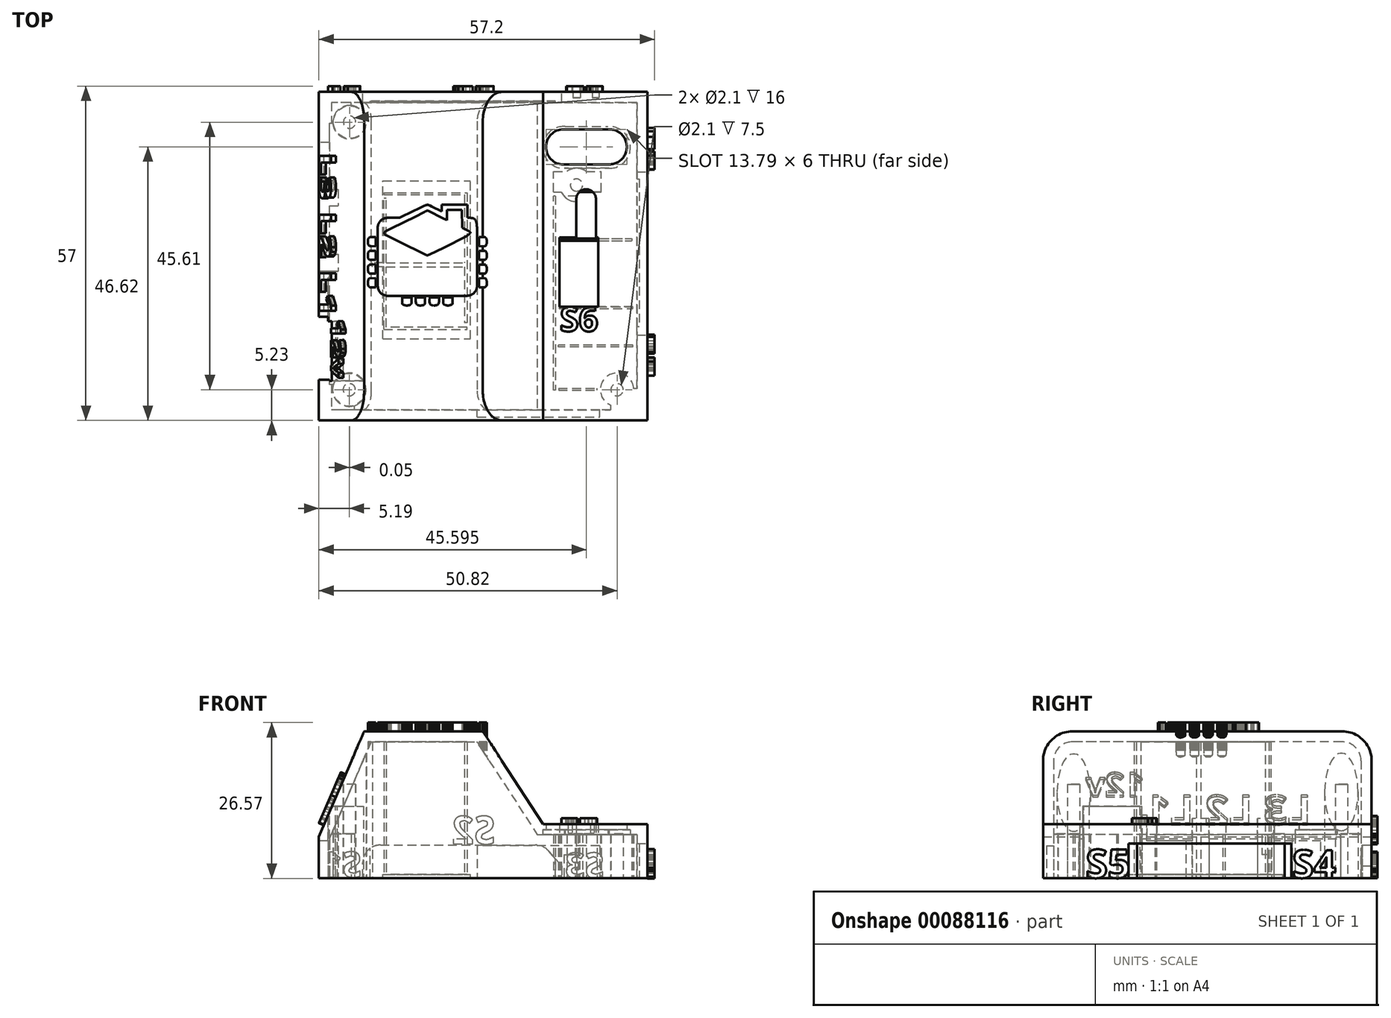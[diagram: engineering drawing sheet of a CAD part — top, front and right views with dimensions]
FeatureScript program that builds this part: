
annotation { "Feature Type Name" : "Feature", "Feature Type Description" : "" }
export const myFeature = defineFeature(function(context is Context, id is Id, definition is map)
    precondition{}
    {
        {
            var Q0;
            Q0=qCreatedBy(makeId("Top.planeOp"),FACE);
            var sketch = newSketch(context, id + "F0", { "sketchPlane" : qUnion([Q0])});
            skLineSegment(sketch, "E0.rect.bottom", {"start": v(22.84, -21.13) * mm, "end": v(-26.83, -21.13) * mm});
            skLineSegment(sketch, "E0.rect.top", {"start": v(22.84, 28.7) * mm, "end": v(-26.83, 28.7) * mm});
            skLineSegment(sketch, "E0.rect.left", {"start": v(22.84, -21.13) * mm, "end": v(22.84, 28.7) * mm});
            skPoint(sketch, "E0.rect.middle", {"position": v(-2, 3.78) * mm});
            skCircle(sketch, "E1", {"center": v(-24.81, -18.99) * mm, "radius": 1.05 * mm});
            skCircle(sketch, "E2", {"center": v(-24.76, 26.62) * mm, "radius": 1.05 * mm});
            skCircle(sketch, "E3", {"center": v(13.92, 15.91) * mm, "radius": 1.05 * mm});
            skLineSegment(sketch, "E4", {"start": v(-2, -21.13) * mm, "end": v(-2, -18.21) * mm});
            skCircle(sketch, "E5.MirrorC", {"center": v(20.82, -18.99) * mm, "radius": 1.05 * mm});
            skLineSegment(sketch, "E6.rect.bottom", {"start": v(24.75, -22.97) * mm, "end": v(-28.75, -22.97) * mm});
            skLineSegment(sketch, "E6.rect.top", {"start": v(24.75, 30.53) * mm, "end": v(-28.75, 30.53) * mm});
            skLineSegment(sketch, "E6.rect.left", {"start": v(24.75, -22.97) * mm, "end": v(24.75, 30.53) * mm});
            skLineSegment(sketch, "E6.rect.right", {"start": v(-28.75, -22.97) * mm, "end": v(-28.75, 30.53) * mm});
            skLineSegment(sketch, "E7.rect.bottom", {"start": v(26, -24.22) * mm, "end": v(-30, -24.22) * mm});
            skLineSegment(sketch, "E7.rect.top", {"start": v(26, 31.78) * mm, "end": v(-30, 31.78) * mm});
            skLineSegment(sketch, "E7.rect.left", {"start": v(26, -24.22) * mm, "end": v(26, 31.78) * mm});
            skLineSegment(sketch, "E7.rect.right", {"start": v(-30, -24.22) * mm, "end": v(-30, 31.78) * mm});
            skPoint(sketch, "E8", {"position": v(8.65, 14) * mm});
            skSolve(sketch);
        }
        {
            var Q0;
            Q0=qSketchRegion(id+"F0",true);
            var Q1;
            Q1=makeQuery(id+"F0.imprint","IMPRINT",FACE,{"disambiguationData":[TD([[makeQuery(id+"F0.imprint","IMPRINT",EDGE,{"derivedFrom":sQuery(id+"F0.wireOp",EDGE,"E1")}),-1.0]])]});
            extrude(context, id + "F1", {"entities" : qUnion([Q0, Q1]), "depth" : 25 * mm});
        }
        {
            var Q0;
            Q0=qCreatedBy(makeId("Front.planeOp"),FACE);
            var sketch = newSketch(context, id + "F2", { "sketchPlane" : qUnion([Q0])});
            skLineSegment(sketch, "E9", {"start": v(0, 0) * mm, "end": v(0, 7) * mm});
            skLineSegment(sketch, "E10", {"start": v(0, 7) * mm, "end": v(26.03, 7) * mm});
            skLineSegment(sketch, "E11", {"start": v(26.03, 9.19) * mm, "end": v(26.03, 25.51) * mm});
            skLineSegment(sketch, "E12", {"start": v(15.3, 7) * mm, "end": v(26.03, 7) * mm});
            skLineSegment(sketch, "E13", {"start": v(0, 7) * mm, "end": v(-30.02, 7) * mm});
            skLineSegment(sketch, "E14", {"start": v(-30.02, 7) * mm, "end": v(-22.06, 25.51) * mm});
            skLineSegment(sketch, "E15", {"start": v(-22.06, 25.51) * mm, "end": v(-2.39, 25.51) * mm});
            skLineSegment(sketch, "E16", {"start": v(26.03, 25.51) * mm, "end": v(-2.39, 25.51) * mm});
            skLineSegment(sketch, "E17", {"start": v(-22.06, 25.51) * mm, "end": v(-30.02, 25.51) * mm});
            skLineSegment(sketch, "E18", {"start": v(-30.02, 25.51) * mm, "end": v(-30.02, 7) * mm});
            skLineSegment(sketch, "E19", {"start": v(18.06, 10.7) * mm, "end": v(18.04, 10.7) * mm});
            skLineSegment(sketch, "E20", {"start": v(19.86, 9.19) * mm, "end": v(8.2, 9.19) * mm});
            skLineSegment(sketch, "E21", {"start": v(8.2, 9.19) * mm, "end": v(-2.39, 25.51) * mm});
            skLineSegment(sketch, "E22", {"start": v(19.86, 9.19) * mm, "end": v(26.03, 9.19) * mm});
            skSolve(sketch);
        }
        {
            var Q0;
            Q0=makeQuery(id+"F2.imprint","IMPRINT",FACE,{"disambiguationData":[TD([[makeQuery(id+"F2.imprint","IMPRINT",EDGE,{"derivedFrom":sQuery(id+"F2.wireOp",EDGE,"E14")}),1.0]])]});
            var Q1;
            {var subQ0=sQuery(id+"F2.wireOp",EDGE,"E11");Q1=makeQuery(id+"F2.imprint","IMPRINT",FACE,{"disambiguationData":[TD([[makeQuery(id+"F2.imprint","IMPRINT",EDGE,{"derivedFrom":subQ0}),1.0]])]});}
            extrude(context, id + "F3", {"entities" : qUnion([Q0, Q1]), "operationType" : NewBodyOperationType.REMOVE, "endBound" : BoundingType.UP_TO_NEXT, "oppositeDirection" : true, "depth" : 25 * mm, "hasSecondDirection" : true, "secondDirectionOppositeDirection" : false, "secondDirectionDepth" : 25 * mm});
        }
        {
            var Q0;
            Q0=makeQuery(id+"F1.opExtrude","CAP_EDGE",EDGE,{"disambiguationData":[OSD([sQuery(id+"F0.wireOp",EDGE,"E7.rect.right")])],"isStart":false});
            var Q1;
            Q1=makeQuery(id+"F3.boolean.opBoolean","COPY",EDGE,{"derivedFrom":makeQuery(id+"F3.opExtrude","TWEAK_EDGE",EDGE,{"derivedFrom":[makeQuery(id+"F1.opExtrude","CAP_FACE",FACE,{"disambiguationData":[OSD([sQuery(id+"F0.wireOp",EDGE,"E1"),sQuery(id+"F0.wireOp",EDGE,"E2"),sQuery(id+"F0.wireOp",EDGE,"E3"),sQuery(id+"F0.wireOp",EDGE,"E5.MirrorC"),sQuery(id+"F0.wireOp",EDGE,"E7.rect.bottom"),sQuery(id+"F0.wireOp",EDGE,"E7.rect.top"),sQuery(id+"F0.wireOp",EDGE,"E7.rect.left"),sQuery(id+"F0.wireOp",EDGE,"E7.rect.right")])],"isStart":false}),makeQuery(id+"F2.imprint","IMPRINT",EDGE,{"derivedFrom":sQuery(id+"F2.wireOp",EDGE,"ff17f17f-c23f-4b7b-92e3-773d52701edb")})]})});
            var Q2;
            Q2=makeQuery(id+"F3.boolean.opBoolean","COPY",EDGE,{"derivedFrom":makeQuery(id+"F3.opExtrude","TWEAK_EDGE",EDGE,{"derivedFrom":[makeQuery(id+"F1.opExtrude","CAP_FACE",FACE,{"disambiguationData":[OSD([sQuery(id+"F0.wireOp",EDGE,"E1"),sQuery(id+"F0.wireOp",EDGE,"E2"),sQuery(id+"F0.wireOp",EDGE,"E3"),sQuery(id+"F0.wireOp",EDGE,"E5.MirrorC"),sQuery(id+"F0.wireOp",EDGE,"E7.rect.bottom"),sQuery(id+"F0.wireOp",EDGE,"E7.rect.top"),sQuery(id+"F0.wireOp",EDGE,"E7.rect.left"),sQuery(id+"F0.wireOp",EDGE,"E7.rect.right")])],"isStart":false}),makeQuery(id+"F2.imprint","IMPRINT",EDGE,{"derivedFrom":sQuery(id+"F2.wireOp",EDGE,"7c30f75c-de24-4105-9ec6-0528e7197d9e")})]})});
            var Q3;
            {var subQ0=sQuery(id+"F2.wireOp",EDGE,"cpQ2IQLn-lepx-jHqE-Occg-QwCyzWVKbBFz");var subQ1=sQuery(id+"F2.wireOp",EDGE,"9136473a-ce9f-4df1-8e41-d79c079f6f02");var subQ2=makeQuery(id+"F2.imprint","INTERSECT",VERTEX,{"disambiguationData":[OD(0.0)],"derivedFrom":[subQ1,subQ0]});var subQ4=makeQuery(id+"F2.imprint","INTERSECT",VERTEX,{"disambiguationData":[OD(1.0)],"derivedFrom":[subQ1,subQ0]});Q3=makeQuery(id+"F3.boolean.opBoolean","COPY",EDGE,{"derivedFrom":makeQuery(id+"F3.opExtrude","TWEAK_EDGE",EDGE,{"derivedFrom":[makeQuery(id+"F1.opExtrude","CAP_FACE",FACE,{"disambiguationData":[OSD([sQuery(id+"F0.wireOp",EDGE,"E1"),sQuery(id+"F0.wireOp",EDGE,"E2"),sQuery(id+"F0.wireOp",EDGE,"E3"),sQuery(id+"F0.wireOp",EDGE,"E5.MirrorC"),sQuery(id+"F0.wireOp",EDGE,"E7.rect.bottom"),sQuery(id+"F0.wireOp",EDGE,"E7.rect.top"),sQuery(id+"F0.wireOp",EDGE,"E7.rect.left"),sQuery(id+"F0.wireOp",EDGE,"E7.rect.right")])],"isStart":false}),makeQuery(id+"F2.imprint","IMPRINT",EDGE,{"disambiguationData":[TD([[subQ4,1.0]])],"derivedFrom":subQ0}),makeQuery(id+"F2.imprint","IMPRINT",EDGE,{"disambiguationData":[TD([[subQ2,1.0]])],"derivedFrom":subQ0}),makeQuery(id+"F2.imprint","IMPRINT",EDGE,{"disambiguationData":[TD([[subQ2,-1.0]])],"derivedFrom":subQ0})]})});}
            var Q4;
            {var subQ0=sQuery(id+"F2.wireOp",EDGE,"cpQ2IQLn-lepx-jHqE-Occg-QwCyzWVKbBFz");var subQ1=sQuery(id+"F2.wireOp",EDGE,"9136473a-ce9f-4df1-8e41-d79c079f6f02");var subQ2=makeQuery(id+"F2.imprint","INTERSECT",VERTEX,{"disambiguationData":[OD(0.0)],"derivedFrom":[subQ1,subQ0]});var subQ3=sQuery(id+"F2.wireOp",EDGE,"7c30f75c-de24-4105-9ec6-0528e7197d9e");var subQ4=makeQuery(id+"F2.imprint","INTERSECT",VERTEX,{"derivedFrom":[subQ3,subQ0]});var subQ5=makeQuery(id+"F2.imprint","INTERSECT",VERTEX,{"disambiguationData":[OD(1.0)],"derivedFrom":[subQ1,subQ0]});Q4=makeQuery(id+"F3.boolean.opBoolean","COPY",EDGE,{"derivedFrom":makeQuery(id+"F3.opExtrude","TWEAK_EDGE",EDGE,{"disambiguationData":[OD(0.0)],"derivedFrom":[makeQuery(id+"F2.imprint","IMPRINT",EDGE,{"disambiguationData":[TD([[subQ4,1.0]])],"derivedFrom":subQ3}),makeQuery(id+"F2.imprint","IMPRINT",EDGE,{"disambiguationData":[TD([[subQ5,1.0]])],"derivedFrom":subQ0}),makeQuery(id+"F2.imprint","IMPRINT",EDGE,{"disambiguationData":[TD([[subQ2,1.0]])],"derivedFrom":subQ0}),makeQuery(id+"F2.imprint","IMPRINT",EDGE,{"disambiguationData":[TD([[subQ2,-1.0]])],"derivedFrom":subQ0})]})});}
            var Q5;
            {var subQ0=sQuery(id+"F2.wireOp",EDGE,"cpQ2IQLn-lepx-jHqE-Occg-QwCyzWVKbBFz");var subQ1=sQuery(id+"F2.wireOp",EDGE,"9136473a-ce9f-4df1-8e41-d79c079f6f02");var subQ2=makeQuery(id+"F2.imprint","INTERSECT",VERTEX,{"disambiguationData":[OD(0.0)],"derivedFrom":[subQ1,subQ0]});var subQ3=sQuery(id+"F2.wireOp",EDGE,"7c30f75c-de24-4105-9ec6-0528e7197d9e");var subQ4=makeQuery(id+"F2.imprint","INTERSECT",VERTEX,{"derivedFrom":[subQ3,subQ0]});var subQ5=makeQuery(id+"F2.imprint","INTERSECT",VERTEX,{"disambiguationData":[OD(1.0)],"derivedFrom":[subQ1,subQ0]});Q5=makeQuery(id+"F3.boolean.opBoolean","COPY",EDGE,{"derivedFrom":makeQuery(id+"F3.opExtrude","TWEAK_EDGE",EDGE,{"disambiguationData":[OD(1.0)],"derivedFrom":[makeQuery(id+"F2.imprint","IMPRINT",EDGE,{"disambiguationData":[TD([[subQ4,1.0]])],"derivedFrom":subQ3}),makeQuery(id+"F2.imprint","IMPRINT",EDGE,{"disambiguationData":[TD([[subQ5,1.0]])],"derivedFrom":subQ0}),makeQuery(id+"F2.imprint","IMPRINT",EDGE,{"disambiguationData":[TD([[subQ2,1.0]])],"derivedFrom":subQ0}),makeQuery(id+"F2.imprint","IMPRINT",EDGE,{"disambiguationData":[TD([[subQ2,-1.0]])],"derivedFrom":subQ0})]})});}
            var Q6;
            Q6=makeQuery(id+"F1.opExtrude","CAP_EDGE",EDGE,{"disambiguationData":[OSD([sQuery(id+"F0.wireOp",EDGE,"E7.rect.bottom")])],"isStart":false});
            var Q7;
            {var subQ0=sQuery(id+"F2.wireOp",EDGE,"cpQ2IQLn-lepx-jHqE-Occg-QwCyzWVKbBFz");var subQ1=sQuery(id+"F2.wireOp",EDGE,"9136473a-ce9f-4df1-8e41-d79c079f6f02");var subQ2=makeQuery(id+"F2.imprint","INTERSECT",VERTEX,{"disambiguationData":[OD(0.0)],"derivedFrom":[subQ1,subQ0]});var subQ4=makeQuery(id+"F2.imprint","INTERSECT",VERTEX,{"disambiguationData":[OD(1.0)],"derivedFrom":[subQ1,subQ0]});Q7=makeQuery(id+"F3.boolean.opBoolean","COPY",EDGE,{"derivedFrom":makeQuery(id+"F3.opExtrude","TWEAK_EDGE",EDGE,{"derivedFrom":[makeQuery(id+"F1.opExtrude","SWEPT_FACE",FACE,{"disambiguationData":[OSD([sQuery(id+"F0.wireOp",EDGE,"E7.rect.bottom")])]}),makeQuery(id+"F2.imprint","IMPRINT",EDGE,{"disambiguationData":[TD([[subQ4,1.0]])],"derivedFrom":subQ0}),makeQuery(id+"F2.imprint","IMPRINT",EDGE,{"disambiguationData":[TD([[subQ2,1.0]])],"derivedFrom":subQ0}),makeQuery(id+"F2.imprint","IMPRINT",EDGE,{"disambiguationData":[TD([[subQ2,-1.0]])],"derivedFrom":subQ0})]})});}
            var Q8;
            Q8=makeQuery(id+"F1.opExtrude","CAP_EDGE",EDGE,{"disambiguationData":[OSD([sQuery(id+"F0.wireOp",EDGE,"E7.rect.top")])],"isStart":false});
            var Q9;
            {var subQ0=sQuery(id+"F2.wireOp",EDGE,"cpQ2IQLn-lepx-jHqE-Occg-QwCyzWVKbBFz");var subQ1=sQuery(id+"F2.wireOp",EDGE,"9136473a-ce9f-4df1-8e41-d79c079f6f02");var subQ2=makeQuery(id+"F2.imprint","INTERSECT",VERTEX,{"disambiguationData":[OD(0.0)],"derivedFrom":[subQ1,subQ0]});var subQ4=makeQuery(id+"F2.imprint","INTERSECT",VERTEX,{"disambiguationData":[OD(1.0)],"derivedFrom":[subQ1,subQ0]});Q9=makeQuery(id+"F3.boolean.opBoolean","COPY",EDGE,{"derivedFrom":makeQuery(id+"F3.opExtrude","TWEAK_EDGE",EDGE,{"derivedFrom":[makeQuery(id+"F1.opExtrude","SWEPT_FACE",FACE,{"disambiguationData":[OSD([sQuery(id+"F0.wireOp",EDGE,"E7.rect.top")])]}),makeQuery(id+"F2.imprint","IMPRINT",EDGE,{"disambiguationData":[TD([[subQ4,1.0]])],"derivedFrom":subQ0}),makeQuery(id+"F2.imprint","IMPRINT",EDGE,{"disambiguationData":[TD([[subQ2,1.0]])],"derivedFrom":subQ0}),makeQuery(id+"F2.imprint","IMPRINT",EDGE,{"disambiguationData":[TD([[subQ2,-1.0]])],"derivedFrom":subQ0})]})});}
            var Q10;
            Q10=makeQuery(id+"F3.boolean.opBoolean","COPY",EDGE,{"derivedFrom":makeQuery(id+"F3.opExtrude","TWEAK_EDGE",EDGE,{"derivedFrom":[makeQuery(id+"F1.opExtrude","CAP_FACE",FACE,{"disambiguationData":[OSD([sQuery(id+"F0.wireOp",EDGE,"E1"),sQuery(id+"F0.wireOp",EDGE,"E2"),sQuery(id+"F0.wireOp",EDGE,"E3"),sQuery(id+"F0.wireOp",EDGE,"E5.MirrorC"),sQuery(id+"F0.wireOp",EDGE,"E7.rect.bottom"),sQuery(id+"F0.wireOp",EDGE,"E7.rect.top"),sQuery(id+"F0.wireOp",EDGE,"E7.rect.left"),sQuery(id+"F0.wireOp",EDGE,"E7.rect.right")])],"isStart":false}),makeQuery(id+"F2.imprint","IMPRINT",EDGE,{"derivedFrom":sQuery(id+"F2.wireOp",EDGE,"99fa5713-44e2-4710-8a3e-a5a5802f03ed")})]})});
            var Q11;
            Q11=makeQuery(id+"F3.boolean.opBoolean","COPY",EDGE,{"derivedFrom":makeQuery(id+"F3.opExtrude","TWEAK_EDGE",EDGE,{"derivedFrom":[makeQuery(id+"F1.opExtrude","CAP_FACE",FACE,{"disambiguationData":[OSD([sQuery(id+"F0.wireOp",EDGE,"E1"),sQuery(id+"F0.wireOp",EDGE,"E2"),sQuery(id+"F0.wireOp",EDGE,"E3"),sQuery(id+"F0.wireOp",EDGE,"E5.MirrorC"),sQuery(id+"F0.wireOp",EDGE,"E7.rect.bottom"),sQuery(id+"F0.wireOp",EDGE,"E7.rect.top"),sQuery(id+"F0.wireOp",EDGE,"E7.rect.left"),sQuery(id+"F0.wireOp",EDGE,"E7.rect.right")])],"isStart":false}),makeQuery(id+"F2.imprint","IMPRINT",EDGE,{"derivedFrom":sQuery(id+"F2.wireOp",EDGE,"E14")})]})});
            var Q12;
            Q12=makeQuery(id+"F3.boolean.opBoolean","COPY",EDGE,{"derivedFrom":makeQuery(id+"F3.opExtrude","TWEAK_EDGE",EDGE,{"derivedFrom":[makeQuery(id+"F1.opExtrude","CAP_FACE",FACE,{"disambiguationData":[OSD([sQuery(id+"F0.wireOp",EDGE,"E1"),sQuery(id+"F0.wireOp",EDGE,"E2"),sQuery(id+"F0.wireOp",EDGE,"E3"),sQuery(id+"F0.wireOp",EDGE,"E5.MirrorC"),sQuery(id+"F0.wireOp",EDGE,"E7.rect.bottom"),sQuery(id+"F0.wireOp",EDGE,"E7.rect.top"),sQuery(id+"F0.wireOp",EDGE,"E7.rect.left"),sQuery(id+"F0.wireOp",EDGE,"E7.rect.right")])],"isStart":false}),makeQuery(id+"F2.imprint","IMPRINT",EDGE,{"derivedFrom":sQuery(id+"F2.wireOp",EDGE,"E21")})]})});
            var Q13;
            Q13=makeQuery(id+"F3.boolean.opBoolean","COPY",EDGE,{"derivedFrom":makeQuery(id+"F3.opExtrude","TWEAK_EDGE",EDGE,{"derivedFrom":[makeQuery(id+"F2.imprint","IMPRINT",EDGE,{"derivedFrom":sQuery(id+"F2.wireOp",EDGE,"E20")}),makeQuery(id+"F2.imprint","IMPRINT",EDGE,{"derivedFrom":sQuery(id+"F2.wireOp",EDGE,"E21")})]})});
            var Q14;
            Q14=makeQuery(id+"F3.boolean.opBoolean","COPY",EDGE,{"derivedFrom":makeQuery(id+"F3.opExtrude","TWEAK_EDGE",EDGE,{"derivedFrom":[makeQuery(id+"F1.opExtrude","SWEPT_FACE",FACE,{"disambiguationData":[OSD([sQuery(id+"F0.wireOp",EDGE,"E7.rect.bottom")])]}),makeQuery(id+"F2.imprint","IMPRINT",EDGE,{"derivedFrom":sQuery(id+"F2.wireOp",EDGE,"E21")})]})});
            var Q15;
            Q15=makeQuery(id+"F3.boolean.opBoolean","COPY",EDGE,{"derivedFrom":makeQuery(id+"F3.opExtrude","TWEAK_EDGE",EDGE,{"derivedFrom":[makeQuery(id+"F1.opExtrude","SWEPT_FACE",FACE,{"disambiguationData":[OSD([sQuery(id+"F0.wireOp",EDGE,"E7.rect.top")])]}),makeQuery(id+"F2.imprint","IMPRINT",EDGE,{"derivedFrom":sQuery(id+"F2.wireOp",EDGE,"E21")})]})});
            var Q16;
            Q16=makeQuery(id+"F3.boolean.opBoolean","COPY",EDGE,{"derivedFrom":makeQuery(id+"F3.opExtrude","TWEAK_EDGE",EDGE,{"derivedFrom":[makeQuery(id+"F1.opExtrude","SWEPT_FACE",FACE,{"disambiguationData":[OSD([sQuery(id+"F0.wireOp",EDGE,"E7.rect.left")])]}),makeQuery(id+"F2.imprint","IMPRINT",EDGE,{"derivedFrom":sQuery(id+"F2.wireOp",EDGE,"E20")}),makeQuery(id+"F2.imprint","IMPRINT",EDGE,{"derivedFrom":sQuery(id+"F2.wireOp",EDGE,"E22")})]})});
            var Q17;
            Q17=makeQuery(id+"F3.boolean.opBoolean","COPY",EDGE,{"derivedFrom":makeQuery(id+"F3.opExtrude","TWEAK_EDGE",EDGE,{"derivedFrom":[makeQuery(id+"F2.imprint","IMPRINT",EDGE,{"derivedFrom":sQuery(id+"F2.wireOp",EDGE,"E20")}),makeQuery(id+"F2.imprint","IMPRINT",EDGE,{"derivedFrom":sQuery(id+"F2.wireOp",EDGE,"E21")}),makeQuery(id+"F2.imprint","IMPRINT",EDGE,{"derivedFrom":sQuery(id+"F2.wireOp",EDGE,"E22")})]})});
            fillet(context, id + "F4", {"entities" : qUnion([Q0, Q1, Q2, Q3, Q4, Q5, Q6, Q7, Q8, Q9, Q10, Q11, Q12, Q13, Q14, Q15, Q16, Q17]), "radius" : 5 * mm, "tangentPropagation" : true, "allowEdgeOverflow" : false});
        }
        {
            var Q0;
            Q0=makeQuery(id+"F1.opExtrude","SWEPT_BODY",BODY,{"disambiguationData":[OSD([sQuery(id+"F0.wireOp",EDGE,"E1"),sQuery(id+"F0.wireOp",EDGE,"E2"),sQuery(id+"F0.wireOp",EDGE,"E3"),sQuery(id+"F0.wireOp",EDGE,"E5.MirrorC"),sQuery(id+"F0.wireOp",EDGE,"E7.rect.bottom"),sQuery(id+"F0.wireOp",EDGE,"E7.rect.top"),sQuery(id+"F0.wireOp",EDGE,"E7.rect.left"),sQuery(id+"F0.wireOp",EDGE,"E7.rect.right")])]});
            transform(context, id + "F5", {"entities" : qUnion([Q0]), "transformType" : TransformType.TRANSLATION_3D, "dx" : -5 * mm, "dy" : -12 * mm, "dz" : 0 * mm, "makeCopy" : false});
        }
        {
            var Q0;
            Q0=makeQuery(id+"F1.opExtrude","CAP_FACE",FACE,{"disambiguationData":[OSD([sQuery(id+"F0.wireOp",EDGE,"E1"),sQuery(id+"F0.wireOp",EDGE,"E2"),sQuery(id+"F0.wireOp",EDGE,"E3"),sQuery(id+"F0.wireOp",EDGE,"E5.MirrorC"),sQuery(id+"F0.wireOp",EDGE,"E7.rect.bottom"),sQuery(id+"F0.wireOp",EDGE,"E7.rect.top"),sQuery(id+"F0.wireOp",EDGE,"E7.rect.left"),sQuery(id+"F0.wireOp",EDGE,"E7.rect.right")])],"isStart":true});
            shell(context, id + "F6", {"entities" : qUnion([Q0]), "thickness" : 1.8 * mm});
        }
        {
            var Q0;
            Q0=makeQuery(id+"F1.opExtrude","SWEPT_FACE",FACE,{"disambiguationData":[OSD([sQuery(id+"F0.wireOp",EDGE,"E7.rect.left")])]});
            cPlane(context, id + "F7", {"entities" : qUnion([Q0]), "cplaneType" : CPlaneType.OFFSET, "offset" : 0 * mm, "width" : 150 * mm, "height" : 150 * mm});
        }
        {
            var Q0;
            Q0=qCreatedBy(id+"F7.planeOp",FACE);
            var sketch = newSketch(context, id + "F8", { "sketchPlane" : qUnion([Q0])});
            skLineSegment(sketch, "E23.bottom", {"start": v(6.92, 0) * mm, "end": v(-20.2, 0) * mm});
            skLineSegment(sketch, "E23.top", {"start": v(6.12, 5.87) * mm, "end": v(-20.2, 5.87) * mm});
            skLineSegment(sketch, "E24", {"start": v(-20.2, 5.87) * mm, "end": v(-21.64, 5.87) * mm});
            skLineSegment(sketch, "E25", {"start": v(-21.64, 5.87) * mm, "end": v(-21.64, 0) * mm});
            skLineSegment(sketch, "E26", {"start": v(-21.64, 0) * mm, "end": v(-20.2, 0) * mm});
            skLineSegment(sketch, "E27", {"start": v(-20.2, 5.87) * mm, "end": v(-20.2, 0) * mm});
            skLineSegment(sketch, "E28", {"start": v(6.12, 5.87) * mm, "end": v(6.12, 0) * mm});
            skPoint(sketch, "E29.orphan", {"position": v(7.84, 0) * mm});
            skLineSegment(sketch, "E30", {"start": v(4.97, 0) * mm, "end": v(4.97, 5.87) * mm});
            skSolve(sketch);
        }
        {
            var Q0;
            Q0=qSketchRegion(id+"F8",true);
            extrude(context, id + "F9", {"entities" : qUnion([Q0]), "operationType" : NewBodyOperationType.REMOVE, "oppositeDirection" : true, "depth" : (1.7 - 0.3) * mm});
        }
        {
            var Q0;
            Q0=makeQuery(id+"F8.imprint","IMPRINT",FACE,{"disambiguationData":[TD([[makeQuery(id+"F8.imprint","IMPRINT",EDGE,{"derivedFrom":sQuery(id+"F8.wireOp",EDGE,"E24")}),1.0]])]});
            var Q1;
            {var subQ0=sQuery(id+"F8.wireOp",EDGE,"E23.left");Q1=makeQuery(id+"F8.imprint","IMPRINT",FACE,{"disambiguationData":[TD([[makeQuery(id+"F8.imprint","IMPRINT",EDGE,{"derivedFrom":subQ0}),1.0]])]});}
            var Q2;
            {var subQ0=sQuery(id+"F8.wireOp",EDGE,"4UiORLbo-slaH-JSft-xh6I-61qYCNnPId7j");Q2=makeQuery(id+"F8.imprint","IMPRINT",FACE,{"disambiguationData":[TD([[makeQuery(id+"F8.imprint","IMPRINT",EDGE,{"derivedFrom":subQ0}),1.0]])]});}
            var Q3;
            {var subQ0=sQuery(id+"F8.wireOp",EDGE,"E28");Q3=makeQuery(id+"F8.imprint","IMPRINT",FACE,{"disambiguationData":[TD([[makeQuery(id+"F8.imprint","IMPRINT",EDGE,{"derivedFrom":subQ0}),-1.0]])]});}
            extrude(context, id + "F10", {"entities" : qUnion([Q0, Q1, Q2, Q3]), "operationType" : NewBodyOperationType.REMOVE, "oppositeDirection" : true, "depth" : 2 * mm});
        }
        {
            var Q0;
            Q0=makeQuery(id+"F1.opExtrude","SWEPT_FACE",FACE,{"disambiguationData":[OSD([sQuery(id+"F0.wireOp",EDGE,"E7.rect.right")])]});
            cPlane(context, id + "F11", {"entities" : qUnion([Q0]), "cplaneType" : CPlaneType.OFFSET, "offset" : 0 * mm, "width" : 150 * mm, "height" : 150 * mm});
        }
        {
            var Q0;
            Q0=qCreatedBy(id+"F11.planeOp",FACE);
            var sketch = newSketch(context, id + "F12", { "sketchPlane" : qUnion([Q0])});
            skLineSegment(sketch, "E31.top", {"start": v(-11.15, 6.31) * mm, "end": v(-3.45, 6.31) * mm});
            skLineSegment(sketch, "E32", {"start": v(27.25, 11.15) * mm, "end": v(27.25, 11.15) * mm});
            skLineSegment(sketch, "E33", {"start": v(-11.15, 0) * mm, "end": v(-11.15, 6.31) * mm});
            skPoint(sketch, "E34.start.orphan", {"position": v(-15.15, 0) * mm});
            skLineSegment(sketch, "E35", {"start": v(29.28, 0) * mm, "end": v(-11.15, 0) * mm});
            skLineSegment(sketch, "E36", {"start": v(-10.29, 6.31) * mm, "end": v(-10.29, 0) * mm});
            skLineSegment(sketch, "E37", {"start": v(19.35, 12.2) * mm, "end": v(29.28, 12.2) * mm});
            skLineSegment(sketch, "E38", {"start": v(-11.15, 3.16) * mm, "end": v(-3.45, 3.16) * mm, "construction": true});
            skLineSegment(sketch, "E39", {"start": v(-3.45, 3.16) * mm, "end": v(-0.05, 3.16) * mm, "construction": true});
            skLineSegment(sketch, "E40", {"start": v(-0.05, 3.16) * mm, "end": v(7.65, 3.16) * mm, "construction": true});
            skLineSegment(sketch, "E41", {"start": v(7.65, 3.16) * mm, "end": v(11.05, 3.16) * mm, "construction": true});
            skLineSegment(sketch, "E42.trimOffspring", {"start": v(11.05, 6.31) * mm, "end": v(18.53, 6.31) * mm});
            skLineSegment(sketch, "E43", {"start": v(11.9, 6.31) * mm, "end": v(11.9, 0) * mm});
            skLineSegment(sketch, "E44", {"start": v(0, 6.31) * mm, "end": v(7.65, 6.31) * mm});
            skLineSegment(sketch, "E45", {"start": v(7.65, 0) * mm, "end": v(0, 0) * mm});
            skLineSegment(sketch, "E46", {"start": v(-3.45, 0) * mm, "end": v(-11.15, 0) * mm});
            skLineSegment(sketch, "E47", {"start": v(30.08, 0) * mm, "end": v(11.05, 0) * mm});
            skLineSegment(sketch, "E48.bottom", {"start": v(-0.32, 0) * mm, "end": v(-3.15, 0) * mm});
            skLineSegment(sketch, "E48.top", {"start": v(-0.32, 6.31) * mm, "end": v(-3.15, 6.31) * mm});
            skLineSegment(sketch, "E48.left", {"start": v(-0.32, 0) * mm, "end": v(-0.32, 6.31) * mm});
            skLineSegment(sketch, "E48.right", {"start": v(-3.15, 0) * mm, "end": v(-3.15, 6.31) * mm});
            skLineSegment(sketch, "E49.bottom", {"start": v(10.8, 0) * mm, "end": v(7.92, 0) * mm});
            skLineSegment(sketch, "E49.top", {"start": v(10.8, 6.31) * mm, "end": v(7.92, 6.31) * mm});
            skLineSegment(sketch, "E49.left", {"start": v(10.8, 0) * mm, "end": v(10.8, 6.31) * mm});
            skLineSegment(sketch, "E49.right", {"start": v(7.92, 0) * mm, "end": v(7.92, 6.31) * mm});
            skLineSegment(sketch, "E50", {"start": v(-3.45, 6.31) * mm, "end": v(11.05, 6.31) * mm});
            skLineSegment(sketch, "E51", {"start": v(29.28, 12.2) * mm, "end": v(29.28, 0) * mm});
            skPoint(sketch, "E52.end.orphan", {"position": v(30.08, 11.15) * mm});
            skPoint(sketch, "E52.start.orphan", {"position": v(30.08, 12.2) * mm});
            skLineSegment(sketch, "E53", {"start": v(18.53, 6.31) * mm, "end": v(18.53, 12.2) * mm});
            skLineSegment(sketch, "E54", {"start": v(18.53, 12.2) * mm, "end": v(19.35, 12.2) * mm});
            skPoint(sketch, "E55.start.orphan", {"position": v(19.35, 11.15) * mm});
            skPoint(sketch, "E56.end.orphan", {"position": v(19.35, 0) * mm});
            skPoint(sketch, "E56.start.orphan", {"position": v(19.35, 6.31) * mm});
            skLineSegment(sketch, "E57", {"start": v(28.38, 0) * mm, "end": v(28.38, 12.2) * mm});
            skLineSegment(sketch, "E58", {"start": v(19.35, 12.2) * mm, "end": v(19.35, 0) * mm});
            skSolve(sketch);
        }
        {
            var Q0;
            {var subQ0=sQuery(id+"F12.wireOp",EDGE,"E33");Q0=makeQuery(id+"F12.imprint","IMPRINT",FACE,{"disambiguationData":[TD([[makeQuery(id+"F12.imprint","IMPRINT",EDGE,{"derivedFrom":subQ0}),-1.0]])]});}
            var Q1;
            {var subQ1=sQuery(id+"F12.wireOp",EDGE,"E36");Q1=makeQuery(id+"F12.imprint","IMPRINT",FACE,{"disambiguationData":[TD([[makeQuery(id+"F12.imprint","IMPRINT",EDGE,{"derivedFrom":subQ1}),1.0]])]});}
            var Q2;
            {var subQ0=sQuery(id+"F12.wireOp",EDGE,"LVVauTd6-uSLQ-SWm0-nvuu-HrEgJgk2loCY");Q2=makeQuery(id+"F12.imprint","IMPRINT",FACE,{"disambiguationData":[TD([[makeQuery(id+"F12.imprint","IMPRINT",EDGE,{"derivedFrom":subQ0}),-1.0]])]});}
            var Q3;
            Q3=makeQuery(id+"F12.imprint","IMPRINT",FACE,{"disambiguationData":[TD([[makeQuery(id+"F12.imprint","IMPRINT",EDGE,{"derivedFrom":sQuery(id+"F12.wireOp",EDGE,"Bzj0w9RH-aYdH-ZF7y-Z4mK-Pif1xP8myCSu")}),1.0]])]});
            var Q4;
            {var subQ2=sQuery(id+"F12.wireOp",EDGE,"E43");Q4=makeQuery(id+"F12.imprint","IMPRINT",FACE,{"disambiguationData":[TD([[makeQuery(id+"F12.imprint","IMPRINT",EDGE,{"derivedFrom":subQ2}),1.0]])]});}
            extrude(context, id + "F13", {"entities" : qUnion([Q0, Q1, Q2, Q3, Q4]), "operationType" : NewBodyOperationType.REMOVE, "oppositeDirection" : true, "depth" : 1.6 * mm});
        }
        {
            var Q0;
            {var subQ2=sQuery(id+"F12.wireOp",EDGE,"E57");Q0=makeQuery(id+"F12.imprint","IMPRINT",FACE,{"disambiguationData":[TD([[makeQuery(id+"F12.imprint","IMPRINT",EDGE,{"derivedFrom":subQ2}),1.0]])]});}
            var Q1;
            {var subQ0=sQuery(id+"F12.wireOp",EDGE,"E33");Q1=makeQuery(id+"F12.imprint","IMPRINT",FACE,{"disambiguationData":[TD([[makeQuery(id+"F12.imprint","IMPRINT",EDGE,{"derivedFrom":subQ0}),-1.0]])]});}
            var Q2;
            {var subQ1=sQuery(id+"F12.wireOp",EDGE,"E45");Q2=makeQuery(id+"F12.imprint","IMPRINT",FACE,{"disambiguationData":[TD([[makeQuery(id+"F12.imprint","IMPRINT",EDGE,{"derivedFrom":subQ1}),-1.0]])]});}
            var Q3;
            {var subQ3=sQuery(id+"F12.wireOp",EDGE,"E36");Q3=makeQuery(id+"F12.imprint","IMPRINT",FACE,{"disambiguationData":[TD([[makeQuery(id+"F12.imprint","IMPRINT",EDGE,{"derivedFrom":subQ3}),1.0]])]});}
            var Q4;
            {var subQ3=sQuery(id+"F12.wireOp",EDGE,"E43");Q4=makeQuery(id+"F12.imprint","IMPRINT",FACE,{"disambiguationData":[TD([[makeQuery(id+"F12.imprint","IMPRINT",EDGE,{"derivedFrom":subQ3}),-1.0]])]});}
            var Q5;
            {var subQ0=sQuery(id+"F12.wireOp",EDGE,"E51");Q5=makeQuery(id+"F12.imprint","IMPRINT",FACE,{"disambiguationData":[TD([[makeQuery(id+"F12.imprint","IMPRINT",EDGE,{"derivedFrom":subQ0}),-1.0]])]});}
            extrude(context, id + "F14", {"entities" : qUnion([Q0, Q1, Q2, Q3, Q4, Q5]), "operationType" : NewBodyOperationType.REMOVE, "oppositeDirection" : true, "depth" : 8 * mm});
        }
        {
            var Q0;
            Q0=qCreatedBy(makeId("Top.planeOp"),FACE);
            var sketch = newSketch(context, id + "F15", { "sketchPlane" : qUnion([Q0])});
            skLineSegment(sketch, "E59.bottom", {"start": v(-27.19, -29.45) * mm, "end": v(-33.17, -29.45) * mm});
            skLineSegment(sketch, "E59.top", {"start": v(-27.19, -20) * mm, "end": v(-33.17, -20) * mm});
            skLineSegment(sketch, "E59.left", {"start": v(-27.19, -29.45) * mm, "end": v(-27.19, -21.32) * mm});
            skLineSegment(sketch, "E59.right", {"start": v(-33.17, -29.45) * mm, "end": v(-33.17, -21.32) * mm});
            skLineSegment(sketch, "E60", {"start": v(-33.17, -20.99) * mm, "end": v(-27.19, -20.99) * mm});
            skLineSegment(sketch, "E61", {"start": v(-33.17, -21.32) * mm, "end": v(-27.19, -21.32) * mm});
            skLineSegment(sketch, "E62.trimOffspring", {"start": v(-27.19, -20.99) * mm, "end": v(-27.19, -20) * mm});
            skLineSegment(sketch, "E63.trimOffspring", {"start": v(-33.17, -20.99) * mm, "end": v(-33.17, -20) * mm});
            skSolve(sketch);
        }
        {
            var Q0;
            Q0=qSketchRegion(id+"F15",true);
            var Q1;
            {var subQ0=sQuery(id+"F12.wireOp",EDGE,"E37");Q1=makeQuery(id+"F14.boolean.opBoolean","COPY",FACE,{"derivedFrom":makeQuery(id+"F14.opExtrude","SWEPT_FACE",FACE,{"disambiguationData":[OSD([subQ0]),TDD([makeQuery(id+"F12.imprint","IMPRINT",EDGE,{"disambiguationData":[TD([[makeQuery(id+"F12.imprint","INTERSECT",VERTEX,{"derivedFrom":[subQ0,sQuery(id+"F12.wireOp",EDGE,"E52")]}),1.0]])],"derivedFrom":subQ0})])]})});}
            extrude(context, id + "F16", {"entities" : qUnion([Q0]), "operationType" : NewBodyOperationType.REMOVE, "endBound" : BoundingType.UP_TO_SURFACE, "endBoundEntityFace" : qUnion([Q1]), "depth" : 11.3 * mm});
        }
        {
            var Q0;
            Q0=makeQuery(id+"F1.opExtrude","SWEPT_FACE",FACE,{"disambiguationData":[OSD([sQuery(id+"F0.wireOp",EDGE,"E7.rect.top")])]});
            cPlane(context, id + "F17", {"entities" : qUnion([Q0]), "cplaneType" : CPlaneType.OFFSET, "offset" : 0 * mm, "width" : 150 * mm, "height" : 150 * mm});
        }
        {
            var Q0;
            Q0=qCreatedBy(id+"F17.planeOp",FACE);
            var sketch = newSketch(context, id + "F18", { "sketchPlane" : qUnion([Q0])});
            skLineSegment(sketch, "E64.bottom", {"start": v(-6.36, 0) * mm, "end": v(27.5, 0) * mm});
            skLineSegment(sketch, "E64.left", {"start": v(-6.36, 0) * mm, "end": v(-6.36, 2.05) * mm});
            skLineSegment(sketch, "E65", {"start": v(-5.32, 3.26) * mm, "end": v(-5.32, 0) * mm});
            skLineSegment(sketch, "E66", {"start": v(27.5, 2.61) * mm, "end": v(27.5, 0) * mm});
            skLineSegment(sketch, "E67", {"start": v(26.27, 5.04) * mm, "end": v(26.27, 0) * mm});
            skPoint(sketch, "E68.visualSharp", {"position": v(-6.36, 7.05) * mm});
            skLineSegment(sketch, "E69", {"start": v(-6.36, 2.05) * mm, "end": v(-4.17, 4.58) * mm});
            skLineSegment(sketch, "E70", {"start": v(24.5, 5.61) * mm, "end": v(-1.9, 5.61) * mm});
            skPoint(sketch, "E71.visualSharp", {"position": v(-3.28, 5.61) * mm});
            skArc(sketch, "E71.filletArc", {"start": v(-1.9, 5.61) * mm, "mid": v(-3.15, 5.34) * mm, "end": v(-4.17, 4.58) * mm});
            skPoint(sketch, "E72.visualSharp", {"position": v(27.5, 5.61) * mm});
            skArc(sketch, "E72.filletArc", {"start": v(27.5, 2.61) * mm, "mid": v(26.63, 4.73) * mm, "end": v(24.5, 5.61) * mm});
            skSolve(sketch);
        }
        {
            var Q0;
            Q0=qSketchRegion(id+"F18",true);
            extrude(context, id + "F19", {"entities" : qUnion([Q0]), "operationType" : NewBodyOperationType.REMOVE, "oppositeDirection" : true, "depth" : 1.6 * mm});
        }
        {
            var Q0;
            Q0=qCreatedBy(makeId("Top.planeOp"),FACE);
            var sketch = newSketch(context, id + "F20", { "sketchPlane" : qUnion([Q0])});
            skArc(sketch, "E73", {"start": v(6.16, 2.02) * mm, "mid": v(8.9, 0.56) * mm, "end": v(11.63, 2.02) * mm});
            skLineSegment(sketch, "E74", {"start": v(11.63, 2.02) * mm, "end": v(6.16, 2.02) * mm});
            skSolve(sketch);
        }
        {
            var Q0;
            Q0=qSketchRegion(id+"F20",true);
            extrude(context, id + "F21", {"entities" : qUnion([Q0]), "operationType" : NewBodyOperationType.REMOVE, "depth" : 4 * mm});
        }
        {
            var Q0;
            {var subQ0=sQuery(id+"F18.wireOp",EDGE,"E64.left");Q0=makeQuery(id+"F18.imprint","IMPRINT",FACE,{"disambiguationData":[TD([[makeQuery(id+"F18.imprint","IMPRINT",EDGE,{"derivedFrom":subQ0}),-1.0]])]});}
            var Q1;
            {var subQ0=sQuery(id+"F18.wireOp",EDGE,"E64.right");Q1=makeQuery(id+"F18.imprint","IMPRINT",FACE,{"disambiguationData":[TD([[makeQuery(id+"F18.imprint","IMPRINT",EDGE,{"derivedFrom":subQ0}),1.0]])]});}
            extrude(context, id + "F22", {"entities" : qUnion([Q0, Q1]), "operationType" : NewBodyOperationType.REMOVE, "oppositeDirection" : true, "depth" : 2 * mm});
        }
        {
            var Q0;
            Q0=qCreatedBy(makeId("Top.planeOp"),FACE);
            var sketch = newSketch(context, id + "F23", { "sketchPlane" : qUnion([Q0])});
            skLineSegment(sketch, "E75", {"start": v(21, 19.9) * mm, "end": v(21, 10.4) * mm, "construction": true});
            skLineSegment(sketch, "E76", {"start": v(12.22, 0) * mm, "end": v(12.22, -5.06) * mm});
            skLineSegment(sketch, "E77", {"start": v(12.22, 0) * mm, "end": v(12.22, 1.5) * mm});
            skArc(sketch, "E78", {"start": v(14.47, 7.42) * mm, "mid": v(17.49, 10.4) * mm, "end": v(14.5, 13.4) * mm});
            skArc(sketch, "E79", {"start": v(6.7, 13.4) * mm, "mid": v(3.7, 10.4) * mm, "end": v(6.7, 7.4) * mm});
            skLineSegment(sketch, "E80", {"start": v(14.5, 13.4) * mm, "end": v(6.7, 13.4) * mm});
            skLineSegment(sketch, "E81", {"start": v(6.7, 7.4) * mm, "end": v(14.54, 7.42) * mm});
            skLineSegment(sketch, "E82", {"start": v(6, -5.57) * mm, "end": v(6, -16.85) * mm});
            skLineSegment(sketch, "E83", {"start": v(12.6, -16.85) * mm, "end": v(6, -16.85) * mm});
            skPoint(sketch, "E84.center.orphan", {"position": v(10.72, -16.85) * mm});
            skLineSegment(sketch, "E85", {"start": v(12.6, -5.57) * mm, "end": v(12.6, -16.85) * mm});
            skLineSegment(sketch, "E86", {"start": v(8.87, -5.06) * mm, "end": v(8.87, 1.5) * mm});
            skArc(sketch, "E87", {"start": v(12.22, 1.5) * mm, "mid": v(10.54, 3.17) * mm, "end": v(8.87, 1.5) * mm});
            skPoint(sketch, "E88.orphan", {"position": v(12.22, -16.85) * mm});
            skLineSegment(sketch, "E89", {"start": v(0, 0) * mm, "end": v(0, 19.9) * mm, "construction": true});
            skLineSegment(sketch, "E90", {"start": v(0, 19.9) * mm, "end": v(21, 19.9) * mm, "construction": true});
            skLineSegment(sketch, "E91", {"start": v(14.5, 10.4) * mm, "end": v(21, 10.4) * mm, "construction": true});
            skLineSegment(sketch, "E92", {"start": v(8.87, -5.06) * mm, "end": v(6, -5.06) * mm});
            skLineSegment(sketch, "E93", {"start": v(6, -5.06) * mm, "end": v(6, -5.57) * mm});
            skLineSegment(sketch, "E94", {"start": v(12.22, -5.06) * mm, "end": v(12.6, -5.06) * mm});
            skLineSegment(sketch, "E95", {"start": v(12.6, -5.06) * mm, "end": v(12.6, -5.57) * mm});
            skSolve(sketch);
        }
        {
            var Q0;
            Q0=qSketchRegion(id+"F23",true);
            extrude(context, id + "F24", {"entities" : qUnion([Q0]), "operationType" : NewBodyOperationType.REMOVE, "depth" : 25 * mm});
        }
        {
            var Q0;
            Q0=qCreatedBy(makeId("Top.planeOp"),FACE);
            var sketch = newSketch(context, id + "F25", { "sketchPlane" : qUnion([Q0])});
            skLineSegment(sketch, "E96", {"start": v(18.49, -17.16) * mm, "end": v(5.97, -17.16) * mm});
            skLineSegment(sketch, "E97", {"start": v(18.49, -16.86) * mm, "end": v(5.97, -16.86) * mm});
            skLineSegment(sketch, "E98", {"start": v(12.44, -31.08) * mm, "end": v(5.87, -31.08) * mm});
            skLineSegment(sketch, "E99", {"start": v(12.44, -30.78) * mm, "end": v(5.87, -30.78) * mm});
            skLineSegment(sketch, "E100.bottom", {"start": v(-33.84, 14.47) * mm, "end": v(-32.16, 14.47) * mm});
            skLineSegment(sketch, "E100.top", {"start": v(-33.84, 18.7) * mm, "end": v(-29.5, 18.7) * mm});
            skLineSegment(sketch, "E100.left", {"start": v(-33.84, 14.47) * mm, "end": v(-33.84, 18.7) * mm});
            skLineSegment(sketch, "E100.right", {"start": v(-29.5, 16.74) * mm, "end": v(-29.5, 18.7) * mm});
            skArc(sketch, "E101", {"start": v(-29.5, 16.74) * mm, "mid": v(-31.35, 16.22) * mm, "end": v(-32.16, 14.47) * mm});
            skLineSegment(sketch, "E102.bottom", {"start": v(-33.6, -31.08) * mm, "end": v(-33.6, -31.08) * mm});
            skLineSegment(sketch, "E102.top", {"start": v(-33.6, -34.81) * mm, "end": v(-31.03, -34.81) * mm});
            skLineSegment(sketch, "E102.left", {"start": v(-33.6, -31.08) * mm, "end": v(-33.6, -34.81) * mm});
            skLineSegment(sketch, "E102.right", {"start": v(-31.03, -31.08) * mm, "end": v(-31.03, -33.21) * mm});
            skLineSegment(sketch, "E103.bottom", {"start": v(-31.03, -34.81) * mm, "end": v(-28.95, -34.81) * mm});
            skLineSegment(sketch, "E103.top", {"start": v(-31.03, -33.21) * mm, "end": v(-28.95, -33.21) * mm});
            skLineSegment(sketch, "E103.right", {"start": v(-28.95, -34.81) * mm, "end": v(-28.95, -33.21) * mm});
            skPoint(sketch, "E104.end.orphan", {"position": v(-34.98, -31.08) * mm});
            skPoint(sketch, "E104.start.orphan", {"position": v(-34.98, -30.78) * mm});
            skLineSegment(sketch, "E105.bottom", {"start": v(16.87, -34.88) * mm, "end": v(19.69, -34.88) * mm});
            skLineSegment(sketch, "E105.top", {"start": v(16.87, -30.79) * mm, "end": v(19.69, -30.79) * mm});
            skLineSegment(sketch, "E105.left", {"start": v(16.87, -33.4) * mm, "end": v(16.87, -30.79) * mm});
            skLineSegment(sketch, "E105.right", {"start": v(19.69, -34.88) * mm, "end": v(19.69, -30.79) * mm});
            skLineSegment(sketch, "E106.bottom", {"start": v(16.87, -34.88) * mm, "end": v(14.73, -34.88) * mm});
            skLineSegment(sketch, "E106.top", {"start": v(16.87, -33.4) * mm, "end": v(14.73, -33.4) * mm});
            skLineSegment(sketch, "E106.right", {"start": v(14.73, -34.88) * mm, "end": v(14.73, -33.4) * mm});
            skLineSegment(sketch, "E107.top", {"start": v(-31.03, -30.09) * mm, "end": v(-33.6, -30.09) * mm});
            skLineSegment(sketch, "E107.left", {"start": v(-31.03, -31.08) * mm, "end": v(-31.03, -30.09) * mm});
            skLineSegment(sketch, "E107.right", {"start": v(-33.6, -31.08) * mm, "end": v(-33.6, -30.09) * mm});
            skLineSegment(sketch, "E108", {"start": v(5.87, -31.08) * mm, "end": v(5.87, -30.78) * mm});
            skPoint(sketch, "E109.end.orphan", {"position": v(-34.98, -17.16) * mm});
            skPoint(sketch, "E109.start.orphan", {"position": v(-34.98, -16.86) * mm});
            skLineSegment(sketch, "E110.trimOffspring", {"start": v(5.97, -17.16) * mm, "end": v(5.97, -16.86) * mm});
            skLineSegment(sketch, "E111.bottom", {"start": v(5.85, -23.4) * mm, "end": v(18.49, -23.4) * mm});
            skLineSegment(sketch, "E111.top", {"start": v(5.85, -23.7) * mm, "end": v(18.49, -23.7) * mm});
            skLineSegment(sketch, "E111.left", {"start": v(5.85, -23.4) * mm, "end": v(5.85, -23.7) * mm});
            skLineSegment(sketch, "E112", {"start": v(5.29, -31.08) * mm, "end": v(5.29, 2.03) * mm});
            skLineSegment(sketch, "E113", {"start": v(4.99, -31.08) * mm, "end": v(5.29, -31.08) * mm});
            skLineSegment(sketch, "E114", {"start": v(12.44, -30.78) * mm, "end": v(12.44, -31.08) * mm});
            skLineSegment(sketch, "E115", {"start": v(18.49, -16.86) * mm, "end": v(18.49, -17.16) * mm});
            skPoint(sketch, "E116.orphan", {"position": v(19.24, -17.16) * mm});
            skLineSegment(sketch, "E117.trimOffspring", {"start": v(18.49, -23.4) * mm, "end": v(18.49, -23.7) * mm});
            skPoint(sketch, "E118.orphan", {"position": v(19.24, -23.7) * mm});
            skLineSegment(sketch, "E119.trimOffspring", {"start": v(4.99, 2.03) * mm, "end": v(4.99, -31.08) * mm});
            skLineSegment(sketch, "E120", {"start": v(4.99, 2.03) * mm, "end": v(5.29, 2.03) * mm});
            skLineSegment(sketch, "E121.bottom", {"start": v(4.99, 2.73) * mm, "end": v(13.12, 2.73) * mm});
            skLineSegment(sketch, "E121.top", {"start": v(4.99, 6.24) * mm, "end": v(13.12, 6.24) * mm});
            skLineSegment(sketch, "E121.left", {"start": v(4.99, 2.73) * mm, "end": v(4.99, 6.24) * mm});
            skLineSegment(sketch, "E121.right", {"start": v(13.12, 2.73) * mm, "end": v(13.12, 6.24) * mm});
            skCircle(sketch, "E122", {"center": v(8.91, 3.9) * mm, "radius": 1.04 * mm});
            skPoint(sketch, "E122.first.point", {"position": v(8.9, 2.86) * mm});
            skPoint(sketch, "E122.second.point", {"position": v(8.95, 4.94) * mm});
            skPoint(sketch, "E122.third.point", {"position": v(9.95, 3.84) * mm});
            skSolve(sketch);
        }
        {
            var Q0;
            Q0=qSketchRegion(id+"F25",true);
            var Q1;
            Q1=makeQuery(id+"F6.opShell","OFFSET_FACE",FACE,{"disambiguationData":[OSD([sQuery(id+"F2.wireOp",EDGE,"E20"),sQuery(id+"F2.wireOp",EDGE,"E22")])]});
            extrude(context, id + "F26", {"entities" : qUnion([Q0]), "operationType" : NewBodyOperationType.ADD, "endBoundEntityFace" : qUnion([Q1]), "depth" : 7.5 * mm});
        }
        {
            var Q0;
            Q0=qCreatedBy(makeId("Top.planeOp"),FACE);
            var sketch = newSketch(context, id + "F27", { "sketchPlane" : qUnion([Q0])});
            skLineSegment(sketch, "E123", {"start": v(-14.06, 0.58) * mm, "end": v(-9.7, 0.57) * mm});
            skLineSegment(sketch, "E124", {"start": v(-8.04, -3.57) * mm, "end": v(-8.03, -3.84) * mm});
            skLineSegment(sketch, "E125", {"start": v(-8.03, -3.84) * mm, "end": v(-8.04, -13.15) * mm});
            skLineSegment(sketch, "E126", {"start": v(-8.04, -13.15) * mm, "end": v(-8.03, -13.22) * mm});
            skLineSegment(sketch, "E127", {"start": v(-8.03, -13.22) * mm, "end": v(-8.03, -13.28) * mm});
            skLineSegment(sketch, "E128", {"start": v(-8.03, -13.28) * mm, "end": v(-8.04, -13.35) * mm});
            skLineSegment(sketch, "E129", {"start": v(-8.04, -13.35) * mm, "end": v(-8.04, -13.42) * mm});
            skLineSegment(sketch, "E130", {"start": v(-8.04, -13.42) * mm, "end": v(-8.05, -13.48) * mm});
            skLineSegment(sketch, "E131", {"start": v(-8.05, -13.48) * mm, "end": v(-8.06, -13.55) * mm});
            skLineSegment(sketch, "E132", {"start": v(-8.06, -13.55) * mm, "end": v(-8.07, -13.61) * mm});
            skLineSegment(sketch, "E133", {"start": v(-8.07, -13.61) * mm, "end": v(-8.1, -13.68) * mm});
            skLineSegment(sketch, "E134", {"start": v(-8.1, -13.68) * mm, "end": v(-8.1, -13.74) * mm});
            skLineSegment(sketch, "E135", {"start": v(-8.1, -13.74) * mm, "end": v(-8.13, -13.8) * mm});
            skLineSegment(sketch, "E136", {"start": v(-8.13, -13.8) * mm, "end": v(-8.15, -13.86) * mm});
            skLineSegment(sketch, "E137", {"start": v(-8.15, -13.86) * mm, "end": v(-8.18, -13.93) * mm});
            skLineSegment(sketch, "E138", {"start": v(-8.18, -13.93) * mm, "end": v(-8.2, -13.99) * mm});
            skLineSegment(sketch, "E139", {"start": v(-8.2, -13.99) * mm, "end": v(-8.23, -14.05) * mm});
            skLineSegment(sketch, "E140", {"start": v(-8.23, -14.05) * mm, "end": v(-8.26, -14.1) * mm});
            skLineSegment(sketch, "E141", {"start": v(-8.26, -14.1) * mm, "end": v(-8.3, -14.16) * mm});
            skLineSegment(sketch, "E142", {"start": v(-8.3, -14.16) * mm, "end": v(-8.33, -14.22) * mm});
            skLineSegment(sketch, "E143", {"start": v(-8.33, -14.22) * mm, "end": v(-8.37, -14.27) * mm});
            skLineSegment(sketch, "E144", {"start": v(-8.37, -14.27) * mm, "end": v(-8.4, -14.32) * mm});
            skLineSegment(sketch, "E145", {"start": v(-8.4, -14.32) * mm, "end": v(-8.45, -14.37) * mm});
            skLineSegment(sketch, "E146", {"start": v(-8.45, -14.37) * mm, "end": v(-8.5, -14.42) * mm});
            skLineSegment(sketch, "E147", {"start": v(-8.5, -14.42) * mm, "end": v(-8.54, -14.47) * mm});
            skLineSegment(sketch, "E148", {"start": v(-8.54, -14.47) * mm, "end": v(-8.59, -14.52) * mm});
            skLineSegment(sketch, "E149", {"start": v(-8.59, -14.52) * mm, "end": v(-8.63, -14.56) * mm});
            skLineSegment(sketch, "E150", {"start": v(-8.63, -14.56) * mm, "end": v(-8.69, -14.6) * mm});
            skLineSegment(sketch, "E151", {"start": v(-8.69, -14.6) * mm, "end": v(-8.74, -14.64) * mm});
            skLineSegment(sketch, "E152", {"start": v(-8.74, -14.64) * mm, "end": v(-8.8, -14.68) * mm});
            skLineSegment(sketch, "E153", {"start": v(-8.8, -14.68) * mm, "end": v(-8.85, -14.72) * mm});
            skLineSegment(sketch, "E154", {"start": v(-8.85, -14.72) * mm, "end": v(-8.9, -14.75) * mm});
            skLineSegment(sketch, "E155", {"start": v(-8.9, -14.75) * mm, "end": v(-8.95, -14.77) * mm});
            skLineSegment(sketch, "E156", {"start": v(-8.95, -14.77) * mm, "end": v(-8.99, -14.8) * mm});
            skLineSegment(sketch, "E157", {"start": v(-8.99, -14.8) * mm, "end": v(-9.03, -14.81) * mm});
            skLineSegment(sketch, "E158", {"start": v(-9.03, -14.81) * mm, "end": v(-9.07, -14.83) * mm});
            skLineSegment(sketch, "E159", {"start": v(-9.07, -14.83) * mm, "end": v(-9.11, -14.85) * mm});
            skLineSegment(sketch, "E160", {"start": v(-9.11, -14.85) * mm, "end": v(-9.16, -14.86) * mm});
            skLineSegment(sketch, "E161", {"start": v(-9.16, -14.86) * mm, "end": v(-9.2, -14.88) * mm});
            skLineSegment(sketch, "E162", {"start": v(-9.2, -14.88) * mm, "end": v(-9.24, -14.9) * mm});
            skLineSegment(sketch, "E163", {"start": v(-9.24, -14.9) * mm, "end": v(-9.29, -14.9) * mm});
            skLineSegment(sketch, "E164", {"start": v(-9.29, -14.9) * mm, "end": v(-9.33, -14.91) * mm});
            skLineSegment(sketch, "E165", {"start": v(-9.33, -14.91) * mm, "end": v(-9.38, -14.92) * mm});
            skLineSegment(sketch, "E166", {"start": v(-9.38, -14.92) * mm, "end": v(-9.42, -14.93) * mm});
            skLineSegment(sketch, "E167", {"start": v(-9.42, -14.93) * mm, "end": v(-9.51, -14.94) * mm});
            skLineSegment(sketch, "E168", {"start": v(-9.51, -14.94) * mm, "end": v(-9.6, -14.96) * mm});
            skLineSegment(sketch, "E169", {"start": v(-9.6, -14.96) * mm, "end": v(-9.74, -14.97) * mm});
            skLineSegment(sketch, "E170", {"start": v(-9.74, -14.97) * mm, "end": v(-10.2, -14.98) * mm});
            skLineSegment(sketch, "E171", {"start": v(-10.2, -14.98) * mm, "end": v(-23.2, -14.97) * mm});
            skLineSegment(sketch, "E172", {"start": v(-23.2, -14.97) * mm, "end": v(-23.28, -14.97) * mm});
            skLineSegment(sketch, "E173", {"start": v(-23.28, -14.97) * mm, "end": v(-23.35, -14.97) * mm});
            skLineSegment(sketch, "E174", {"start": v(-23.35, -14.97) * mm, "end": v(-23.43, -14.97) * mm});
            skLineSegment(sketch, "E175", {"start": v(-23.43, -14.97) * mm, "end": v(-23.5, -14.96) * mm});
            skLineSegment(sketch, "E176", {"start": v(-23.5, -14.96) * mm, "end": v(-23.58, -14.94) * mm});
            skLineSegment(sketch, "E177", {"start": v(-23.58, -14.94) * mm, "end": v(-23.65, -14.93) * mm});
            skLineSegment(sketch, "E178", {"start": v(-23.65, -14.93) * mm, "end": v(-23.72, -14.9) * mm});
            skLineSegment(sketch, "E179", {"start": v(-23.72, -14.9) * mm, "end": v(-23.8, -14.89) * mm});
            skLineSegment(sketch, "E180", {"start": v(-23.8, -14.89) * mm, "end": v(-23.86, -14.86) * mm});
            skLineSegment(sketch, "E181", {"start": v(-23.86, -14.86) * mm, "end": v(-23.93, -14.83) * mm});
            skLineSegment(sketch, "E182", {"start": v(-23.93, -14.83) * mm, "end": v(-24, -14.8) * mm});
            skLineSegment(sketch, "E183", {"start": v(-24, -14.8) * mm, "end": v(-24.07, -14.77) * mm});
            skLineSegment(sketch, "E184", {"start": v(-24.07, -14.77) * mm, "end": v(-24.13, -14.73) * mm});
            skLineSegment(sketch, "E185", {"start": v(-24.13, -14.73) * mm, "end": v(-24.2, -14.7) * mm});
            skLineSegment(sketch, "E186", {"start": v(-24.2, -14.7) * mm, "end": v(-24.26, -14.65) * mm});
            skLineSegment(sketch, "E187", {"start": v(-24.26, -14.65) * mm, "end": v(-24.32, -14.6) * mm});
            skLineSegment(sketch, "E188", {"start": v(-24.32, -14.6) * mm, "end": v(-24.38, -14.56) * mm});
            skLineSegment(sketch, "E189", {"start": v(-24.38, -14.56) * mm, "end": v(-24.43, -14.51) * mm});
            skLineSegment(sketch, "E190", {"start": v(-24.43, -14.51) * mm, "end": v(-24.48, -14.46) * mm});
            skLineSegment(sketch, "E191", {"start": v(-24.48, -14.46) * mm, "end": v(-24.54, -14.4) * mm});
            skLineSegment(sketch, "E192", {"start": v(-24.54, -14.4) * mm, "end": v(-24.59, -14.35) * mm});
            skLineSegment(sketch, "E193", {"start": v(-24.59, -14.35) * mm, "end": v(-24.63, -14.3) * mm});
            skLineSegment(sketch, "E194", {"start": v(-24.63, -14.3) * mm, "end": v(-24.68, -14.23) * mm});
            skLineSegment(sketch, "E195", {"start": v(-24.68, -14.23) * mm, "end": v(-24.72, -14.17) * mm});
            skLineSegment(sketch, "E196", {"start": v(-24.72, -14.17) * mm, "end": v(-24.76, -14.1) * mm});
            skLineSegment(sketch, "E197", {"start": v(-24.76, -14.1) * mm, "end": v(-24.8, -14.04) * mm});
            skLineSegment(sketch, "E198", {"start": v(-24.8, -14.04) * mm, "end": v(-24.82, -13.97) * mm});
            skLineSegment(sketch, "E199", {"start": v(-24.82, -13.97) * mm, "end": v(-24.85, -13.9) * mm});
            skLineSegment(sketch, "E200", {"start": v(-24.85, -13.9) * mm, "end": v(-24.88, -13.83) * mm});
            skLineSegment(sketch, "E201", {"start": v(-24.88, -13.83) * mm, "end": v(-24.9, -13.76) * mm});
            skLineSegment(sketch, "E202", {"start": v(-24.9, -13.76) * mm, "end": v(-24.92, -13.66) * mm});
            skLineSegment(sketch, "E203", {"start": v(-24.92, -13.66) * mm, "end": v(-24.94, -13.55) * mm});
            skLineSegment(sketch, "E204", {"start": v(-24.94, -13.55) * mm, "end": v(-24.96, -13.38) * mm});
            skLineSegment(sketch, "E205", {"start": v(-24.96, -13.38) * mm, "end": v(-24.98, -12.8) * mm});
            skLineSegment(sketch, "E206", {"start": v(-24.98, -12.8) * mm, "end": v(-24.98, -3.92) * mm});
            skLineSegment(sketch, "E207", {"start": v(-24.98, -3.92) * mm, "end": v(-24.97, -3.38) * mm});
            skLineSegment(sketch, "E208", {"start": v(-24.97, -3.38) * mm, "end": v(-24.96, -3.24) * mm});
            skLineSegment(sketch, "E209", {"start": v(-24.96, -3.24) * mm, "end": v(-24.95, -3.15) * mm});
            skLineSegment(sketch, "E210", {"start": v(-24.95, -3.15) * mm, "end": v(-24.94, -3.1) * mm});
            skLineSegment(sketch, "E211", {"start": v(-24.94, -3.1) * mm, "end": v(-24.93, -3.06) * mm});
            skLineSegment(sketch, "E212", {"start": v(-24.93, -3.06) * mm, "end": v(-24.93, -3.02) * mm});
            skLineSegment(sketch, "E213", {"start": v(-24.93, -3.02) * mm, "end": v(-24.92, -2.97) * mm});
            skLineSegment(sketch, "E214", {"start": v(-24.92, -2.97) * mm, "end": v(-24.9, -2.93) * mm});
            skLineSegment(sketch, "E215", {"start": v(-24.9, -2.93) * mm, "end": v(-24.9, -2.88) * mm});
            skLineSegment(sketch, "E216", {"start": v(-24.9, -2.88) * mm, "end": v(-24.88, -2.84) * mm});
            skLineSegment(sketch, "E217", {"start": v(-24.88, -2.84) * mm, "end": v(-24.87, -2.8) * mm});
            skLineSegment(sketch, "E218", {"start": v(-24.87, -2.8) * mm, "end": v(-24.85, -2.76) * mm});
            skLineSegment(sketch, "E219", {"start": v(-24.85, -2.76) * mm, "end": v(-24.83, -2.71) * mm});
            skLineSegment(sketch, "E220", {"start": v(-24.83, -2.71) * mm, "end": v(-24.81, -2.67) * mm});
            skLineSegment(sketch, "E221", {"start": v(-24.81, -2.67) * mm, "end": v(-24.8, -2.63) * mm});
            skLineSegment(sketch, "E222", {"start": v(-24.8, -2.63) * mm, "end": v(-24.77, -2.58) * mm});
            skLineSegment(sketch, "E223", {"start": v(-24.77, -2.58) * mm, "end": v(-24.74, -2.53) * mm});
            skLineSegment(sketch, "E224", {"start": v(-24.74, -2.53) * mm, "end": v(-24.7, -2.48) * mm});
            skLineSegment(sketch, "E225", {"start": v(-24.7, -2.48) * mm, "end": v(-24.68, -2.43) * mm});
            skLineSegment(sketch, "E226", {"start": v(-24.68, -2.43) * mm, "end": v(-24.64, -2.38) * mm});
            skLineSegment(sketch, "E227", {"start": v(-24.64, -2.38) * mm, "end": v(-24.6, -2.34) * mm});
            skLineSegment(sketch, "E228", {"start": v(-24.6, -2.34) * mm, "end": v(-24.57, -2.3) * mm});
            skLineSegment(sketch, "E229", {"start": v(-24.57, -2.3) * mm, "end": v(-24.53, -2.25) * mm});
            skLineSegment(sketch, "E230", {"start": v(-24.53, -2.25) * mm, "end": v(-24.5, -2.2) * mm});
            skLineSegment(sketch, "E231", {"start": v(-24.5, -2.2) * mm, "end": v(-24.45, -2.16) * mm});
            skLineSegment(sketch, "E232", {"start": v(-24.45, -2.16) * mm, "end": v(-24.41, -2.12) * mm});
            skLineSegment(sketch, "E233", {"start": v(-24.41, -2.12) * mm, "end": v(-24.37, -2.08) * mm});
            skLineSegment(sketch, "E234", {"start": v(-24.37, -2.08) * mm, "end": v(-24.32, -2.05) * mm});
            skLineSegment(sketch, "E235", {"start": v(-24.32, -2.05) * mm, "end": v(-24.28, -2.01) * mm});
            skLineSegment(sketch, "E236", {"start": v(-24.28, -2.01) * mm, "end": v(-24.23, -1.98) * mm});
            skLineSegment(sketch, "E237", {"start": v(-24.23, -1.98) * mm, "end": v(-24.18, -1.94) * mm});
            skLineSegment(sketch, "E238", {"start": v(-24.18, -1.94) * mm, "end": v(-24.13, -1.91) * mm});
            skLineSegment(sketch, "E239", {"start": v(-24.13, -1.91) * mm, "end": v(-24.08, -1.88) * mm});
            skLineSegment(sketch, "E240", {"start": v(-24.08, -1.88) * mm, "end": v(-24.03, -1.86) * mm});
            skLineSegment(sketch, "E241", {"start": v(-24.03, -1.86) * mm, "end": v(-23.98, -1.83) * mm});
            skLineSegment(sketch, "E242", {"start": v(-23.98, -1.83) * mm, "end": v(-23.93, -1.8) * mm});
            skLineSegment(sketch, "E243", {"start": v(-23.93, -1.8) * mm, "end": v(-23.87, -1.79) * mm});
            skLineSegment(sketch, "E244", {"start": v(-23.87, -1.79) * mm, "end": v(-23.82, -1.77) * mm});
            skLineSegment(sketch, "E245", {"start": v(-23.82, -1.77) * mm, "end": v(-23.76, -1.75) * mm});
            skLineSegment(sketch, "E246", {"start": v(-23.76, -1.75) * mm, "end": v(-23.7, -1.73) * mm});
            skLineSegment(sketch, "E247", {"start": v(-23.7, -1.73) * mm, "end": v(-23.65, -1.72) * mm});
            skLineSegment(sketch, "E248", {"start": v(-23.65, -1.72) * mm, "end": v(-23.6, -1.71) * mm});
            skLineSegment(sketch, "E249", {"start": v(-23.6, -1.71) * mm, "end": v(-23.53, -1.7) * mm});
            skLineSegment(sketch, "E250", {"start": v(-23.53, -1.7) * mm, "end": v(-23.48, -1.7) * mm});
            skLineSegment(sketch, "E251", {"start": v(-23.48, -1.7) * mm, "end": v(-23.32, -1.69) * mm});
            skLineSegment(sketch, "E252", {"start": v(-23.32, -1.69) * mm, "end": v(-23.17, -1.68) * mm});
            skLineSegment(sketch, "E253", {"start": v(-23.17, -1.68) * mm, "end": v(-22.95, -1.67) * mm});
            skLineSegment(sketch, "E254", {"start": v(-22.95, -1.67) * mm, "end": v(-21.9, -1.67) * mm});
            skLineSegment(sketch, "E255", {"start": v(-21.9, -1.67) * mm, "end": v(-21.52, -1.67) * mm});
            skLineSegment(sketch, "E256", {"start": v(-21.52, -1.67) * mm, "end": v(-21.3, -1.66) * mm});
            skLineSegment(sketch, "E257", {"start": v(-21.3, -1.66) * mm, "end": v(-21.2, -1.64) * mm});
            skLineSegment(sketch, "E258", {"start": v(-21.2, -1.64) * mm, "end": v(-20.86, -1.5) * mm});
            skLineSegment(sketch, "E259", {"start": v(-20.86, -1.5) * mm, "end": v(-17.7, 0.02) * mm});
            skLineSegment(sketch, "E260", {"start": v(-17.7, 0.02) * mm, "end": v(-17.01, 0.36) * mm});
            skLineSegment(sketch, "E261", {"start": v(-15.75, 0.24) * mm, "end": v(-14.06, -0.59) * mm});
            skLineSegment(sketch, "E262", {"start": v(-14.06, -0.59) * mm, "end": v(-14.06, 0.58) * mm});
            skLineSegment(sketch, "E263", {"start": v(-13.15, -0.33) * mm, "end": v(-13.15, -2.1) * mm});
            skLineSegment(sketch, "E264", {"start": v(-13.15, -2.1) * mm, "end": v(-13.26, -2.06) * mm});
            skLineSegment(sketch, "E265", {"start": v(-13.26, -2.06) * mm, "end": v(-13.9, -1.75) * mm});
            skLineSegment(sketch, "E266", {"start": v(-16.83, -0.6) * mm, "end": v(-17.05, -0.71) * mm});
            skLineSegment(sketch, "E267", {"start": v(-17.05, -0.71) * mm, "end": v(-17.27, -0.83) * mm});
            skLineSegment(sketch, "E268", {"start": v(-17.27, -0.83) * mm, "end": v(-18.4, -1.4) * mm});
            skLineSegment(sketch, "E269", {"start": v(-18.4, -1.4) * mm, "end": v(-22.7, -3.51) * mm});
            skLineSegment(sketch, "E270", {"start": v(-22.7, -3.51) * mm, "end": v(-23.6, -3.97) * mm});
            skLineSegment(sketch, "E271", {"start": v(-23.6, -3.97) * mm, "end": v(-23.64, -4) * mm});
            skLineSegment(sketch, "E272", {"start": v(-23.64, -4) * mm, "end": v(-23.69, -4.02) * mm});
            skLineSegment(sketch, "E273", {"start": v(-23.69, -4.02) * mm, "end": v(-23.73, -4.05) * mm});
            skLineSegment(sketch, "E274", {"start": v(-23.73, -4.05) * mm, "end": v(-23.76, -4.08) * mm});
            skLineSegment(sketch, "E275", {"start": v(-23.76, -4.08) * mm, "end": v(-23.79, -4.1) * mm});
            skLineSegment(sketch, "E276", {"start": v(-23.79, -4.1) * mm, "end": v(-23.8, -4.13) * mm});
            skLineSegment(sketch, "E277", {"start": v(-23.8, -4.13) * mm, "end": v(-23.82, -4.15) * mm});
            skLineSegment(sketch, "E278", {"start": v(-23.82, -4.15) * mm, "end": v(-23.83, -4.16) * mm});
            skLineSegment(sketch, "E279", {"start": v(-23.83, -4.16) * mm, "end": v(-23.83, -4.18) * mm});
            skLineSegment(sketch, "E280", {"start": v(-23.83, -4.18) * mm, "end": v(-23.84, -4.2) * mm});
            skLineSegment(sketch, "E281", {"start": v(-23.84, -4.2) * mm, "end": v(-23.85, -4.21) * mm});
            skLineSegment(sketch, "E282", {"start": v(-23.85, -4.21) * mm, "end": v(-23.85, -4.23) * mm});
            skLineSegment(sketch, "E283", {"start": v(-23.85, -4.23) * mm, "end": v(-23.85, -4.25) * mm});
            skLineSegment(sketch, "E284", {"start": v(-23.85, -4.25) * mm, "end": v(-23.86, -4.27) * mm});
            skLineSegment(sketch, "E285", {"start": v(-23.86, -4.27) * mm, "end": v(-23.86, -4.29) * mm});
            skLineSegment(sketch, "E286", {"start": v(-23.86, -4.29) * mm, "end": v(-23.86, -4.3) * mm});
            skLineSegment(sketch, "E287", {"start": v(-23.86, -4.3) * mm, "end": v(-23.85, -4.32) * mm});
            skLineSegment(sketch, "E288", {"start": v(-23.85, -4.32) * mm, "end": v(-23.85, -4.34) * mm});
            skLineSegment(sketch, "E289", {"start": v(-23.85, -4.34) * mm, "end": v(-23.84, -4.36) * mm});
            skLineSegment(sketch, "E290", {"start": v(-23.84, -4.36) * mm, "end": v(-23.84, -4.38) * mm});
            skLineSegment(sketch, "E291", {"start": v(-23.84, -4.38) * mm, "end": v(-23.83, -4.4) * mm});
            skLineSegment(sketch, "E292", {"start": v(-23.83, -4.4) * mm, "end": v(-23.82, -4.42) * mm});
            skLineSegment(sketch, "E293", {"start": v(-23.82, -4.42) * mm, "end": v(-23.81, -4.44) * mm});
            skLineSegment(sketch, "E294", {"start": v(-23.81, -4.44) * mm, "end": v(-23.8, -4.45) * mm});
            skLineSegment(sketch, "E295", {"start": v(-23.8, -4.45) * mm, "end": v(-23.8, -4.47) * mm});
            skLineSegment(sketch, "E296", {"start": v(-23.8, -4.47) * mm, "end": v(-23.78, -4.48) * mm});
            skLineSegment(sketch, "E297", {"start": v(-23.78, -4.48) * mm, "end": v(-23.76, -4.5) * mm});
            skLineSegment(sketch, "E298", {"start": v(-23.76, -4.5) * mm, "end": v(-23.73, -4.53) * mm});
            skLineSegment(sketch, "E299", {"start": v(-23.73, -4.53) * mm, "end": v(-23.7, -4.55) * mm});
            skLineSegment(sketch, "E300", {"start": v(-23.7, -4.55) * mm, "end": v(-23.58, -4.62) * mm});
            skLineSegment(sketch, "E301", {"start": v(-23.58, -4.62) * mm, "end": v(-23.42, -4.7) * mm});
            skLineSegment(sketch, "E302", {"start": v(-23.42, -4.7) * mm, "end": v(-19.6, -6.6) * mm});
            skLineSegment(sketch, "E303", {"start": v(-19.6, -6.6) * mm, "end": v(-18.6, -7.09) * mm});
            skLineSegment(sketch, "E304", {"start": v(-18.6, -7.09) * mm, "end": v(-17.5, -7.65) * mm});
            skLineSegment(sketch, "E305", {"start": v(-17.5, -7.65) * mm, "end": v(-16.7, -8.03) * mm});
            skLineSegment(sketch, "E306", {"start": v(-16.7, -8.03) * mm, "end": v(-16.68, -8.04) * mm});
            skLineSegment(sketch, "E307", {"start": v(-16.68, -8.04) * mm, "end": v(-16.66, -8.05) * mm});
            skLineSegment(sketch, "E308", {"start": v(-16.66, -8.05) * mm, "end": v(-16.64, -8.06) * mm});
            skLineSegment(sketch, "E309", {"start": v(-16.64, -8.06) * mm, "end": v(-16.62, -8.06) * mm});
            skLineSegment(sketch, "E310", {"start": v(-16.62, -8.06) * mm, "end": v(-16.6, -8.07) * mm});
            skLineSegment(sketch, "E311", {"start": v(-16.6, -8.07) * mm, "end": v(-16.58, -8.07) * mm});
            skLineSegment(sketch, "E312", {"start": v(-16.58, -8.07) * mm, "end": v(-16.56, -8.07) * mm});
            skLineSegment(sketch, "E313", {"start": v(-16.56, -8.07) * mm, "end": v(-16.54, -8.07) * mm});
            skLineSegment(sketch, "E314", {"start": v(-16.54, -8.07) * mm, "end": v(-16.52, -8.08) * mm});
            skLineSegment(sketch, "E315", {"start": v(-16.52, -8.08) * mm, "end": v(-16.48, -8.07) * mm});
            skLineSegment(sketch, "E316", {"start": v(-16.48, -8.07) * mm, "end": v(-16.44, -8.07) * mm});
            skLineSegment(sketch, "E317", {"start": v(-16.44, -8.07) * mm, "end": v(-16.4, -8.06) * mm});
            skLineSegment(sketch, "E318", {"start": v(-16.4, -8.06) * mm, "end": v(-16.32, -8.04) * mm});
            skLineSegment(sketch, "E319", {"start": v(-16.32, -8.04) * mm, "end": v(-16.14, -7.96) * mm});
            skLineSegment(sketch, "E320", {"start": v(-16.14, -7.96) * mm, "end": v(-13.76, -6.78) * mm});
            skLineSegment(sketch, "E321", {"start": v(-13.76, -6.78) * mm, "end": v(-9.85, -4.84) * mm});
            skLineSegment(sketch, "E322", {"start": v(-9.4, -3.99) * mm, "end": v(-9.57, -3.89) * mm});
            skLineSegment(sketch, "E323", {"start": v(-9.57, -3.89) * mm, "end": v(-10.59, -3.4) * mm});
            skLineSegment(sketch, "E324", {"start": v(-10.59, -3.4) * mm, "end": v(-10.6, -0.33) * mm});
            skLineSegment(sketch, "E325", {"start": v(-10.6, -0.33) * mm, "end": v(-13.15, -0.33) * mm});
            skLineSegment(sketch, "E326", {"start": v(-26.34, -4.98) * mm, "end": v(-25.3, -4.97) * mm});
            skLineSegment(sketch, "E327", {"start": v(-25.3, -4.97) * mm, "end": v(-25.28, -6.53) * mm});
            skLineSegment(sketch, "E328", {"start": v(-25.28, -6.53) * mm, "end": v(-26.11, -6.52) * mm});
            skLineSegment(sketch, "E329", {"start": v(-26.11, -6.52) * mm, "end": v(-26.27, -6.5) * mm});
            skLineSegment(sketch, "E330", {"start": v(-26.27, -6.5) * mm, "end": v(-26.38, -6.49) * mm});
            skLineSegment(sketch, "E331", {"start": v(-26.38, -6.49) * mm, "end": v(-26.4, -6.47) * mm});
            skLineSegment(sketch, "E332", {"start": v(-26.4, -6.47) * mm, "end": v(-26.43, -6.45) * mm});
            skLineSegment(sketch, "E333", {"start": v(-26.43, -6.45) * mm, "end": v(-26.45, -6.43) * mm});
            skLineSegment(sketch, "E334", {"start": v(-26.45, -6.43) * mm, "end": v(-26.47, -6.41) * mm});
            skLineSegment(sketch, "E335", {"start": v(-26.47, -6.41) * mm, "end": v(-26.49, -6.39) * mm});
            skLineSegment(sketch, "E336", {"start": v(-26.49, -6.39) * mm, "end": v(-26.5, -6.37) * mm});
            skLineSegment(sketch, "E337", {"start": v(-26.5, -6.37) * mm, "end": v(-26.52, -6.34) * mm});
            skLineSegment(sketch, "E338", {"start": v(-26.52, -6.34) * mm, "end": v(-26.54, -6.32) * mm});
            skLineSegment(sketch, "E339", {"start": v(-26.54, -6.32) * mm, "end": v(-26.55, -6.29) * mm});
            skLineSegment(sketch, "E340", {"start": v(-26.55, -6.29) * mm, "end": v(-26.56, -6.26) * mm});
            skLineSegment(sketch, "E341", {"start": v(-26.56, -6.26) * mm, "end": v(-26.57, -6.23) * mm});
            skLineSegment(sketch, "E342", {"start": v(-26.57, -6.23) * mm, "end": v(-26.58, -6.2) * mm});
            skLineSegment(sketch, "E343", {"start": v(-26.58, -6.2) * mm, "end": v(-26.59, -6.18) * mm});
            skLineSegment(sketch, "E344", {"start": v(-26.59, -6.18) * mm, "end": v(-26.6, -6.15) * mm});
            skLineSegment(sketch, "E345", {"start": v(-26.6, -6.15) * mm, "end": v(-26.6, -6.09) * mm});
            skLineSegment(sketch, "E346", {"start": v(-26.6, -6.09) * mm, "end": v(-26.62, -6.03) * mm});
            skLineSegment(sketch, "E347", {"start": v(-26.62, -6.03) * mm, "end": v(-26.62, -5.9) * mm});
            skLineSegment(sketch, "E348", {"start": v(-26.62, -5.9) * mm, "end": v(-26.63, -5.75) * mm});
            skLineSegment(sketch, "E349", {"start": v(-26.63, -5.75) * mm, "end": v(-26.63, -5.7) * mm});
            skLineSegment(sketch, "E350", {"start": v(-26.63, -5.7) * mm, "end": v(-26.63, -5.62) * mm});
            skLineSegment(sketch, "E351", {"start": v(-26.63, -5.62) * mm, "end": v(-26.62, -5.5) * mm});
            skLineSegment(sketch, "E352", {"start": v(-26.62, -5.5) * mm, "end": v(-26.6, -5.42) * mm});
            skLineSegment(sketch, "E353", {"start": v(-26.6, -5.42) * mm, "end": v(-26.6, -5.36) * mm});
            skLineSegment(sketch, "E354", {"start": v(-26.6, -5.36) * mm, "end": v(-26.58, -5.3) * mm});
            skLineSegment(sketch, "E355", {"start": v(-26.58, -5.3) * mm, "end": v(-26.58, -5.28) * mm});
            skLineSegment(sketch, "E356", {"start": v(-26.58, -5.28) * mm, "end": v(-26.57, -5.25) * mm});
            skLineSegment(sketch, "E357", {"start": v(-26.57, -5.25) * mm, "end": v(-26.56, -5.23) * mm});
            skLineSegment(sketch, "E358", {"start": v(-26.56, -5.23) * mm, "end": v(-26.55, -5.2) * mm});
            skLineSegment(sketch, "E359", {"start": v(-26.55, -5.2) * mm, "end": v(-26.53, -5.18) * mm});
            skLineSegment(sketch, "E360", {"start": v(-26.53, -5.18) * mm, "end": v(-26.52, -5.15) * mm});
            skLineSegment(sketch, "E361", {"start": v(-26.52, -5.15) * mm, "end": v(-26.5, -5.13) * mm});
            skLineSegment(sketch, "E362", {"start": v(-26.5, -5.13) * mm, "end": v(-26.5, -5.1) * mm});
            skLineSegment(sketch, "E363", {"start": v(-26.5, -5.1) * mm, "end": v(-26.47, -5.09) * mm});
            skLineSegment(sketch, "E364", {"start": v(-26.47, -5.09) * mm, "end": v(-26.46, -5.07) * mm});
            skLineSegment(sketch, "E365", {"start": v(-26.46, -5.07) * mm, "end": v(-26.44, -5.05) * mm});
            skLineSegment(sketch, "E366", {"start": v(-26.44, -5.05) * mm, "end": v(-26.42, -5.03) * mm});
            skLineSegment(sketch, "E367", {"start": v(-26.42, -5.03) * mm, "end": v(-26.4, -5.01) * mm});
            skLineSegment(sketch, "E368", {"start": v(-26.4, -5.01) * mm, "end": v(-26.37, -5) * mm});
            skLineSegment(sketch, "E369", {"start": v(-26.37, -5) * mm, "end": v(-26.34, -4.98) * mm});
            skLineSegment(sketch, "E370", {"start": v(-7.72, -4.97) * mm, "end": v(-7.68, -4.98) * mm});
            skLineSegment(sketch, "E371", {"start": v(-7.68, -4.98) * mm, "end": v(-7.64, -4.98) * mm});
            skLineSegment(sketch, "E372", {"start": v(-7.64, -4.98) * mm, "end": v(-7.6, -4.98) * mm});
            skLineSegment(sketch, "E373", {"start": v(-7.6, -4.98) * mm, "end": v(-7.55, -4.98) * mm});
            skLineSegment(sketch, "E374", {"start": v(-7.55, -4.98) * mm, "end": v(-7.5, -4.98) * mm});
            skLineSegment(sketch, "E375", {"start": v(-7.5, -4.98) * mm, "end": v(-7.41, -4.97) * mm});
            skLineSegment(sketch, "E376", {"start": v(-7.41, -4.97) * mm, "end": v(-7.13, -4.95) * mm});
            skLineSegment(sketch, "E377", {"start": v(-7.13, -4.95) * mm, "end": v(-7.09, -4.94) * mm});
            skLineSegment(sketch, "E378", {"start": v(-7.09, -4.94) * mm, "end": v(-7.04, -4.94) * mm});
            skLineSegment(sketch, "E379", {"start": v(-7.04, -4.94) * mm, "end": v(-7, -4.94) * mm});
            skLineSegment(sketch, "E380", {"start": v(-7, -4.94) * mm, "end": v(-6.95, -4.94) * mm});
            skLineSegment(sketch, "E381", {"start": v(-6.95, -4.94) * mm, "end": v(-6.9, -4.94) * mm});
            skLineSegment(sketch, "E382", {"start": v(-6.9, -4.94) * mm, "end": v(-6.86, -4.95) * mm});
            skLineSegment(sketch, "E383", {"start": v(-6.86, -4.95) * mm, "end": v(-6.82, -4.95) * mm});
            skLineSegment(sketch, "E384", {"start": v(-6.82, -4.95) * mm, "end": v(-6.78, -4.96) * mm});
            skLineSegment(sketch, "E385", {"start": v(-6.78, -4.96) * mm, "end": v(-6.74, -4.97) * mm});
            skLineSegment(sketch, "E386", {"start": v(-6.74, -4.97) * mm, "end": v(-6.7, -4.99) * mm});
            skLineSegment(sketch, "E387", {"start": v(-6.7, -4.99) * mm, "end": v(-6.66, -5) * mm});
            skLineSegment(sketch, "E388", {"start": v(-6.66, -5) * mm, "end": v(-6.62, -5.03) * mm});
            skLineSegment(sketch, "E389", {"start": v(-6.62, -5.03) * mm, "end": v(-6.58, -5.05) * mm});
            skLineSegment(sketch, "E390", {"start": v(-6.58, -5.05) * mm, "end": v(-6.55, -5.08) * mm});
            skLineSegment(sketch, "E391", {"start": v(-6.55, -5.08) * mm, "end": v(-6.52, -5.1) * mm});
            skLineSegment(sketch, "E392", {"start": v(-6.52, -5.1) * mm, "end": v(-6.48, -5.14) * mm});
            skLineSegment(sketch, "E393", {"start": v(-6.48, -5.14) * mm, "end": v(-6.47, -5.18) * mm});
            skLineSegment(sketch, "E394", {"start": v(-6.47, -5.18) * mm, "end": v(-6.46, -5.21) * mm});
            skLineSegment(sketch, "E395", {"start": v(-6.46, -5.21) * mm, "end": v(-6.45, -5.24) * mm});
            skLineSegment(sketch, "E396", {"start": v(-6.45, -5.24) * mm, "end": v(-6.43, -5.31) * mm});
            skLineSegment(sketch, "E397", {"start": v(-6.43, -5.31) * mm, "end": v(-6.41, -5.38) * mm});
            skLineSegment(sketch, "E398", {"start": v(-6.41, -5.38) * mm, "end": v(-6.4, -5.45) * mm});
            skLineSegment(sketch, "E399", {"start": v(-6.4, -5.45) * mm, "end": v(-6.4, -5.52) * mm});
            skLineSegment(sketch, "E400", {"start": v(-6.4, -5.52) * mm, "end": v(-6.39, -5.59) * mm});
            skLineSegment(sketch, "E401", {"start": v(-6.39, -5.59) * mm, "end": v(-6.38, -5.7) * mm});
            skLineSegment(sketch, "E402", {"start": v(-6.38, -5.7) * mm, "end": v(-6.39, -5.83) * mm});
            skLineSegment(sketch, "E403", {"start": v(-6.39, -5.83) * mm, "end": v(-6.4, -6.08) * mm});
            skLineSegment(sketch, "E404", {"start": v(-6.4, -6.08) * mm, "end": v(-6.42, -6.15) * mm});
            skLineSegment(sketch, "E405", {"start": v(-6.42, -6.15) * mm, "end": v(-6.47, -6.3) * mm});
            skLineSegment(sketch, "E406", {"start": v(-6.47, -6.3) * mm, "end": v(-6.5, -6.36) * mm});
            skLineSegment(sketch, "E407", {"start": v(-6.5, -6.36) * mm, "end": v(-6.53, -6.4) * mm});
            skLineSegment(sketch, "E408", {"start": v(-6.53, -6.4) * mm, "end": v(-6.56, -6.43) * mm});
            skLineSegment(sketch, "E409", {"start": v(-6.56, -6.43) * mm, "end": v(-6.59, -6.46) * mm});
            skLineSegment(sketch, "E410", {"start": v(-6.59, -6.46) * mm, "end": v(-6.61, -6.47) * mm});
            skLineSegment(sketch, "E411", {"start": v(-6.61, -6.47) * mm, "end": v(-6.64, -6.49) * mm});
            skLineSegment(sketch, "E412", {"start": v(-6.64, -6.49) * mm, "end": v(-6.67, -6.5) * mm});
            skLineSegment(sketch, "E413", {"start": v(-6.67, -6.5) * mm, "end": v(-7.74, -6.53) * mm});
            skLineSegment(sketch, "E414", {"start": v(-7.74, -6.53) * mm, "end": v(-7.72, -4.97) * mm});
            skLineSegment(sketch, "E415", {"start": v(-26.35, -7.32) * mm, "end": v(-25.28, -7.3) * mm});
            skLineSegment(sketch, "E416", {"start": v(-25.28, -7.3) * mm, "end": v(-25.28, -8.87) * mm});
            skLineSegment(sketch, "E417", {"start": v(-25.28, -8.87) * mm, "end": v(-26.35, -8.85) * mm});
            skLineSegment(sketch, "E418", {"start": v(-26.35, -8.85) * mm, "end": v(-26.5, -8.7) * mm});
            skLineSegment(sketch, "E419", {"start": v(-26.5, -8.7) * mm, "end": v(-26.55, -8.62) * mm});
            skLineSegment(sketch, "E420", {"start": v(-26.55, -8.62) * mm, "end": v(-26.57, -8.57) * mm});
            skLineSegment(sketch, "E421", {"start": v(-26.57, -8.57) * mm, "end": v(-26.6, -8.52) * mm});
            skLineSegment(sketch, "E422", {"start": v(-26.6, -8.52) * mm, "end": v(-26.6, -8.47) * mm});
            skLineSegment(sketch, "E423", {"start": v(-26.6, -8.47) * mm, "end": v(-26.6, -8.45) * mm});
            skLineSegment(sketch, "E424", {"start": v(-26.6, -8.45) * mm, "end": v(-26.61, -8.37) * mm});
            skLineSegment(sketch, "E425", {"start": v(-26.61, -8.37) * mm, "end": v(-26.63, -8.2) * mm});
            skLineSegment(sketch, "E426", {"start": v(-26.63, -8.2) * mm, "end": v(-26.63, -8.08) * mm});
            skLineSegment(sketch, "E427", {"start": v(-26.63, -8.08) * mm, "end": v(-26.64, -8) * mm});
            skLineSegment(sketch, "E428", {"start": v(-26.64, -8) * mm, "end": v(-26.64, -7.95) * mm});
            skLineSegment(sketch, "E429", {"start": v(-26.64, -7.95) * mm, "end": v(-26.63, -7.9) * mm});
            skLineSegment(sketch, "E430", {"start": v(-26.63, -7.9) * mm, "end": v(-26.63, -7.86) * mm});
            skLineSegment(sketch, "E431", {"start": v(-26.63, -7.86) * mm, "end": v(-26.63, -7.82) * mm});
            skLineSegment(sketch, "E432", {"start": v(-26.63, -7.82) * mm, "end": v(-26.62, -7.78) * mm});
            skLineSegment(sketch, "E433", {"start": v(-26.62, -7.78) * mm, "end": v(-26.61, -7.74) * mm});
            skLineSegment(sketch, "E434", {"start": v(-26.61, -7.74) * mm, "end": v(-26.6, -7.7) * mm});
            skLineSegment(sketch, "E435", {"start": v(-26.6, -7.7) * mm, "end": v(-26.6, -7.66) * mm});
            skLineSegment(sketch, "E436", {"start": v(-26.6, -7.66) * mm, "end": v(-26.58, -7.62) * mm});
            skLineSegment(sketch, "E437", {"start": v(-26.58, -7.62) * mm, "end": v(-26.56, -7.58) * mm});
            skLineSegment(sketch, "E438", {"start": v(-26.56, -7.58) * mm, "end": v(-26.55, -7.54) * mm});
            skLineSegment(sketch, "E439", {"start": v(-26.55, -7.54) * mm, "end": v(-26.53, -7.5) * mm});
            skLineSegment(sketch, "E440", {"start": v(-26.53, -7.5) * mm, "end": v(-26.5, -7.47) * mm});
            skLineSegment(sketch, "E441", {"start": v(-26.5, -7.47) * mm, "end": v(-26.48, -7.44) * mm});
            skLineSegment(sketch, "E442", {"start": v(-26.48, -7.44) * mm, "end": v(-26.45, -7.4) * mm});
            skLineSegment(sketch, "E443", {"start": v(-26.45, -7.4) * mm, "end": v(-26.42, -7.38) * mm});
            skLineSegment(sketch, "E444", {"start": v(-26.42, -7.38) * mm, "end": v(-26.39, -7.35) * mm});
            skLineSegment(sketch, "E445", {"start": v(-26.39, -7.35) * mm, "end": v(-26.35, -7.32) * mm});
            skLineSegment(sketch, "E446", {"start": v(-7.73, -7.3) * mm, "end": v(-6.66, -7.32) * mm});
            skLineSegment(sketch, "E447", {"start": v(-6.66, -7.32) * mm, "end": v(-6.53, -7.44) * mm});
            skLineSegment(sketch, "E448", {"start": v(-6.53, -7.44) * mm, "end": v(-6.47, -7.53) * mm});
            skLineSegment(sketch, "E449", {"start": v(-6.47, -7.53) * mm, "end": v(-6.44, -7.58) * mm});
            skLineSegment(sketch, "E450", {"start": v(-6.44, -7.58) * mm, "end": v(-6.43, -7.63) * mm});
            skLineSegment(sketch, "E451", {"start": v(-6.43, -7.63) * mm, "end": v(-6.41, -7.68) * mm});
            skLineSegment(sketch, "E452", {"start": v(-6.41, -7.68) * mm, "end": v(-6.4, -7.7) * mm});
            skLineSegment(sketch, "E453", {"start": v(-6.4, -7.7) * mm, "end": v(-6.4, -7.79) * mm});
            skLineSegment(sketch, "E454", {"start": v(-6.4, -7.79) * mm, "end": v(-6.39, -7.96) * mm});
            skLineSegment(sketch, "E455", {"start": v(-6.39, -7.96) * mm, "end": v(-6.38, -8.09) * mm});
            skLineSegment(sketch, "E456", {"start": v(-6.38, -8.09) * mm, "end": v(-6.38, -8.17) * mm});
            skLineSegment(sketch, "E457", {"start": v(-6.38, -8.17) * mm, "end": v(-6.38, -8.22) * mm});
            skLineSegment(sketch, "E458", {"start": v(-6.38, -8.22) * mm, "end": v(-6.38, -8.26) * mm});
            skLineSegment(sketch, "E459", {"start": v(-6.38, -8.26) * mm, "end": v(-6.38, -8.3) * mm});
            skLineSegment(sketch, "E460", {"start": v(-6.38, -8.3) * mm, "end": v(-6.39, -8.34) * mm});
            skLineSegment(sketch, "E461", {"start": v(-6.39, -8.34) * mm, "end": v(-6.4, -8.39) * mm});
            skLineSegment(sketch, "E462", {"start": v(-6.4, -8.39) * mm, "end": v(-6.4, -8.43) * mm});
            skLineSegment(sketch, "E463", {"start": v(-6.4, -8.43) * mm, "end": v(-6.4, -8.47) * mm});
            skLineSegment(sketch, "E464", {"start": v(-6.4, -8.47) * mm, "end": v(-6.42, -8.5) * mm});
            skLineSegment(sketch, "E465", {"start": v(-6.42, -8.5) * mm, "end": v(-6.43, -8.55) * mm});
            skLineSegment(sketch, "E466", {"start": v(-6.43, -8.55) * mm, "end": v(-6.45, -8.58) * mm});
            skLineSegment(sketch, "E467", {"start": v(-6.45, -8.58) * mm, "end": v(-6.47, -8.62) * mm});
            skLineSegment(sketch, "E468", {"start": v(-6.47, -8.62) * mm, "end": v(-6.49, -8.66) * mm});
            skLineSegment(sketch, "E469", {"start": v(-6.49, -8.66) * mm, "end": v(-6.5, -8.7) * mm});
            skLineSegment(sketch, "E470", {"start": v(-6.5, -8.7) * mm, "end": v(-6.53, -8.73) * mm});
            skLineSegment(sketch, "E471", {"start": v(-6.53, -8.73) * mm, "end": v(-6.56, -8.76) * mm});
            skLineSegment(sketch, "E472", {"start": v(-6.56, -8.76) * mm, "end": v(-6.6, -8.79) * mm});
            skLineSegment(sketch, "E473", {"start": v(-6.6, -8.79) * mm, "end": v(-6.62, -8.82) * mm});
            skLineSegment(sketch, "E474", {"start": v(-6.62, -8.82) * mm, "end": v(-6.66, -8.85) * mm});
            skLineSegment(sketch, "E475", {"start": v(-6.66, -8.85) * mm, "end": v(-7.73, -8.87) * mm});
            skLineSegment(sketch, "E476", {"start": v(-7.73, -8.87) * mm, "end": v(-7.73, -7.3) * mm});
            skLineSegment(sketch, "E477", {"start": v(-26.38, -9.67) * mm, "end": v(-26.27, -9.66) * mm});
            skLineSegment(sketch, "E478", {"start": v(-26.27, -9.66) * mm, "end": v(-26.08, -9.64) * mm});
            skLineSegment(sketch, "E479", {"start": v(-26.08, -9.64) * mm, "end": v(-25.28, -9.63) * mm});
            skLineSegment(sketch, "E480", {"start": v(-25.28, -9.63) * mm, "end": v(-25.3, -11.2) * mm});
            skLineSegment(sketch, "E481", {"start": v(-25.3, -11.2) * mm, "end": v(-26.03, -11.2) * mm});
            skLineSegment(sketch, "E482", {"start": v(-26.03, -11.2) * mm, "end": v(-26.17, -11.2) * mm});
            skLineSegment(sketch, "E483", {"start": v(-26.17, -11.2) * mm, "end": v(-26.27, -11.19) * mm});
            skLineSegment(sketch, "E484", {"start": v(-26.27, -11.19) * mm, "end": v(-26.3, -11.18) * mm});
            skLineSegment(sketch, "E485", {"start": v(-26.3, -11.18) * mm, "end": v(-26.34, -11.17) * mm});
            skLineSegment(sketch, "E486", {"start": v(-26.34, -11.17) * mm, "end": v(-26.36, -11.16) * mm});
            skLineSegment(sketch, "E487", {"start": v(-26.36, -11.16) * mm, "end": v(-26.39, -11.15) * mm});
            skLineSegment(sketch, "E488", {"start": v(-26.39, -11.15) * mm, "end": v(-26.41, -11.13) * mm});
            skLineSegment(sketch, "E489", {"start": v(-26.41, -11.13) * mm, "end": v(-26.43, -11.11) * mm});
            skLineSegment(sketch, "E490", {"start": v(-26.43, -11.11) * mm, "end": v(-26.46, -11.1) * mm});
            skLineSegment(sketch, "E491", {"start": v(-26.46, -11.1) * mm, "end": v(-26.47, -11.08) * mm});
            skLineSegment(sketch, "E492", {"start": v(-26.47, -11.08) * mm, "end": v(-26.5, -11.05) * mm});
            skLineSegment(sketch, "E493", {"start": v(-26.5, -11.05) * mm, "end": v(-26.5, -11.03) * mm});
            skLineSegment(sketch, "E494", {"start": v(-26.5, -11.03) * mm, "end": v(-26.52, -11) * mm});
            skLineSegment(sketch, "E495", {"start": v(-26.52, -11) * mm, "end": v(-26.54, -10.98) * mm});
            skLineSegment(sketch, "E496", {"start": v(-26.54, -10.98) * mm, "end": v(-26.55, -10.95) * mm});
            skLineSegment(sketch, "E497", {"start": v(-26.55, -10.95) * mm, "end": v(-26.56, -10.93) * mm});
            skLineSegment(sketch, "E498", {"start": v(-26.56, -10.93) * mm, "end": v(-26.57, -10.9) * mm});
            skLineSegment(sketch, "E499", {"start": v(-26.57, -10.9) * mm, "end": v(-26.58, -10.87) * mm});
            skLineSegment(sketch, "E500", {"start": v(-26.58, -10.87) * mm, "end": v(-26.59, -10.84) * mm});
            skLineSegment(sketch, "E501", {"start": v(-26.59, -10.84) * mm, "end": v(-26.6, -10.78) * mm});
            skLineSegment(sketch, "E502", {"start": v(-26.6, -10.78) * mm, "end": v(-26.61, -10.72) * mm});
            skLineSegment(sketch, "E503", {"start": v(-26.61, -10.72) * mm, "end": v(-26.62, -10.63) * mm});
            skLineSegment(sketch, "E504", {"start": v(-26.62, -10.63) * mm, "end": v(-26.63, -10.55) * mm});
            skLineSegment(sketch, "E505", {"start": v(-26.63, -10.55) * mm, "end": v(-26.63, -10.5) * mm});
            skLineSegment(sketch, "E506", {"start": v(-26.63, -10.5) * mm, "end": v(-26.63, -10.47) * mm});
            skLineSegment(sketch, "E507", {"start": v(-26.63, -10.47) * mm, "end": v(-26.63, -10.38) * mm});
            skLineSegment(sketch, "E508", {"start": v(-26.63, -10.38) * mm, "end": v(-26.62, -10.23) * mm});
            skLineSegment(sketch, "E509", {"start": v(-26.62, -10.23) * mm, "end": v(-26.62, -10.14) * mm});
            skLineSegment(sketch, "E510", {"start": v(-26.62, -10.14) * mm, "end": v(-26.6, -10.08) * mm});
            skLineSegment(sketch, "E511", {"start": v(-26.6, -10.08) * mm, "end": v(-26.6, -10.02) * mm});
            skLineSegment(sketch, "E512", {"start": v(-26.6, -10.02) * mm, "end": v(-26.59, -9.99) * mm});
            skLineSegment(sketch, "E513", {"start": v(-26.59, -9.99) * mm, "end": v(-26.58, -9.96) * mm});
            skLineSegment(sketch, "E514", {"start": v(-26.58, -9.96) * mm, "end": v(-26.57, -9.93) * mm});
            skLineSegment(sketch, "E515", {"start": v(-26.57, -9.93) * mm, "end": v(-26.56, -9.9) * mm});
            skLineSegment(sketch, "E516", {"start": v(-26.56, -9.9) * mm, "end": v(-26.55, -9.87) * mm});
            skLineSegment(sketch, "E517", {"start": v(-26.55, -9.87) * mm, "end": v(-26.54, -9.85) * mm});
            skLineSegment(sketch, "E518", {"start": v(-26.54, -9.85) * mm, "end": v(-26.52, -9.82) * mm});
            skLineSegment(sketch, "E519", {"start": v(-26.52, -9.82) * mm, "end": v(-26.5, -9.8) * mm});
            skLineSegment(sketch, "E520", {"start": v(-26.5, -9.8) * mm, "end": v(-26.49, -9.77) * mm});
            skLineSegment(sketch, "E521", {"start": v(-26.49, -9.77) * mm, "end": v(-26.47, -9.75) * mm});
            skLineSegment(sketch, "E522", {"start": v(-26.47, -9.75) * mm, "end": v(-26.45, -9.73) * mm});
            skLineSegment(sketch, "E523", {"start": v(-26.45, -9.73) * mm, "end": v(-26.43, -9.71) * mm});
            skLineSegment(sketch, "E524", {"start": v(-26.43, -9.71) * mm, "end": v(-26.4, -9.7) * mm});
            skLineSegment(sketch, "E525", {"start": v(-26.4, -9.7) * mm, "end": v(-26.38, -9.67) * mm});
            skLineSegment(sketch, "E526", {"start": v(-7.73, -9.64) * mm, "end": v(-6.54, -9.67) * mm});
            skLineSegment(sketch, "E527", {"start": v(-6.54, -9.67) * mm, "end": v(-6.51, -9.75) * mm});
            skLineSegment(sketch, "E528", {"start": v(-6.51, -9.75) * mm, "end": v(-6.48, -9.83) * mm});
            skLineSegment(sketch, "E529", {"start": v(-6.48, -9.83) * mm, "end": v(-6.46, -9.9) * mm});
            skLineSegment(sketch, "E530", {"start": v(-6.46, -9.9) * mm, "end": v(-6.44, -9.99) * mm});
            skLineSegment(sketch, "E531", {"start": v(-6.44, -9.99) * mm, "end": v(-6.42, -10.07) * mm});
            skLineSegment(sketch, "E532", {"start": v(-6.42, -10.07) * mm, "end": v(-6.4, -10.15) * mm});
            skLineSegment(sketch, "E533", {"start": v(-6.4, -10.15) * mm, "end": v(-6.4, -10.23) * mm});
            skLineSegment(sketch, "E534", {"start": v(-6.4, -10.23) * mm, "end": v(-6.39, -10.32) * mm});
            skLineSegment(sketch, "E535", {"start": v(-6.39, -10.32) * mm, "end": v(-6.38, -10.4) * mm});
            skLineSegment(sketch, "E536", {"start": v(-6.38, -10.4) * mm, "end": v(-6.38, -10.44) * mm});
            skLineSegment(sketch, "E537", {"start": v(-6.38, -10.44) * mm, "end": v(-6.38, -10.48) * mm});
            skLineSegment(sketch, "E538", {"start": v(-6.38, -10.48) * mm, "end": v(-6.38, -10.53) * mm});
            skLineSegment(sketch, "E539", {"start": v(-6.38, -10.53) * mm, "end": v(-6.39, -10.57) * mm});
            skLineSegment(sketch, "E540", {"start": v(-6.39, -10.57) * mm, "end": v(-6.39, -10.6) * mm});
            skLineSegment(sketch, "E541", {"start": v(-6.39, -10.6) * mm, "end": v(-6.4, -10.65) * mm});
            skLineSegment(sketch, "E542", {"start": v(-6.4, -10.65) * mm, "end": v(-6.4, -10.7) * mm});
            skLineSegment(sketch, "E543", {"start": v(-6.4, -10.7) * mm, "end": v(-6.4, -10.73) * mm});
            skLineSegment(sketch, "E544", {"start": v(-6.4, -10.73) * mm, "end": v(-6.41, -10.77) * mm});
            skLineSegment(sketch, "E545", {"start": v(-6.41, -10.77) * mm, "end": v(-6.42, -10.82) * mm});
            skLineSegment(sketch, "E546", {"start": v(-6.42, -10.82) * mm, "end": v(-6.43, -10.86) * mm});
            skLineSegment(sketch, "E547", {"start": v(-6.43, -10.86) * mm, "end": v(-6.45, -10.92) * mm});
            skLineSegment(sketch, "E548", {"start": v(-6.45, -10.92) * mm, "end": v(-6.47, -10.97) * mm});
            skLineSegment(sketch, "E549", {"start": v(-6.47, -10.97) * mm, "end": v(-6.5, -11.03) * mm});
            skLineSegment(sketch, "E550", {"start": v(-6.5, -11.03) * mm, "end": v(-6.53, -11.07) * mm});
            skLineSegment(sketch, "E551", {"start": v(-6.53, -11.07) * mm, "end": v(-6.56, -11.1) * mm});
            skLineSegment(sketch, "E552", {"start": v(-6.56, -11.1) * mm, "end": v(-6.58, -11.12) * mm});
            skLineSegment(sketch, "E553", {"start": v(-6.58, -11.12) * mm, "end": v(-6.6, -11.14) * mm});
            skLineSegment(sketch, "E554", {"start": v(-6.6, -11.14) * mm, "end": v(-6.64, -11.15) * mm});
            skLineSegment(sketch, "E555", {"start": v(-6.64, -11.15) * mm, "end": v(-6.66, -11.17) * mm});
            skLineSegment(sketch, "E556", {"start": v(-6.66, -11.17) * mm, "end": v(-6.7, -11.18) * mm});
            skLineSegment(sketch, "E557", {"start": v(-6.7, -11.18) * mm, "end": v(-6.7, -11.18) * mm});
            skLineSegment(sketch, "E558", {"start": v(-6.7, -11.18) * mm, "end": v(-7.72, -11.2) * mm});
            skLineSegment(sketch, "E559", {"start": v(-7.72, -11.2) * mm, "end": v(-7.73, -9.64) * mm});
            skLineSegment(sketch, "E560", {"start": v(-26.47, -12.01) * mm, "end": v(-25.28, -11.98) * mm});
            skLineSegment(sketch, "E561", {"start": v(-25.28, -11.98) * mm, "end": v(-25.3, -13.53) * mm});
            skLineSegment(sketch, "E562", {"start": v(-25.3, -13.53) * mm, "end": v(-25.33, -13.53) * mm});
            skLineSegment(sketch, "E563", {"start": v(-25.33, -13.53) * mm, "end": v(-25.38, -13.52) * mm});
            skLineSegment(sketch, "E564", {"start": v(-25.38, -13.52) * mm, "end": v(-25.42, -13.52) * mm});
            skLineSegment(sketch, "E565", {"start": v(-25.42, -13.52) * mm, "end": v(-25.47, -13.52) * mm});
            skLineSegment(sketch, "E566", {"start": v(-25.47, -13.52) * mm, "end": v(-25.5, -13.52) * mm});
            skLineSegment(sketch, "E567", {"start": v(-25.5, -13.52) * mm, "end": v(-25.6, -13.53) * mm});
            skLineSegment(sketch, "E568", {"start": v(-25.6, -13.53) * mm, "end": v(-25.88, -13.56) * mm});
            skLineSegment(sketch, "E569", {"start": v(-25.88, -13.56) * mm, "end": v(-25.93, -13.56) * mm});
            skLineSegment(sketch, "E570", {"start": v(-25.93, -13.56) * mm, "end": v(-25.97, -13.56) * mm});
            skLineSegment(sketch, "E571", {"start": v(-25.97, -13.56) * mm, "end": v(-26.02, -13.56) * mm});
            skLineSegment(sketch, "E572", {"start": v(-26.02, -13.56) * mm, "end": v(-26.06, -13.56) * mm});
            skLineSegment(sketch, "E573", {"start": v(-26.06, -13.56) * mm, "end": v(-26.1, -13.56) * mm});
            skLineSegment(sketch, "E574", {"start": v(-26.1, -13.56) * mm, "end": v(-26.15, -13.56) * mm});
            skLineSegment(sketch, "E575", {"start": v(-26.15, -13.56) * mm, "end": v(-26.2, -13.55) * mm});
            skLineSegment(sketch, "E576", {"start": v(-26.2, -13.55) * mm, "end": v(-26.24, -13.54) * mm});
            skLineSegment(sketch, "E577", {"start": v(-26.24, -13.54) * mm, "end": v(-26.28, -13.53) * mm});
            skLineSegment(sketch, "E578", {"start": v(-26.28, -13.53) * mm, "end": v(-26.32, -13.52) * mm});
            skLineSegment(sketch, "E579", {"start": v(-26.32, -13.52) * mm, "end": v(-26.36, -13.5) * mm});
            skLineSegment(sketch, "E580", {"start": v(-26.36, -13.5) * mm, "end": v(-26.4, -13.48) * mm});
            skLineSegment(sketch, "E581", {"start": v(-26.4, -13.48) * mm, "end": v(-26.43, -13.45) * mm});
            skLineSegment(sketch, "E582", {"start": v(-26.43, -13.45) * mm, "end": v(-26.46, -13.43) * mm});
            skLineSegment(sketch, "E583", {"start": v(-26.46, -13.43) * mm, "end": v(-26.5, -13.4) * mm});
            skLineSegment(sketch, "E584", {"start": v(-26.5, -13.4) * mm, "end": v(-26.53, -13.36) * mm});
            skLineSegment(sketch, "E585", {"start": v(-26.53, -13.36) * mm, "end": v(-26.55, -13.31) * mm});
            skLineSegment(sketch, "E586", {"start": v(-26.55, -13.31) * mm, "end": v(-26.56, -13.27) * mm});
            skLineSegment(sketch, "E587", {"start": v(-26.56, -13.27) * mm, "end": v(-26.57, -13.22) * mm});
            skLineSegment(sketch, "E588", {"start": v(-26.57, -13.22) * mm, "end": v(-26.59, -13.18) * mm});
            skLineSegment(sketch, "E589", {"start": v(-26.59, -13.18) * mm, "end": v(-26.6, -13.13) * mm});
            skLineSegment(sketch, "E590", {"start": v(-26.6, -13.13) * mm, "end": v(-26.6, -13.08) * mm});
            skLineSegment(sketch, "E591", {"start": v(-26.6, -13.08) * mm, "end": v(-26.61, -13.04) * mm});
            skLineSegment(sketch, "E592", {"start": v(-26.61, -13.04) * mm, "end": v(-26.62, -12.99) * mm});
            skLineSegment(sketch, "E593", {"start": v(-26.62, -12.99) * mm, "end": v(-26.63, -12.94) * mm});
            skLineSegment(sketch, "E594", {"start": v(-26.63, -12.94) * mm, "end": v(-26.63, -12.9) * mm});
            skLineSegment(sketch, "E595", {"start": v(-26.63, -12.9) * mm, "end": v(-26.63, -12.85) * mm});
            skLineSegment(sketch, "E596", {"start": v(-26.63, -12.85) * mm, "end": v(-26.63, -12.8) * mm});
            skLineSegment(sketch, "E597", {"start": v(-26.63, -12.8) * mm, "end": v(-26.63, -12.75) * mm});
            skLineSegment(sketch, "E598", {"start": v(-26.63, -12.75) * mm, "end": v(-26.63, -12.7) * mm});
            skLineSegment(sketch, "E599", {"start": v(-26.63, -12.7) * mm, "end": v(-26.63, -12.66) * mm});
            skLineSegment(sketch, "E600", {"start": v(-26.63, -12.66) * mm, "end": v(-26.62, -12.6) * mm});
            skLineSegment(sketch, "E601", {"start": v(-26.62, -12.6) * mm, "end": v(-26.62, -12.56) * mm});
            skLineSegment(sketch, "E602", {"start": v(-26.62, -12.56) * mm, "end": v(-26.61, -12.51) * mm});
            skLineSegment(sketch, "E603", {"start": v(-26.61, -12.51) * mm, "end": v(-26.6, -12.47) * mm});
            skLineSegment(sketch, "E604", {"start": v(-26.6, -12.47) * mm, "end": v(-26.6, -12.42) * mm});
            skLineSegment(sketch, "E605", {"start": v(-26.6, -12.42) * mm, "end": v(-26.59, -12.37) * mm});
            skLineSegment(sketch, "E606", {"start": v(-26.59, -12.37) * mm, "end": v(-26.58, -12.33) * mm});
            skLineSegment(sketch, "E607", {"start": v(-26.58, -12.33) * mm, "end": v(-26.56, -12.28) * mm});
            skLineSegment(sketch, "E608", {"start": v(-26.56, -12.28) * mm, "end": v(-26.55, -12.23) * mm});
            skLineSegment(sketch, "E609", {"start": v(-26.55, -12.23) * mm, "end": v(-26.54, -12.19) * mm});
            skLineSegment(sketch, "E610", {"start": v(-26.54, -12.19) * mm, "end": v(-26.52, -12.14) * mm});
            skLineSegment(sketch, "E611", {"start": v(-26.52, -12.14) * mm, "end": v(-26.5, -12.1) * mm});
            skLineSegment(sketch, "E612", {"start": v(-26.5, -12.1) * mm, "end": v(-26.49, -12.05) * mm});
            skLineSegment(sketch, "E613", {"start": v(-26.49, -12.05) * mm, "end": v(-26.47, -12.01) * mm});
            skLineSegment(sketch, "E614", {"start": v(-7.73, -11.98) * mm, "end": v(-6.54, -12.01) * mm});
            skLineSegment(sketch, "E615", {"start": v(-6.54, -12.01) * mm, "end": v(-6.52, -12.06) * mm});
            skLineSegment(sketch, "E616", {"start": v(-6.52, -12.06) * mm, "end": v(-6.5, -12.1) * mm});
            skLineSegment(sketch, "E617", {"start": v(-6.5, -12.1) * mm, "end": v(-6.49, -12.16) * mm});
            skLineSegment(sketch, "E618", {"start": v(-6.49, -12.16) * mm, "end": v(-6.47, -12.2) * mm});
            skLineSegment(sketch, "E619", {"start": v(-6.47, -12.2) * mm, "end": v(-6.46, -12.26) * mm});
            skLineSegment(sketch, "E620", {"start": v(-6.46, -12.26) * mm, "end": v(-6.44, -12.31) * mm});
            skLineSegment(sketch, "E621", {"start": v(-6.44, -12.31) * mm, "end": v(-6.43, -12.37) * mm});
            skLineSegment(sketch, "E622", {"start": v(-6.43, -12.37) * mm, "end": v(-6.42, -12.42) * mm});
            skLineSegment(sketch, "E623", {"start": v(-6.42, -12.42) * mm, "end": v(-6.4, -12.48) * mm});
            skLineSegment(sketch, "E624", {"start": v(-6.4, -12.48) * mm, "end": v(-6.4, -12.53) * mm});
            skLineSegment(sketch, "E625", {"start": v(-6.4, -12.53) * mm, "end": v(-6.39, -12.59) * mm});
            skLineSegment(sketch, "E626", {"start": v(-6.39, -12.59) * mm, "end": v(-6.38, -12.64) * mm});
            skLineSegment(sketch, "E627", {"start": v(-6.38, -12.64) * mm, "end": v(-6.38, -12.7) * mm});
            skLineSegment(sketch, "E628", {"start": v(-6.38, -12.7) * mm, "end": v(-6.37, -12.75) * mm});
            skLineSegment(sketch, "E629", {"start": v(-6.37, -12.75) * mm, "end": v(-6.37, -12.8) * mm});
            skLineSegment(sketch, "E630", {"start": v(-6.37, -12.8) * mm, "end": v(-6.37, -12.86) * mm});
            skLineSegment(sketch, "E631", {"start": v(-6.37, -12.86) * mm, "end": v(-6.38, -12.91) * mm});
            skLineSegment(sketch, "E632", {"start": v(-6.38, -12.91) * mm, "end": v(-6.38, -12.97) * mm});
            skLineSegment(sketch, "E633", {"start": v(-6.38, -12.97) * mm, "end": v(-6.39, -13.02) * mm});
            skLineSegment(sketch, "E634", {"start": v(-6.39, -13.02) * mm, "end": v(-6.4, -13.07) * mm});
            skLineSegment(sketch, "E635", {"start": v(-6.4, -13.07) * mm, "end": v(-6.4, -13.12) * mm});
            skLineSegment(sketch, "E636", {"start": v(-6.4, -13.12) * mm, "end": v(-6.42, -13.17) * mm});
            skLineSegment(sketch, "E637", {"start": v(-6.42, -13.17) * mm, "end": v(-6.44, -13.22) * mm});
            skLineSegment(sketch, "E638", {"start": v(-6.44, -13.22) * mm, "end": v(-6.46, -13.27) * mm});
            skLineSegment(sketch, "E639", {"start": v(-6.46, -13.27) * mm, "end": v(-6.49, -13.32) * mm});
            skLineSegment(sketch, "E640", {"start": v(-6.49, -13.32) * mm, "end": v(-6.51, -13.36) * mm});
            skLineSegment(sketch, "E641", {"start": v(-6.51, -13.36) * mm, "end": v(-6.54, -13.4) * mm});
            skLineSegment(sketch, "E642", {"start": v(-6.54, -13.4) * mm, "end": v(-6.58, -13.45) * mm});
            skLineSegment(sketch, "E643", {"start": v(-6.58, -13.45) * mm, "end": v(-6.61, -13.49) * mm});
            skLineSegment(sketch, "E644", {"start": v(-6.61, -13.49) * mm, "end": v(-6.65, -13.5) * mm});
            skLineSegment(sketch, "E645", {"start": v(-6.65, -13.5) * mm, "end": v(-6.69, -13.5) * mm});
            skLineSegment(sketch, "E646", {"start": v(-6.69, -13.5) * mm, "end": v(-6.72, -13.52) * mm});
            skLineSegment(sketch, "E647", {"start": v(-6.72, -13.52) * mm, "end": v(-6.76, -13.52) * mm});
            skLineSegment(sketch, "E648", {"start": v(-6.76, -13.52) * mm, "end": v(-6.8, -13.53) * mm});
            skLineSegment(sketch, "E649", {"start": v(-6.8, -13.53) * mm, "end": v(-6.87, -13.54) * mm});
            skLineSegment(sketch, "E650", {"start": v(-6.87, -13.54) * mm, "end": v(-6.95, -13.55) * mm});
            skLineSegment(sketch, "E651", {"start": v(-6.95, -13.55) * mm, "end": v(-7.06, -13.55) * mm});
            skLineSegment(sketch, "E652", {"start": v(-7.06, -13.55) * mm, "end": v(-7.6, -13.53) * mm});
            skLineSegment(sketch, "E653", {"start": v(-7.6, -13.53) * mm, "end": v(-7.72, -13.53) * mm});
            skLineSegment(sketch, "E654", {"start": v(-7.72, -13.53) * mm, "end": v(-7.73, -11.98) * mm});
            skLineSegment(sketch, "E655", {"start": v(-20.77, -15.27) * mm, "end": v(-19.21, -15.27) * mm});
            skLineSegment(sketch, "E656", {"start": v(-19.21, -15.27) * mm, "end": v(-19.21, -16.13) * mm});
            skLineSegment(sketch, "E657", {"start": v(-19.21, -16.13) * mm, "end": v(-19.22, -16.27) * mm});
            skLineSegment(sketch, "E658", {"start": v(-19.22, -16.27) * mm, "end": v(-19.23, -16.29) * mm});
            skLineSegment(sketch, "E659", {"start": v(-19.23, -16.29) * mm, "end": v(-19.23, -16.3) * mm});
            skLineSegment(sketch, "E660", {"start": v(-19.23, -16.3) * mm, "end": v(-19.24, -16.32) * mm});
            skLineSegment(sketch, "E661", {"start": v(-19.24, -16.32) * mm, "end": v(-19.24, -16.34) * mm});
            skLineSegment(sketch, "E662", {"start": v(-19.24, -16.34) * mm, "end": v(-19.25, -16.35) * mm});
            skLineSegment(sketch, "E663", {"start": v(-19.25, -16.35) * mm, "end": v(-19.26, -16.37) * mm});
            skLineSegment(sketch, "E664", {"start": v(-19.26, -16.37) * mm, "end": v(-19.27, -16.38) * mm});
            skLineSegment(sketch, "E665", {"start": v(-19.27, -16.38) * mm, "end": v(-19.28, -16.4) * mm});
            skLineSegment(sketch, "E666", {"start": v(-19.28, -16.4) * mm, "end": v(-19.3, -16.41) * mm});
            skLineSegment(sketch, "E667", {"start": v(-19.3, -16.41) * mm, "end": v(-19.32, -16.43) * mm});
            skLineSegment(sketch, "E668", {"start": v(-19.32, -16.43) * mm, "end": v(-19.34, -16.46) * mm});
            skLineSegment(sketch, "E669", {"start": v(-19.34, -16.46) * mm, "end": v(-19.39, -16.49) * mm});
            skLineSegment(sketch, "E670", {"start": v(-19.39, -16.49) * mm, "end": v(-19.47, -16.53) * mm});
            skLineSegment(sketch, "E671", {"start": v(-19.47, -16.53) * mm, "end": v(-19.6, -16.58) * mm});
            skLineSegment(sketch, "E672", {"start": v(-19.6, -16.58) * mm, "end": v(-19.69, -16.6) * mm});
            skLineSegment(sketch, "E673", {"start": v(-19.69, -16.6) * mm, "end": v(-19.73, -16.6) * mm});
            skLineSegment(sketch, "E674", {"start": v(-19.73, -16.6) * mm, "end": v(-19.77, -16.6) * mm});
            skLineSegment(sketch, "E675", {"start": v(-19.77, -16.6) * mm, "end": v(-19.81, -16.61) * mm});
            skLineSegment(sketch, "E676", {"start": v(-19.81, -16.61) * mm, "end": v(-19.86, -16.62) * mm});
            skLineSegment(sketch, "E677", {"start": v(-19.86, -16.62) * mm, "end": v(-19.9, -16.62) * mm});
            skLineSegment(sketch, "E678", {"start": v(-19.9, -16.62) * mm, "end": v(-19.94, -16.62) * mm});
            skLineSegment(sketch, "E679", {"start": v(-19.94, -16.62) * mm, "end": v(-19.98, -16.62) * mm});
            skLineSegment(sketch, "E680", {"start": v(-19.98, -16.62) * mm, "end": v(-20.03, -16.62) * mm});
            skLineSegment(sketch, "E681", {"start": v(-20.03, -16.62) * mm, "end": v(-20.07, -16.62) * mm});
            skLineSegment(sketch, "E682", {"start": v(-20.07, -16.62) * mm, "end": v(-20.11, -16.62) * mm});
            skLineSegment(sketch, "E683", {"start": v(-20.11, -16.62) * mm, "end": v(-20.15, -16.62) * mm});
            skLineSegment(sketch, "E684", {"start": v(-20.15, -16.62) * mm, "end": v(-20.2, -16.61) * mm});
            skLineSegment(sketch, "E685", {"start": v(-20.2, -16.61) * mm, "end": v(-20.24, -16.6) * mm});
            skLineSegment(sketch, "E686", {"start": v(-20.24, -16.6) * mm, "end": v(-20.28, -16.6) * mm});
            skLineSegment(sketch, "E687", {"start": v(-20.28, -16.6) * mm, "end": v(-20.32, -16.6) * mm});
            skLineSegment(sketch, "E688", {"start": v(-20.32, -16.6) * mm, "end": v(-20.36, -16.58) * mm});
            skLineSegment(sketch, "E689", {"start": v(-20.36, -16.58) * mm, "end": v(-20.4, -16.57) * mm});
            skLineSegment(sketch, "E690", {"start": v(-20.4, -16.57) * mm, "end": v(-20.44, -16.56) * mm});
            skLineSegment(sketch, "E691", {"start": v(-20.44, -16.56) * mm, "end": v(-20.48, -16.54) * mm});
            skLineSegment(sketch, "E692", {"start": v(-20.48, -16.54) * mm, "end": v(-20.52, -16.53) * mm});
            skLineSegment(sketch, "E693", {"start": v(-20.52, -16.53) * mm, "end": v(-20.56, -16.51) * mm});
            skLineSegment(sketch, "E694", {"start": v(-20.56, -16.51) * mm, "end": v(-20.6, -16.5) * mm});
            skLineSegment(sketch, "E695", {"start": v(-20.6, -16.5) * mm, "end": v(-20.64, -16.47) * mm});
            skLineSegment(sketch, "E696", {"start": v(-20.64, -16.47) * mm, "end": v(-20.68, -16.45) * mm});
            skLineSegment(sketch, "E697", {"start": v(-20.68, -16.45) * mm, "end": v(-20.71, -16.43) * mm});
            skLineSegment(sketch, "E698", {"start": v(-20.71, -16.43) * mm, "end": v(-20.75, -16.4) * mm});
            skLineSegment(sketch, "E699", {"start": v(-20.75, -16.4) * mm, "end": v(-20.78, -16.38) * mm});
            skLineSegment(sketch, "E700", {"start": v(-20.78, -16.38) * mm, "end": v(-20.77, -15.27) * mm});
            skLineSegment(sketch, "E701", {"start": v(-18.48, -15.27) * mm, "end": v(-16.91, -15.27) * mm});
            skLineSegment(sketch, "E702", {"start": v(-16.91, -15.27) * mm, "end": v(-16.89, -16.15) * mm});
            skLineSegment(sketch, "E703", {"start": v(-16.89, -16.15) * mm, "end": v(-16.9, -16.21) * mm});
            skLineSegment(sketch, "E704", {"start": v(-16.9, -16.21) * mm, "end": v(-16.9, -16.27) * mm});
            skLineSegment(sketch, "E705", {"start": v(-16.9, -16.27) * mm, "end": v(-16.93, -16.32) * mm});
            skLineSegment(sketch, "E706", {"start": v(-16.93, -16.32) * mm, "end": v(-16.96, -16.37) * mm});
            skLineSegment(sketch, "E707", {"start": v(-16.96, -16.37) * mm, "end": v(-17, -16.42) * mm});
            skLineSegment(sketch, "E708", {"start": v(-17, -16.42) * mm, "end": v(-17.02, -16.45) * mm});
            skLineSegment(sketch, "E709", {"start": v(-17.02, -16.45) * mm, "end": v(-17.04, -16.47) * mm});
            skLineSegment(sketch, "E710", {"start": v(-17.04, -16.47) * mm, "end": v(-17.07, -16.5) * mm});
            skLineSegment(sketch, "E711", {"start": v(-17.07, -16.5) * mm, "end": v(-17.1, -16.52) * mm});
            skLineSegment(sketch, "E712", {"start": v(-17.1, -16.52) * mm, "end": v(-17.13, -16.54) * mm});
            skLineSegment(sketch, "E713", {"start": v(-17.13, -16.54) * mm, "end": v(-17.15, -16.55) * mm});
            skLineSegment(sketch, "E714", {"start": v(-17.15, -16.55) * mm, "end": v(-17.17, -16.56) * mm});
            skLineSegment(sketch, "E715", {"start": v(-17.17, -16.56) * mm, "end": v(-17.19, -16.56) * mm});
            skLineSegment(sketch, "E716", {"start": v(-17.19, -16.56) * mm, "end": v(-17.2, -16.57) * mm});
            skLineSegment(sketch, "E717", {"start": v(-17.2, -16.57) * mm, "end": v(-17.22, -16.57) * mm});
            skLineSegment(sketch, "E718", {"start": v(-17.22, -16.57) * mm, "end": v(-17.24, -16.57) * mm});
            skLineSegment(sketch, "E719", {"start": v(-17.24, -16.57) * mm, "end": v(-17.26, -16.58) * mm});
            skLineSegment(sketch, "E720", {"start": v(-17.26, -16.58) * mm, "end": v(-17.3, -16.58) * mm});
            skLineSegment(sketch, "E721", {"start": v(-17.3, -16.58) * mm, "end": v(-17.39, -16.6) * mm});
            skLineSegment(sketch, "E722", {"start": v(-17.39, -16.6) * mm, "end": v(-17.47, -16.61) * mm});
            skLineSegment(sketch, "E723", {"start": v(-17.47, -16.61) * mm, "end": v(-17.56, -16.62) * mm});
            skLineSegment(sketch, "E724", {"start": v(-17.56, -16.62) * mm, "end": v(-17.6, -16.62) * mm});
            skLineSegment(sketch, "E725", {"start": v(-17.6, -16.62) * mm, "end": v(-17.65, -16.63) * mm});
            skLineSegment(sketch, "E726", {"start": v(-17.65, -16.63) * mm, "end": v(-17.7, -16.63) * mm});
            skLineSegment(sketch, "E727", {"start": v(-17.7, -16.63) * mm, "end": v(-17.74, -16.63) * mm});
            skLineSegment(sketch, "E728", {"start": v(-17.74, -16.63) * mm, "end": v(-17.79, -16.63) * mm});
            skLineSegment(sketch, "E729", {"start": v(-17.79, -16.63) * mm, "end": v(-17.83, -16.62) * mm});
            skLineSegment(sketch, "E730", {"start": v(-17.83, -16.62) * mm, "end": v(-17.88, -16.62) * mm});
            skLineSegment(sketch, "E731", {"start": v(-17.88, -16.62) * mm, "end": v(-17.92, -16.61) * mm});
            skLineSegment(sketch, "E732", {"start": v(-17.92, -16.61) * mm, "end": v(-17.96, -16.6) * mm});
            skLineSegment(sketch, "E733", {"start": v(-17.96, -16.6) * mm, "end": v(-18, -16.6) * mm});
            skLineSegment(sketch, "E734", {"start": v(-18, -16.6) * mm, "end": v(-18.05, -16.59) * mm});
            skLineSegment(sketch, "E735", {"start": v(-18.05, -16.59) * mm, "end": v(-18.1, -16.57) * mm});
            skLineSegment(sketch, "E736", {"start": v(-18.1, -16.57) * mm, "end": v(-18.13, -16.56) * mm});
            skLineSegment(sketch, "E737", {"start": v(-18.13, -16.56) * mm, "end": v(-18.17, -16.54) * mm});
            skLineSegment(sketch, "E738", {"start": v(-18.17, -16.54) * mm, "end": v(-18.2, -16.52) * mm});
            skLineSegment(sketch, "E739", {"start": v(-18.2, -16.52) * mm, "end": v(-18.25, -16.5) * mm});
            skLineSegment(sketch, "E740", {"start": v(-18.25, -16.5) * mm, "end": v(-18.28, -16.48) * mm});
            skLineSegment(sketch, "E741", {"start": v(-18.28, -16.48) * mm, "end": v(-18.32, -16.45) * mm});
            skLineSegment(sketch, "E742", {"start": v(-18.32, -16.45) * mm, "end": v(-18.35, -16.42) * mm});
            skLineSegment(sketch, "E743", {"start": v(-18.35, -16.42) * mm, "end": v(-18.38, -16.39) * mm});
            skLineSegment(sketch, "E744", {"start": v(-18.38, -16.39) * mm, "end": v(-18.4, -16.35) * mm});
            skLineSegment(sketch, "E745", {"start": v(-18.4, -16.35) * mm, "end": v(-18.44, -16.32) * mm});
            skLineSegment(sketch, "E746", {"start": v(-18.44, -16.32) * mm, "end": v(-18.45, -16.25) * mm});
            skLineSegment(sketch, "E747", {"start": v(-18.45, -16.25) * mm, "end": v(-18.46, -16.14) * mm});
            skLineSegment(sketch, "E748", {"start": v(-18.46, -16.14) * mm, "end": v(-18.48, -15.96) * mm});
            skLineSegment(sketch, "E749", {"start": v(-18.48, -15.96) * mm, "end": v(-18.48, -15.27) * mm});
            skLineSegment(sketch, "E750", {"start": v(-16.1, -15.27) * mm, "end": v(-14.53, -15.27) * mm});
            skLineSegment(sketch, "E751", {"start": v(-14.53, -15.27) * mm, "end": v(-14.53, -15.99) * mm});
            skLineSegment(sketch, "E752", {"start": v(-14.53, -15.99) * mm, "end": v(-14.54, -16.16) * mm});
            skLineSegment(sketch, "E753", {"start": v(-14.54, -16.16) * mm, "end": v(-14.55, -16.26) * mm});
            skLineSegment(sketch, "E754", {"start": v(-14.55, -16.26) * mm, "end": v(-14.57, -16.3) * mm});
            skLineSegment(sketch, "E755", {"start": v(-14.57, -16.3) * mm, "end": v(-14.59, -16.33) * mm});
            skLineSegment(sketch, "E756", {"start": v(-14.59, -16.33) * mm, "end": v(-14.6, -16.36) * mm});
            skLineSegment(sketch, "E757", {"start": v(-14.6, -16.36) * mm, "end": v(-14.63, -16.38) * mm});
            skLineSegment(sketch, "E758", {"start": v(-14.63, -16.38) * mm, "end": v(-14.65, -16.41) * mm});
            skLineSegment(sketch, "E759", {"start": v(-14.65, -16.41) * mm, "end": v(-14.67, -16.44) * mm});
            skLineSegment(sketch, "E760", {"start": v(-14.67, -16.44) * mm, "end": v(-14.7, -16.46) * mm});
            skLineSegment(sketch, "E761", {"start": v(-14.7, -16.46) * mm, "end": v(-14.73, -16.48) * mm});
            skLineSegment(sketch, "E762", {"start": v(-14.73, -16.48) * mm, "end": v(-14.76, -16.5) * mm});
            skLineSegment(sketch, "E763", {"start": v(-14.76, -16.5) * mm, "end": v(-14.78, -16.52) * mm});
            skLineSegment(sketch, "E764", {"start": v(-14.78, -16.52) * mm, "end": v(-14.82, -16.53) * mm});
            skLineSegment(sketch, "E765", {"start": v(-14.82, -16.53) * mm, "end": v(-14.85, -16.55) * mm});
            skLineSegment(sketch, "E766", {"start": v(-14.85, -16.55) * mm, "end": v(-14.88, -16.56) * mm});
            skLineSegment(sketch, "E767", {"start": v(-14.88, -16.56) * mm, "end": v(-14.91, -16.57) * mm});
            skLineSegment(sketch, "E768", {"start": v(-14.91, -16.57) * mm, "end": v(-14.95, -16.58) * mm});
            skLineSegment(sketch, "E769", {"start": v(-14.95, -16.58) * mm, "end": v(-14.98, -16.59) * mm});
            skLineSegment(sketch, "E770", {"start": v(-14.98, -16.59) * mm, "end": v(-15.02, -16.6) * mm});
            skLineSegment(sketch, "E771", {"start": v(-15.02, -16.6) * mm, "end": v(-15.05, -16.6) * mm});
            skLineSegment(sketch, "E772", {"start": v(-15.05, -16.6) * mm, "end": v(-15.1, -16.6) * mm});
            skLineSegment(sketch, "E773", {"start": v(-15.1, -16.6) * mm, "end": v(-15.16, -16.61) * mm});
            skLineSegment(sketch, "E774", {"start": v(-15.16, -16.61) * mm, "end": v(-15.24, -16.62) * mm});
            skLineSegment(sketch, "E775", {"start": v(-15.24, -16.62) * mm, "end": v(-15.3, -16.62) * mm});
            skLineSegment(sketch, "E776", {"start": v(-15.3, -16.62) * mm, "end": v(-15.38, -16.62) * mm});
            skLineSegment(sketch, "E777", {"start": v(-15.38, -16.62) * mm, "end": v(-15.44, -16.61) * mm});
            skLineSegment(sketch, "E778", {"start": v(-15.44, -16.61) * mm, "end": v(-15.5, -16.62) * mm});
            skLineSegment(sketch, "E779", {"start": v(-15.5, -16.62) * mm, "end": v(-15.55, -16.61) * mm});
            skLineSegment(sketch, "E780", {"start": v(-15.55, -16.61) * mm, "end": v(-15.6, -16.6) * mm});
            skLineSegment(sketch, "E781", {"start": v(-15.6, -16.6) * mm, "end": v(-15.66, -16.6) * mm});
            skLineSegment(sketch, "E782", {"start": v(-15.66, -16.6) * mm, "end": v(-15.71, -16.59) * mm});
            skLineSegment(sketch, "E783", {"start": v(-15.71, -16.59) * mm, "end": v(-15.74, -16.58) * mm});
            skLineSegment(sketch, "E784", {"start": v(-15.74, -16.58) * mm, "end": v(-15.77, -16.57) * mm});
            skLineSegment(sketch, "E785", {"start": v(-15.77, -16.57) * mm, "end": v(-15.8, -16.56) * mm});
            skLineSegment(sketch, "E786", {"start": v(-15.8, -16.56) * mm, "end": v(-15.82, -16.55) * mm});
            skLineSegment(sketch, "E787", {"start": v(-15.82, -16.55) * mm, "end": v(-15.84, -16.54) * mm});
            skLineSegment(sketch, "E788", {"start": v(-15.84, -16.54) * mm, "end": v(-15.87, -16.53) * mm});
            skLineSegment(sketch, "E789", {"start": v(-15.87, -16.53) * mm, "end": v(-15.9, -16.52) * mm});
            skLineSegment(sketch, "E790", {"start": v(-15.9, -16.52) * mm, "end": v(-15.92, -16.5) * mm});
            skLineSegment(sketch, "E791", {"start": v(-15.92, -16.5) * mm, "end": v(-15.94, -16.49) * mm});
            skLineSegment(sketch, "E792", {"start": v(-15.94, -16.49) * mm, "end": v(-15.96, -16.47) * mm});
            skLineSegment(sketch, "E793", {"start": v(-15.96, -16.47) * mm, "end": v(-15.98, -16.46) * mm});
            skLineSegment(sketch, "E794", {"start": v(-15.98, -16.46) * mm, "end": v(-16, -16.44) * mm});
            skLineSegment(sketch, "E795", {"start": v(-16, -16.44) * mm, "end": v(-16.02, -16.42) * mm});
            skLineSegment(sketch, "E796", {"start": v(-16.02, -16.42) * mm, "end": v(-16.04, -16.4) * mm});
            skLineSegment(sketch, "E797", {"start": v(-16.04, -16.4) * mm, "end": v(-16.05, -16.38) * mm});
            skLineSegment(sketch, "E798", {"start": v(-16.05, -16.38) * mm, "end": v(-16.07, -16.35) * mm});
            skLineSegment(sketch, "E799", {"start": v(-16.07, -16.35) * mm, "end": v(-16.08, -16.33) * mm});
            skLineSegment(sketch, "E800", {"start": v(-16.08, -16.33) * mm, "end": v(-16.1, -16.3) * mm});
            skLineSegment(sketch, "E801", {"start": v(-16.1, -16.3) * mm, "end": v(-16.1, -16.28) * mm});
            skLineSegment(sketch, "E802", {"start": v(-16.1, -16.28) * mm, "end": v(-16.12, -16.18) * mm});
            skLineSegment(sketch, "E803", {"start": v(-16.12, -16.18) * mm, "end": v(-16.13, -16.04) * mm});
            skLineSegment(sketch, "E804", {"start": v(-16.13, -16.04) * mm, "end": v(-16.13, -15.76) * mm});
            skLineSegment(sketch, "E805", {"start": v(-16.13, -15.76) * mm, "end": v(-16.1, -15.27) * mm});
            skLineSegment(sketch, "E806", {"start": v(-13.8, -15.27) * mm, "end": v(-12.24, -15.27) * mm});
            skLineSegment(sketch, "E807", {"start": v(-12.24, -15.27) * mm, "end": v(-12.23, -16.38) * mm});
            skLineSegment(sketch, "E808", {"start": v(-12.23, -16.38) * mm, "end": v(-12.27, -16.4) * mm});
            skLineSegment(sketch, "E809", {"start": v(-12.27, -16.4) * mm, "end": v(-12.3, -16.43) * mm});
            skLineSegment(sketch, "E810", {"start": v(-12.3, -16.43) * mm, "end": v(-12.34, -16.45) * mm});
            skLineSegment(sketch, "E811", {"start": v(-12.34, -16.45) * mm, "end": v(-12.38, -16.48) * mm});
            skLineSegment(sketch, "E812", {"start": v(-12.38, -16.48) * mm, "end": v(-12.42, -16.5) * mm});
            skLineSegment(sketch, "E813", {"start": v(-12.42, -16.5) * mm, "end": v(-12.46, -16.51) * mm});
            skLineSegment(sketch, "E814", {"start": v(-12.46, -16.51) * mm, "end": v(-12.5, -16.53) * mm});
            skLineSegment(sketch, "E815", {"start": v(-12.5, -16.53) * mm, "end": v(-12.54, -16.55) * mm});
            skLineSegment(sketch, "E816", {"start": v(-12.54, -16.55) * mm, "end": v(-12.58, -16.56) * mm});
            skLineSegment(sketch, "E817", {"start": v(-12.58, -16.56) * mm, "end": v(-12.62, -16.57) * mm});
            skLineSegment(sketch, "E818", {"start": v(-12.62, -16.57) * mm, "end": v(-12.66, -16.58) * mm});
            skLineSegment(sketch, "E819", {"start": v(-12.66, -16.58) * mm, "end": v(-12.7, -16.6) * mm});
            skLineSegment(sketch, "E820", {"start": v(-12.7, -16.6) * mm, "end": v(-12.75, -16.6) * mm});
            skLineSegment(sketch, "E821", {"start": v(-12.75, -16.6) * mm, "end": v(-12.8, -16.6) * mm});
            skLineSegment(sketch, "E822", {"start": v(-12.8, -16.6) * mm, "end": v(-12.84, -16.61) * mm});
            skLineSegment(sketch, "E823", {"start": v(-12.84, -16.61) * mm, "end": v(-12.88, -16.62) * mm});
            skLineSegment(sketch, "E824", {"start": v(-12.88, -16.62) * mm, "end": v(-12.92, -16.62) * mm});
            skLineSegment(sketch, "E825", {"start": v(-12.92, -16.62) * mm, "end": v(-12.97, -16.62) * mm});
            skLineSegment(sketch, "E826", {"start": v(-12.97, -16.62) * mm, "end": v(-13.01, -16.62) * mm});
            skLineSegment(sketch, "E827", {"start": v(-13.01, -16.62) * mm, "end": v(-13.05, -16.62) * mm});
            skLineSegment(sketch, "E828", {"start": v(-13.05, -16.62) * mm, "end": v(-13.1, -16.62) * mm});
            skLineSegment(sketch, "E829", {"start": v(-13.1, -16.62) * mm, "end": v(-13.14, -16.62) * mm});
            skLineSegment(sketch, "E830", {"start": v(-13.14, -16.62) * mm, "end": v(-13.19, -16.61) * mm});
            skLineSegment(sketch, "E831", {"start": v(-13.19, -16.61) * mm, "end": v(-13.23, -16.6) * mm});
            skLineSegment(sketch, "E832", {"start": v(-13.23, -16.6) * mm, "end": v(-13.27, -16.6) * mm});
            skLineSegment(sketch, "E833", {"start": v(-13.27, -16.6) * mm, "end": v(-13.32, -16.6) * mm});
            skLineSegment(sketch, "E834", {"start": v(-13.32, -16.6) * mm, "end": v(-13.36, -16.59) * mm});
            skLineSegment(sketch, "E835", {"start": v(-13.36, -16.59) * mm, "end": v(-13.4, -16.58) * mm});
            skLineSegment(sketch, "E836", {"start": v(-13.4, -16.58) * mm, "end": v(-13.44, -16.57) * mm});
            skLineSegment(sketch, "E837", {"start": v(-13.44, -16.57) * mm, "end": v(-13.63, -16.48) * mm});
            skLineSegment(sketch, "E838", {"start": v(-13.63, -16.48) * mm, "end": v(-13.67, -16.46) * mm});
            skLineSegment(sketch, "E839", {"start": v(-13.67, -16.46) * mm, "end": v(-13.7, -16.44) * mm});
            skLineSegment(sketch, "E840", {"start": v(-13.7, -16.44) * mm, "end": v(-13.72, -16.42) * mm});
            skLineSegment(sketch, "E841", {"start": v(-13.72, -16.42) * mm, "end": v(-13.74, -16.4) * mm});
            skLineSegment(sketch, "E842", {"start": v(-13.74, -16.4) * mm, "end": v(-13.74, -16.39) * mm});
            skLineSegment(sketch, "E843", {"start": v(-13.74, -16.39) * mm, "end": v(-13.75, -16.37) * mm});
            skLineSegment(sketch, "E844", {"start": v(-13.75, -16.37) * mm, "end": v(-13.76, -16.36) * mm});
            skLineSegment(sketch, "E845", {"start": v(-13.76, -16.36) * mm, "end": v(-13.76, -16.34) * mm});
            skLineSegment(sketch, "E846", {"start": v(-13.76, -16.34) * mm, "end": v(-13.77, -16.33) * mm});
            skLineSegment(sketch, "E847", {"start": v(-13.77, -16.33) * mm, "end": v(-13.77, -16.31) * mm});
            skLineSegment(sketch, "E848", {"start": v(-13.77, -16.31) * mm, "end": v(-13.78, -16.3) * mm});
            skLineSegment(sketch, "E849", {"start": v(-13.78, -16.3) * mm, "end": v(-13.8, -15.27) * mm});
            skFitSpline(sketch, "E850", {"points": [v(-16.09, 0.4) * mm, v(-16.48, 0.53) * mm, v(-16.87, 0.42) * mm], "startDerivative": vector(-0.77, 0.4) * mm, "endDerivative": vector(-0.8, -0.36) * mm});
            skFitSpline(sketch, "E851", {"points": [v(-9.68, -1.66) * mm, v(-8.41, -1.95) * mm, v(-8.04, -3.41) * mm], "startDerivative": vector(3.1, -0.07) * mm, "endDerivative": vector(0.22, -3.4) * mm});
            skLineSegment(sketch, "E852", {"start": v(-8.04, -3.41) * mm, "end": v(-8.04, -3.57) * mm});
            skLineSegment(sketch, "E853", {"start": v(-16.09, 0.4) * mm, "end": v(-15.75, 0.24) * mm});
            skLineSegment(sketch, "E854", {"start": v(-17.01, 0.36) * mm, "end": v(-16.87, 0.42) * mm});
            skLineSegment(sketch, "E855", {"start": v(-9.68, -1.66) * mm, "end": v(-9.7, 0.57) * mm});
            skLineSegment(sketch, "E856", {"start": v(-13.9, -1.75) * mm, "end": v(-16.26, -0.55) * mm});
            skFitSpline(sketch, "E857", {"points": [v(-16.26, -0.55) * mm, v(-16.5, -0.47) * mm, v(-16.83, -0.6) * mm], "startDerivative": vector(-0.52, 0.27) * mm, "endDerivative": vector(-0.63, -0.37) * mm});
            skFitSpline(sketch, "E858", {"points": [v(-9.4, -3.99) * mm, v(-9.18, -4.2) * mm, v(-9.85, -4.84) * mm], "startDerivative": vector(0.88, -0.52) * mm, "endDerivative": vector(-1.57, -1.12) * mm});
            skSolve(sketch);
        }
        {
            var Q0;
            Q0=qSketchRegion(id+"F27",true);
            extrude(context, id + "F28", {"entities" : qUnion([Q0]), "operationType" : NewBodyOperationType.ADD, "depth" : 26.5 * mm});
        }
        {
            var Q0;
            Q0=qSketchRegion(id+"F27",true);
            var Q1;
            {var subQ0=sQuery(id+"F0.wireOp",EDGE,"E7.rect.top");var subQ1=sQuery(id+"F0.wireOp",EDGE,"E7.rect.right");var subQ2=sQuery(id+"F0.wireOp",EDGE,"E7.rect.left");var subQ3=sQuery(id+"F0.wireOp",EDGE,"E7.rect.bottom");var subQ4=sQuery(id+"F0.wireOp",EDGE,"E5.MirrorC");var subQ5=sQuery(id+"F0.wireOp",EDGE,"E3");var subQ6=sQuery(id+"F0.wireOp",EDGE,"E2");var subQ7=sQuery(id+"F0.wireOp",EDGE,"E1");Q1=makeQuery(id+"F28.boolean.opBoolean","SPLIT",FACE,{"disambiguationData":[TD([makeQuery(id+"F28.opExtrude","SWEPT_FACE",FACE,{"disambiguationData":[OSD([sQuery(id+"F27.wireOp",EDGE,"E123")])]})])],"derivedFrom":makeQuery(id+"F6.opShell","OFFSET_FACE",FACE,{"disambiguationData":[OSD([subQ7,subQ6,subQ5,subQ4,subQ3,subQ0,subQ2,subQ1]),TDD([makeQuery(id+"F1.opExtrude","CAP_FACE",FACE,{"disambiguationData":[OSD([subQ7,subQ6,subQ5,subQ4,subQ3,subQ0,subQ2,subQ1])],"isStart":false})])]})});}
            extrude(context, id + "F29", {"entities" : qUnion([Q0]), "operationType" : NewBodyOperationType.REMOVE, "endBound" : BoundingType.UP_TO_SURFACE, "endBoundEntityFace" : qUnion([Q1]), "depth" : 23 * mm});
        }
        {
            var Q0;
            {var subQ0=sQuery(id+"F18.wireOp",EDGE,"E66");Q0=makeQuery(id+"F18.imprint","IMPRINT",FACE,{"disambiguationData":[TD([[makeQuery(id+"F18.imprint","IMPRINT",EDGE,{"derivedFrom":subQ0}),-1.0]])]});}
            extrude(context, id + "F30", {"entities" : qUnion([Q0]), "operationType" : NewBodyOperationType.REMOVE, "oppositeDirection" : true, "depth" : 2 * mm});
        }
        {
            var Q0;
            Q0=qCreatedBy(makeId("Top.planeOp"),FACE);
            var sketch = newSketch(context, id + "F31", { "sketchPlane" : qUnion([Q0])});
            skLineSegment(sketch, "E859.bottom", {"start": v(7.48, -5.58) * mm, "end": v(13.97, -5.58) * mm});
            skLineSegment(sketch, "E859.top", {"start": v(7.48, -5.2) * mm, "end": v(13.97, -5.2) * mm});
            skLineSegment(sketch, "E860.bottom", {"start": v(6.04, -5.58) * mm, "end": v(16.8, -5.58) * mm});
            skLineSegment(sketch, "E860.top", {"start": v(6.04, -5.2) * mm, "end": v(16.8, -5.2) * mm});
            skLineSegment(sketch, "E860.left", {"start": v(6.04, -5.58) * mm, "end": v(6.04, -5.2) * mm});
            skLineSegment(sketch, "E861", {"start": v(16.8, -5.2) * mm, "end": v(18.32, -5.2) * mm});
            skLineSegment(sketch, "E862", {"start": v(18.32, -5.2) * mm, "end": v(18.32, -5.58) * mm});
            skLineSegment(sketch, "E863", {"start": v(18.32, -5.58) * mm, "end": v(16.8, -5.58) * mm});
            skSolve(sketch);
        }
        {
            var Q0;
            Q0=qSketchRegion(id+"F31",true);
            var Q1;
            {var subQ1=sQuery(id+"F2.wireOp",EDGE,"E22");var subQ3=sQuery(id+"F2.wireOp",EDGE,"E20");Q1=makeQuery(id+"F24.boolean.opBoolean","SPLIT",FACE,{"disambiguationData":[TD([makeQuery(id+"F6.opShell","OFFSET_FACE",FACE,{"disambiguationData":[OSD([sQuery(id+"F0.wireOp",EDGE,"E3")])]})])],"derivedFrom":makeQuery(id+"F6.opShell","OFFSET_FACE",FACE,{"disambiguationData":[OSD([subQ3,subQ1])]})});}
            extrude(context, id + "F32", {"entities" : qUnion([Q0]), "operationType" : NewBodyOperationType.ADD, "endBound" : BoundingType.UP_TO_SURFACE, "endBoundEntityFace" : qUnion([Q1]), "depth" : 25 * mm});
        }
        {
            var Q0;
            {var subQ0=sQuery(id+"F0.wireOp",EDGE,"E7.rect.top");var subQ1=sQuery(id+"F0.wireOp",EDGE,"E7.rect.right");var subQ2=sQuery(id+"F0.wireOp",EDGE,"E7.rect.left");var subQ3=sQuery(id+"F0.wireOp",EDGE,"E7.rect.bottom");var subQ4=sQuery(id+"F0.wireOp",EDGE,"E5.MirrorC");var subQ5=sQuery(id+"F0.wireOp",EDGE,"E3");var subQ6=sQuery(id+"F0.wireOp",EDGE,"E2");var subQ7=sQuery(id+"F0.wireOp",EDGE,"E1");Q0=makeQuery(id+"F28.boolean.opBoolean","SPLIT",FACE,{"disambiguationData":[TD([makeQuery(id+"F4.opFillet","BLEND_FACE",FACE,{"disambiguationData":[OSD([subQ0])]})])],"derivedFrom":makeQuery(id+"F1.opExtrude","CAP_FACE",FACE,{"disambiguationData":[OSD([subQ7,subQ6,subQ5,subQ4,subQ3,subQ0,subQ2,subQ1])],"isStart":false})});}
            cPlane(context, id + "F33", {"entities" : qUnion([Q0]), "cplaneType" : CPlaneType.OFFSET, "offset" : 9 * mm, "oppositeDirection" : true, "width" : 150 * mm, "height" : 150 * mm});
        }
        {
            var Q0;
            Q0=qCreatedBy(id+"F33.planeOp",FACE);
            var sketch = newSketch(context, id + "F34", { "sketchPlane" : qUnion([Q0])});
            skCircle(sketch, "E864", {"center": v(-29.86, -30.9) * mm, "radius": 1.22 * mm});
            skCircle(sketch, "E865", {"center": v(-29.84, 14.65) * mm, "radius": 1.25 * mm});
            skSolve(sketch);
        }
        {
            var Q0;
            Q0=qSketchRegion(id+"F34",true);
            var Q1;
            Q1=makeQuery(id+"F3.boolean.opBoolean","COPY",FACE,{"derivedFrom":makeQuery(id+"F3.opExtrude","SWEPT_FACE",FACE,{"disambiguationData":[OSD([sQuery(id+"F2.wireOp",EDGE,"E14")])]})});
            extrude(context, id + "F35", {"entities" : qUnion([Q0]), "operationType" : NewBodyOperationType.ADD, "endBound" : BoundingType.UP_TO_SURFACE, "endBoundEntityFace" : qUnion([Q1]), "depth" : 25 * mm});
        }
        {
            var Q0;
            {var subQ0=sQuery(id+"F0.wireOp",EDGE,"E7.rect.right");var subQ1=sQuery(id+"F0.wireOp",EDGE,"E7.rect.left");var subQ2=sQuery(id+"F0.wireOp",EDGE,"E7.rect.top");var subQ3=sQuery(id+"F0.wireOp",EDGE,"E7.rect.bottom");var subQ4=sQuery(id+"F0.wireOp",EDGE,"E5.MirrorC");var subQ5=sQuery(id+"F0.wireOp",EDGE,"E3");var subQ6=sQuery(id+"F0.wireOp",EDGE,"E2");var subQ7=sQuery(id+"F0.wireOp",EDGE,"E1");Q0=makeQuery(id+"F28.boolean.opBoolean","SPLIT",FACE,{"disambiguationData":[TD([makeQuery(id+"F4.opFillet","BLEND_FACE",FACE,{"disambiguationData":[OSD([subQ3])]})])],"derivedFrom":makeQuery(id+"F1.opExtrude","CAP_FACE",FACE,{"disambiguationData":[OSD([subQ7,subQ6,subQ5,subQ4,subQ3,subQ2,subQ1,subQ0])],"isStart":false})});}
            cPlane(context, id + "F36", {"entities" : qUnion([Q0]), "cplaneType" : CPlaneType.OFFSET, "offset" : 17.5 * mm, "oppositeDirection" : true, "width" : 150 * mm, "height" : 150 * mm});
        }
        {
            var Q0;
            Q0=qCreatedBy(id+"F36.planeOp",FACE);
            var sketch = newSketch(context, id + "F37", { "sketchPlane" : qUnion([Q0])});
            skCircle(sketch, "E866", {"center": v(8.9, 3.98) * mm, "radius": 1.26 * mm});
            skCircle(sketch, "E867", {"center": v(15.8, -30.92) * mm, "radius": 1.17 * mm});
            skSolve(sketch);
        }
        {
            var Q0;
            Q0=qSketchRegion(id+"F37",true);
            var Q1;
            {var subQ0=sQuery(id+"F2.wireOp",EDGE,"E22");var subQ1=sQuery(id+"F2.wireOp",EDGE,"E20");Q1=makeQuery(id+"F24.boolean.opBoolean","SPLIT",FACE,{"disambiguationData":[TD([makeQuery(id+"F1.opExtrude","SWEPT_FACE",FACE,{"disambiguationData":[OSD([sQuery(id+"F0.wireOp",EDGE,"E3")])]})])],"derivedFrom":makeQuery(id+"F3.boolean.opBoolean","COPY",FACE,{"derivedFrom":makeQuery(id+"F3.opExtrude","SWEPT_FACE",FACE,{"disambiguationData":[OSD([subQ1,subQ0])]})})});}
            extrude(context, id + "F38", {"entities" : qUnion([Q0]), "operationType" : NewBodyOperationType.ADD, "endBound" : BoundingType.UP_TO_SURFACE, "endBoundEntityFace" : qUnion([Q1]), "depth" : 25 * mm});
        }
        {
            var Q0;
            Q0=makeQuery(id+"F1.opExtrude","SWEPT_FACE",FACE,{"disambiguationData":[OSD([sQuery(id+"F0.wireOp",EDGE,"E7.rect.bottom")])]});
            cPlane(context, id + "F39", {"entities" : qUnion([Q0]), "cplaneType" : CPlaneType.OFFSET, "offset" : 1.8 * mm, "oppositeDirection" : true, "width" : 150 * mm, "height" : 150 * mm});
        }
        {
            var Q0;
            Q0=qCreatedBy(id+"F39.planeOp",FACE);
            var sketch = newSketch(context, id + "F40", { "sketchPlane" : qUnion([Q0])});
            skLineSegment(sketch, "E868.top", {"start": v(-5.27, 0) * mm, "end": v(12.86, 0) * mm});
            skLineSegment(sketch, "E869.right", {"start": v(12.86, 5.48) * mm, "end": v(12.86, 0) * mm});
            skLineSegment(sketch, "E870.bottom", {"start": v(12.86, 0) * mm, "end": v(-5.27, 0) * mm});
            skLineSegment(sketch, "E870.top", {"start": v(12.86, 5.48) * mm, "end": v(-5.27, 5.48) * mm});
            skLineSegment(sketch, "E870.left", {"start": v(12.86, 0) * mm, "end": v(12.86, 5.48) * mm});
            skPoint(sketch, "E871.orphan", {"position": v(14.06, 0) * mm});
            skLineSegment(sketch, "E872", {"start": v(-5.27, 5.48) * mm, "end": v(-8, 5.48) * mm});
            skLineSegment(sketch, "E873", {"start": v(-8, 5.48) * mm, "end": v(-8, 0) * mm});
            skLineSegment(sketch, "E874", {"start": v(-8, 0) * mm, "end": v(-5.27, 0) * mm});
            skSolve(sketch);
        }
        {
            var Q0;
            Q0=qSketchRegion(id+"F40",true);
            extrude(context, id + "F41", {"entities" : qUnion([Q0]), "operationType" : NewBodyOperationType.REMOVE, "depth" : 1.2 * mm});
        }
        {
            var Q0;
            Q0=qCreatedBy(makeId("Top.planeOp"),FACE);
            var sketch = newSketch(context, id + "F42", { "sketchPlane" : qUnion([Q0])});
            skLineSegment(sketch, "E875.bottom", {"start": v(-10.2, -20.34) * mm, "end": v(-23.5, -20.34) * mm});
            skLineSegment(sketch, "E875.top", {"start": v(-9.76, -20.7) * mm, "end": v(-23.91, -20.7) * mm});
            skLineSegment(sketch, "E875.left", {"start": v(-9.76, -20.34) * mm, "end": v(-9.76, -20.7) * mm});
            skLineSegment(sketch, "E876", {"start": v(-9.76, -19.58) * mm, "end": v(-9.76, 2.28) * mm});
            skLineSegment(sketch, "E877.bottom", {"start": v(-10.2, 2.28) * mm, "end": v(-23.5, 2.28) * mm});
            skLineSegment(sketch, "E877.top", {"start": v(-9.76, 2.58) * mm, "end": v(-23.91, 2.58) * mm});
            skLineSegment(sketch, "E877.left", {"start": v(-9.76, 2.28) * mm, "end": v(-9.76, 2.58) * mm});
            skLineSegment(sketch, "E877.right", {"start": v(-23.91, 2.28) * mm, "end": v(-23.91, 2.58) * mm});
            skLineSegment(sketch, "E878.bottom", {"start": v(-10.2, -10.06) * mm, "end": v(-23.5, -10.06) * mm});
            skLineSegment(sketch, "E878.top", {"start": v(-10.2, -9.35) * mm, "end": v(-23.5, -9.35) * mm});
            skLineSegment(sketch, "E878.left", {"start": v(-9.76, -10.06) * mm, "end": v(-9.76, -9.35) * mm});
            skLineSegment(sketch, "E878.right", {"start": v(-25.9, -10.06) * mm, "end": v(-25.9, -9.35) * mm});
            skLineSegment(sketch, "E879", {"start": v(-10.2, -19.58) * mm, "end": v(-10.2, -10.06) * mm});
            skLineSegment(sketch, "E880.bottom", {"start": v(-23.91, 2.58) * mm, "end": v(-23.5, 2.58) * mm});
            skLineSegment(sketch, "E880.top", {"start": v(-23.91, -20.7) * mm, "end": v(-23.5, -20.7) * mm});
            skLineSegment(sketch, "E880.left", {"start": v(-23.91, 2.58) * mm, "end": v(-23.91, 2.28) * mm});
            skLineSegment(sketch, "E880.right", {"start": v(-23.5, 1.67) * mm, "end": v(-23.5, -9.35) * mm});
            skLineSegment(sketch, "E881.trimOffspring", {"start": v(-10.2, -9.35) * mm, "end": v(-10.2, 2.28) * mm});
            skLineSegment(sketch, "E882.trimOffspring", {"start": v(-23.91, -10.06) * mm, "end": v(-25.9, -10.06) * mm});
            skLineSegment(sketch, "E883.trimOffspring", {"start": v(-23.91, -10.06) * mm, "end": v(-23.91, -20.7) * mm});
            skLineSegment(sketch, "E884.trimOffspring", {"start": v(-23.5, -10.06) * mm, "end": v(-23.5, -20.34) * mm});
            skLineSegment(sketch, "E885.trimOffspring", {"start": v(-23.91, -9.35) * mm, "end": v(-25.9, -9.35) * mm});
            skLineSegment(sketch, "E886", {"start": v(-10.2, -19.58) * mm, "end": v(-9.76, -19.58) * mm});
            skLineSegment(sketch, "E887", {"start": v(-10.2, -20.34) * mm, "end": v(-9.76, -20.34) * mm});
            skLineSegment(sketch, "E888", {"start": v(-23.5, 2.28) * mm, "end": v(-23.91, 2.28) * mm});
            skLineSegment(sketch, "E889", {"start": v(-23.5, 1.67) * mm, "end": v(-23.91, 1.67) * mm});
            skLineSegment(sketch, "E890.trimOffspring", {"start": v(-23.91, 1.67) * mm, "end": v(-23.91, -9.35) * mm});
            skSolve(sketch);
        }
        {
            var Q0;
            Q0=qSketchRegion(id+"F42",true);
            var Q1;
            {var subQ0=sQuery(id+"F27.wireOp",EDGE,"E849");var subQ1=sQuery(id+"F27.wireOp",EDGE,"E848");var subQ2=sQuery(id+"F27.wireOp",EDGE,"E847");var subQ3=sQuery(id+"F27.wireOp",EDGE,"E846");var subQ4=sQuery(id+"F27.wireOp",EDGE,"E845");var subQ5=sQuery(id+"F27.wireOp",EDGE,"E844");var subQ6=sQuery(id+"F27.wireOp",EDGE,"E843");var subQ7=sQuery(id+"F27.wireOp",EDGE,"E842");var subQ8=sQuery(id+"F27.wireOp",EDGE,"E841");var subQ9=sQuery(id+"F27.wireOp",EDGE,"E840");var subQ10=sQuery(id+"F27.wireOp",EDGE,"E839");var subQ11=sQuery(id+"F27.wireOp",EDGE,"E838");var subQ12=sQuery(id+"F27.wireOp",EDGE,"E837");var subQ13=sQuery(id+"F27.wireOp",EDGE,"E836");var subQ14=sQuery(id+"F27.wireOp",EDGE,"E835");var subQ15=sQuery(id+"F27.wireOp",EDGE,"E834");var subQ16=sQuery(id+"F27.wireOp",EDGE,"E833");var subQ17=sQuery(id+"F27.wireOp",EDGE,"E832");var subQ18=sQuery(id+"F27.wireOp",EDGE,"E831");var subQ19=sQuery(id+"F27.wireOp",EDGE,"E830");var subQ20=sQuery(id+"F27.wireOp",EDGE,"E829");var subQ21=sQuery(id+"F27.wireOp",EDGE,"E828");var subQ22=sQuery(id+"F27.wireOp",EDGE,"E827");var subQ23=sQuery(id+"F27.wireOp",EDGE,"E826");var subQ24=sQuery(id+"F27.wireOp",EDGE,"E825");var subQ25=sQuery(id+"F27.wireOp",EDGE,"E824");var subQ26=sQuery(id+"F27.wireOp",EDGE,"E823");var subQ27=sQuery(id+"F27.wireOp",EDGE,"E822");var subQ28=sQuery(id+"F27.wireOp",EDGE,"E821");var subQ29=sQuery(id+"F27.wireOp",EDGE,"E820");var subQ30=sQuery(id+"F27.wireOp",EDGE,"E819");var subQ31=sQuery(id+"F27.wireOp",EDGE,"E818");var subQ32=sQuery(id+"F27.wireOp",EDGE,"E817");var subQ33=sQuery(id+"F27.wireOp",EDGE,"E816");var subQ34=sQuery(id+"F27.wireOp",EDGE,"E815");var subQ35=sQuery(id+"F27.wireOp",EDGE,"E814");var subQ36=sQuery(id+"F27.wireOp",EDGE,"E813");var subQ37=sQuery(id+"F27.wireOp",EDGE,"E812");var subQ38=sQuery(id+"F27.wireOp",EDGE,"E811");var subQ39=sQuery(id+"F27.wireOp",EDGE,"E810");var subQ40=sQuery(id+"F27.wireOp",EDGE,"E809");var subQ41=sQuery(id+"F27.wireOp",EDGE,"E808");var subQ42=sQuery(id+"F27.wireOp",EDGE,"E807");var subQ43=sQuery(id+"F27.wireOp",EDGE,"E806");var subQ44=sQuery(id+"F27.wireOp",EDGE,"E805");var subQ45=sQuery(id+"F27.wireOp",EDGE,"E804");var subQ46=sQuery(id+"F27.wireOp",EDGE,"E803");var subQ47=sQuery(id+"F27.wireOp",EDGE,"E802");var subQ48=sQuery(id+"F27.wireOp",EDGE,"E801");var subQ49=sQuery(id+"F27.wireOp",EDGE,"E800");var subQ50=sQuery(id+"F27.wireOp",EDGE,"E799");var subQ51=sQuery(id+"F27.wireOp",EDGE,"E798");var subQ52=sQuery(id+"F27.wireOp",EDGE,"E797");var subQ53=sQuery(id+"F27.wireOp",EDGE,"E796");var subQ54=sQuery(id+"F27.wireOp",EDGE,"E795");var subQ55=sQuery(id+"F27.wireOp",EDGE,"E794");var subQ56=sQuery(id+"F27.wireOp",EDGE,"E793");var subQ57=sQuery(id+"F27.wireOp",EDGE,"E792");var subQ58=sQuery(id+"F27.wireOp",EDGE,"E791");var subQ59=sQuery(id+"F27.wireOp",EDGE,"E790");var subQ60=sQuery(id+"F27.wireOp",EDGE,"E789");var subQ61=sQuery(id+"F27.wireOp",EDGE,"E788");var subQ62=sQuery(id+"F27.wireOp",EDGE,"E787");var subQ63=sQuery(id+"F27.wireOp",EDGE,"E786");var subQ64=sQuery(id+"F27.wireOp",EDGE,"E785");var subQ65=sQuery(id+"F27.wireOp",EDGE,"E784");var subQ66=sQuery(id+"F27.wireOp",EDGE,"E783");var subQ67=sQuery(id+"F27.wireOp",EDGE,"E782");var subQ68=sQuery(id+"F27.wireOp",EDGE,"E781");var subQ69=sQuery(id+"F27.wireOp",EDGE,"E780");var subQ70=sQuery(id+"F27.wireOp",EDGE,"E779");var subQ71=sQuery(id+"F27.wireOp",EDGE,"E778");var subQ72=sQuery(id+"F27.wireOp",EDGE,"E777");var subQ73=sQuery(id+"F27.wireOp",EDGE,"E776");var subQ74=sQuery(id+"F27.wireOp",EDGE,"E775");var subQ75=sQuery(id+"F27.wireOp",EDGE,"E774");var subQ76=sQuery(id+"F27.wireOp",EDGE,"E773");var subQ77=sQuery(id+"F27.wireOp",EDGE,"E772");var subQ78=sQuery(id+"F27.wireOp",EDGE,"E771");var subQ79=sQuery(id+"F27.wireOp",EDGE,"E770");var subQ80=sQuery(id+"F27.wireOp",EDGE,"E769");var subQ81=sQuery(id+"F27.wireOp",EDGE,"E768");var subQ82=sQuery(id+"F27.wireOp",EDGE,"E767");var subQ83=sQuery(id+"F27.wireOp",EDGE,"E766");var subQ84=sQuery(id+"F27.wireOp",EDGE,"E765");var subQ85=sQuery(id+"F27.wireOp",EDGE,"E764");var subQ86=sQuery(id+"F27.wireOp",EDGE,"E763");var subQ87=sQuery(id+"F27.wireOp",EDGE,"E762");var subQ88=sQuery(id+"F27.wireOp",EDGE,"E761");var subQ89=sQuery(id+"F27.wireOp",EDGE,"E760");var subQ90=sQuery(id+"F27.wireOp",EDGE,"E759");var subQ91=sQuery(id+"F27.wireOp",EDGE,"E758");var subQ92=sQuery(id+"F27.wireOp",EDGE,"E757");var subQ93=sQuery(id+"F27.wireOp",EDGE,"E756");var subQ94=sQuery(id+"F27.wireOp",EDGE,"E755");var subQ95=sQuery(id+"F27.wireOp",EDGE,"E754");var subQ96=sQuery(id+"F27.wireOp",EDGE,"E753");var subQ97=sQuery(id+"F27.wireOp",EDGE,"E752");var subQ98=sQuery(id+"F27.wireOp",EDGE,"E751");var subQ99=sQuery(id+"F27.wireOp",EDGE,"E750");var subQ100=sQuery(id+"F27.wireOp",EDGE,"E749");var subQ101=sQuery(id+"F27.wireOp",EDGE,"E748");var subQ102=sQuery(id+"F27.wireOp",EDGE,"E747");var subQ103=sQuery(id+"F27.wireOp",EDGE,"E746");var subQ104=sQuery(id+"F27.wireOp",EDGE,"E745");var subQ105=sQuery(id+"F27.wireOp",EDGE,"E744");var subQ106=sQuery(id+"F27.wireOp",EDGE,"E743");var subQ107=sQuery(id+"F27.wireOp",EDGE,"E742");var subQ108=sQuery(id+"F27.wireOp",EDGE,"E741");var subQ109=sQuery(id+"F27.wireOp",EDGE,"E740");var subQ110=sQuery(id+"F27.wireOp",EDGE,"E739");var subQ111=sQuery(id+"F27.wireOp",EDGE,"E738");var subQ112=sQuery(id+"F27.wireOp",EDGE,"E737");var subQ113=sQuery(id+"F27.wireOp",EDGE,"E736");var subQ114=sQuery(id+"F27.wireOp",EDGE,"E735");var subQ115=sQuery(id+"F27.wireOp",EDGE,"E734");var subQ116=sQuery(id+"F27.wireOp",EDGE,"E733");var subQ117=sQuery(id+"F27.wireOp",EDGE,"E732");var subQ118=sQuery(id+"F27.wireOp",EDGE,"E731");var subQ119=sQuery(id+"F27.wireOp",EDGE,"E730");var subQ120=sQuery(id+"F27.wireOp",EDGE,"E729");var subQ121=sQuery(id+"F27.wireOp",EDGE,"E728");var subQ122=sQuery(id+"F27.wireOp",EDGE,"E727");var subQ123=sQuery(id+"F27.wireOp",EDGE,"E726");var subQ124=sQuery(id+"F27.wireOp",EDGE,"E725");var subQ125=sQuery(id+"F27.wireOp",EDGE,"E724");var subQ126=sQuery(id+"F27.wireOp",EDGE,"E723");var subQ127=sQuery(id+"F27.wireOp",EDGE,"E722");var subQ128=sQuery(id+"F27.wireOp",EDGE,"E721");var subQ129=sQuery(id+"F27.wireOp",EDGE,"E720");var subQ130=sQuery(id+"F27.wireOp",EDGE,"E719");var subQ131=sQuery(id+"F27.wireOp",EDGE,"E718");var subQ132=sQuery(id+"F27.wireOp",EDGE,"E717");var subQ133=sQuery(id+"F27.wireOp",EDGE,"E716");var subQ134=sQuery(id+"F27.wireOp",EDGE,"E715");var subQ135=sQuery(id+"F27.wireOp",EDGE,"E714");var subQ136=sQuery(id+"F27.wireOp",EDGE,"E713");var subQ137=sQuery(id+"F27.wireOp",EDGE,"E712");var subQ138=sQuery(id+"F27.wireOp",EDGE,"E711");var subQ139=sQuery(id+"F27.wireOp",EDGE,"E710");var subQ140=sQuery(id+"F27.wireOp",EDGE,"E709");var subQ141=sQuery(id+"F27.wireOp",EDGE,"E708");var subQ142=sQuery(id+"F27.wireOp",EDGE,"E707");var subQ143=sQuery(id+"F27.wireOp",EDGE,"E706");var subQ144=sQuery(id+"F27.wireOp",EDGE,"E705");var subQ145=sQuery(id+"F27.wireOp",EDGE,"E704");var subQ146=sQuery(id+"F27.wireOp",EDGE,"E703");var subQ147=sQuery(id+"F27.wireOp",EDGE,"E702");var subQ148=sQuery(id+"F27.wireOp",EDGE,"E701");var subQ149=sQuery(id+"F27.wireOp",EDGE,"E700");var subQ150=sQuery(id+"F27.wireOp",EDGE,"E699");var subQ151=sQuery(id+"F27.wireOp",EDGE,"E698");var subQ152=sQuery(id+"F27.wireOp",EDGE,"E697");var subQ153=sQuery(id+"F27.wireOp",EDGE,"E696");var subQ154=sQuery(id+"F27.wireOp",EDGE,"E695");var subQ155=sQuery(id+"F27.wireOp",EDGE,"E694");var subQ156=sQuery(id+"F27.wireOp",EDGE,"E693");var subQ157=sQuery(id+"F27.wireOp",EDGE,"E692");var subQ158=sQuery(id+"F27.wireOp",EDGE,"E691");var subQ159=sQuery(id+"F27.wireOp",EDGE,"E690");var subQ160=sQuery(id+"F27.wireOp",EDGE,"E689");var subQ161=sQuery(id+"F27.wireOp",EDGE,"E688");var subQ162=sQuery(id+"F27.wireOp",EDGE,"E687");var subQ163=sQuery(id+"F27.wireOp",EDGE,"E686");var subQ164=sQuery(id+"F27.wireOp",EDGE,"E685");var subQ165=sQuery(id+"F27.wireOp",EDGE,"E684");var subQ166=sQuery(id+"F27.wireOp",EDGE,"E683");var subQ167=sQuery(id+"F27.wireOp",EDGE,"E682");var subQ168=sQuery(id+"F27.wireOp",EDGE,"E681");var subQ169=sQuery(id+"F27.wireOp",EDGE,"E680");var subQ170=sQuery(id+"F27.wireOp",EDGE,"E679");var subQ171=sQuery(id+"F27.wireOp",EDGE,"E678");var subQ172=sQuery(id+"F27.wireOp",EDGE,"E677");var subQ173=sQuery(id+"F27.wireOp",EDGE,"E676");var subQ174=sQuery(id+"F27.wireOp",EDGE,"E675");var subQ175=sQuery(id+"F27.wireOp",EDGE,"E674");var subQ176=sQuery(id+"F27.wireOp",EDGE,"E673");var subQ177=sQuery(id+"F27.wireOp",EDGE,"E672");var subQ178=sQuery(id+"F27.wireOp",EDGE,"E671");var subQ179=sQuery(id+"F27.wireOp",EDGE,"E670");var subQ180=sQuery(id+"F27.wireOp",EDGE,"E669");var subQ181=sQuery(id+"F27.wireOp",EDGE,"E668");var subQ182=sQuery(id+"F27.wireOp",EDGE,"E667");var subQ183=sQuery(id+"F27.wireOp",EDGE,"E666");var subQ184=sQuery(id+"F27.wireOp",EDGE,"E665");var subQ185=sQuery(id+"F27.wireOp",EDGE,"E664");var subQ186=sQuery(id+"F27.wireOp",EDGE,"E663");var subQ187=sQuery(id+"F27.wireOp",EDGE,"E662");var subQ188=sQuery(id+"F27.wireOp",EDGE,"E661");var subQ189=sQuery(id+"F27.wireOp",EDGE,"E660");var subQ190=sQuery(id+"F27.wireOp",EDGE,"E659");var subQ191=sQuery(id+"F27.wireOp",EDGE,"E658");var subQ192=sQuery(id+"F27.wireOp",EDGE,"E657");var subQ193=sQuery(id+"F27.wireOp",EDGE,"E656");var subQ194=sQuery(id+"F27.wireOp",EDGE,"E655");var subQ195=sQuery(id+"F27.wireOp",EDGE,"E858");var subQ196=sQuery(id+"F27.wireOp",EDGE,"E857");var subQ197=sQuery(id+"F27.wireOp",EDGE,"E856");var subQ198=sQuery(id+"F27.wireOp",EDGE,"E854");var subQ199=sQuery(id+"F27.wireOp",EDGE,"E853");var subQ200=sQuery(id+"F27.wireOp",EDGE,"E850");var subQ201=sQuery(id+"F27.wireOp",EDGE,"E325");var subQ202=sQuery(id+"F27.wireOp",EDGE,"E324");var subQ203=sQuery(id+"F27.wireOp",EDGE,"E323");var subQ204=sQuery(id+"F27.wireOp",EDGE,"E321");var subQ205=sQuery(id+"F27.wireOp",EDGE,"E320");var subQ206=sQuery(id+"F27.wireOp",EDGE,"E319");var subQ207=sQuery(id+"F27.wireOp",EDGE,"E318");var subQ208=sQuery(id+"F27.wireOp",EDGE,"E317");var subQ209=sQuery(id+"F27.wireOp",EDGE,"E316");var subQ210=sQuery(id+"F27.wireOp",EDGE,"E315");var subQ211=sQuery(id+"F27.wireOp",EDGE,"E314");var subQ212=sQuery(id+"F27.wireOp",EDGE,"E313");var subQ213=sQuery(id+"F27.wireOp",EDGE,"E312");var subQ214=sQuery(id+"F27.wireOp",EDGE,"E311");var subQ215=sQuery(id+"F27.wireOp",EDGE,"E310");var subQ216=sQuery(id+"F27.wireOp",EDGE,"E309");var subQ217=sQuery(id+"F27.wireOp",EDGE,"E308");var subQ218=sQuery(id+"F27.wireOp",EDGE,"E307");var subQ219=sQuery(id+"F27.wireOp",EDGE,"E306");var subQ220=sQuery(id+"F27.wireOp",EDGE,"E305");var subQ221=sQuery(id+"F27.wireOp",EDGE,"E304");var subQ222=sQuery(id+"F27.wireOp",EDGE,"E303");var subQ223=sQuery(id+"F27.wireOp",EDGE,"E302");var subQ224=sQuery(id+"F27.wireOp",EDGE,"E301");var subQ225=sQuery(id+"F27.wireOp",EDGE,"E300");var subQ226=sQuery(id+"F27.wireOp",EDGE,"E299");var subQ227=sQuery(id+"F27.wireOp",EDGE,"E298");var subQ228=sQuery(id+"F27.wireOp",EDGE,"E297");var subQ229=sQuery(id+"F27.wireOp",EDGE,"E296");var subQ230=sQuery(id+"F27.wireOp",EDGE,"E295");var subQ231=sQuery(id+"F27.wireOp",EDGE,"E294");var subQ232=sQuery(id+"F27.wireOp",EDGE,"E293");var subQ233=sQuery(id+"F27.wireOp",EDGE,"E292");var subQ234=sQuery(id+"F27.wireOp",EDGE,"E291");var subQ235=sQuery(id+"F27.wireOp",EDGE,"E290");var subQ236=sQuery(id+"F27.wireOp",EDGE,"E289");var subQ237=sQuery(id+"F27.wireOp",EDGE,"E288");var subQ238=sQuery(id+"F27.wireOp",EDGE,"E287");var subQ239=sQuery(id+"F27.wireOp",EDGE,"E286");var subQ240=sQuery(id+"F27.wireOp",EDGE,"E285");var subQ241=sQuery(id+"F27.wireOp",EDGE,"E284");var subQ242=sQuery(id+"F27.wireOp",EDGE,"E283");var subQ243=sQuery(id+"F27.wireOp",EDGE,"E282");var subQ244=sQuery(id+"F27.wireOp",EDGE,"E281");var subQ245=sQuery(id+"F27.wireOp",EDGE,"E280");var subQ246=sQuery(id+"F27.wireOp",EDGE,"E279");var subQ247=sQuery(id+"F27.wireOp",EDGE,"E278");var subQ248=sQuery(id+"F27.wireOp",EDGE,"E277");var subQ249=sQuery(id+"F27.wireOp",EDGE,"E276");var subQ250=sQuery(id+"F27.wireOp",EDGE,"E275");var subQ251=sQuery(id+"F27.wireOp",EDGE,"E274");var subQ252=sQuery(id+"F27.wireOp",EDGE,"E273");var subQ253=sQuery(id+"F27.wireOp",EDGE,"E272");var subQ254=sQuery(id+"F27.wireOp",EDGE,"E271");var subQ255=sQuery(id+"F27.wireOp",EDGE,"E270");var subQ256=sQuery(id+"F27.wireOp",EDGE,"E269");var subQ257=sQuery(id+"F27.wireOp",EDGE,"E268");var subQ258=sQuery(id+"F27.wireOp",EDGE,"E267");var subQ259=sQuery(id+"F27.wireOp",EDGE,"E266");var subQ260=sQuery(id+"F27.wireOp",EDGE,"E265");var subQ261=sQuery(id+"F27.wireOp",EDGE,"E264");var subQ262=sQuery(id+"F27.wireOp",EDGE,"E263");var subQ263=sQuery(id+"F27.wireOp",EDGE,"E262");var subQ264=sQuery(id+"F27.wireOp",EDGE,"E261");var subQ265=sQuery(id+"F27.wireOp",EDGE,"E260");var subQ266=sQuery(id+"F27.wireOp",EDGE,"E259");var subQ267=sQuery(id+"F27.wireOp",EDGE,"E258");var subQ268=sQuery(id+"F27.wireOp",EDGE,"E257");var subQ269=sQuery(id+"F27.wireOp",EDGE,"E256");var subQ270=sQuery(id+"F27.wireOp",EDGE,"E255");var subQ271=sQuery(id+"F27.wireOp",EDGE,"E254");var subQ272=sQuery(id+"F27.wireOp",EDGE,"E253");var subQ273=sQuery(id+"F27.wireOp",EDGE,"E252");var subQ274=sQuery(id+"F27.wireOp",EDGE,"E251");var subQ275=sQuery(id+"F27.wireOp",EDGE,"E250");var subQ276=sQuery(id+"F27.wireOp",EDGE,"E249");var subQ277=sQuery(id+"F27.wireOp",EDGE,"E248");var subQ278=sQuery(id+"F27.wireOp",EDGE,"E247");var subQ279=sQuery(id+"F27.wireOp",EDGE,"E246");var subQ280=sQuery(id+"F27.wireOp",EDGE,"E245");var subQ281=sQuery(id+"F27.wireOp",EDGE,"E244");var subQ282=sQuery(id+"F27.wireOp",EDGE,"E243");var subQ283=sQuery(id+"F27.wireOp",EDGE,"E242");var subQ284=sQuery(id+"F27.wireOp",EDGE,"E241");var subQ285=sQuery(id+"F27.wireOp",EDGE,"E182");var subQ286=sQuery(id+"F27.wireOp",EDGE,"E181");var subQ287=sQuery(id+"F27.wireOp",EDGE,"E180");var subQ288=sQuery(id+"F27.wireOp",EDGE,"E179");var subQ289=sQuery(id+"F27.wireOp",EDGE,"E178");var subQ290=sQuery(id+"F27.wireOp",EDGE,"E177");var subQ291=sQuery(id+"F27.wireOp",EDGE,"E176");var subQ292=sQuery(id+"F27.wireOp",EDGE,"E175");var subQ293=sQuery(id+"F27.wireOp",EDGE,"E174");var subQ294=sQuery(id+"F27.wireOp",EDGE,"E173");var subQ295=sQuery(id+"F27.wireOp",EDGE,"E172");var subQ296=sQuery(id+"F27.wireOp",EDGE,"E171");var subQ297=sQuery(id+"F27.wireOp",EDGE,"E170");var subQ298=sQuery(id+"F27.wireOp",EDGE,"E123");var subQ299=sQuery(id+"F0.wireOp",EDGE,"E7.rect.bottom");var subQ302=sQuery(id+"F0.wireOp",EDGE,"E7.rect.right");var subQ303=sQuery(id+"F0.wireOp",EDGE,"E7.rect.left");var subQ304=sQuery(id+"F0.wireOp",EDGE,"E7.rect.top");var subQ305=sQuery(id+"F0.wireOp",EDGE,"E5.MirrorC");var subQ306=sQuery(id+"F0.wireOp",EDGE,"E3");var subQ307=sQuery(id+"F0.wireOp",EDGE,"E2");var subQ308=sQuery(id+"F0.wireOp",EDGE,"E1");var subQ309=makeQuery(id+"F1.opExtrude","CAP_FACE",FACE,{"disambiguationData":[OSD([subQ308,subQ307,subQ306,subQ305,subQ299,subQ304,subQ303,subQ302])],"isStart":false});var subQ312=makeQuery(id+"F6.opShell","OFFSET_FACE",FACE,{"disambiguationData":[OSD([subQ308,subQ307,subQ306,subQ305,subQ299,subQ304,subQ303,subQ302]),TDD([subQ309])]});Q1=makeQuery(id+"F29.boolean.opBoolean","MERGE",FACE,{"derivedFrom":[makeQuery(id+"F28.boolean.opBoolean","SPLIT",FACE,{"disambiguationData":[TD([makeQuery(id+"F28.opExtrude","SWEPT_FACE",FACE,{"disambiguationData":[OSD([subQ298])]})])],"derivedFrom":subQ312}),makeQuery(id+"F28.boolean.opBoolean","SPLIT",FACE,{"disambiguationData":[TD([makeQuery(id+"F28.opExtrude","SWEPT_FACE",FACE,{"disambiguationData":[OSD([subQ262])]})])],"derivedFrom":subQ312}),makeQuery(id+"F28.boolean.opBoolean","SPLIT",FACE,{"disambiguationData":[TD([makeQuery(id+"F28.opExtrude","SWEPT_FACE",FACE,{"disambiguationData":[OSD([subQ297])]})])],"derivedFrom":subQ312}),makeQuery(id+"F29.opExtrude","CAP_FACE",FACE,{"disambiguationData":[OSD([subQ298,sQuery(id+"F27.wireOp",EDGE,"E124"),sQuery(id+"F27.wireOp",EDGE,"E125"),sQuery(id+"F27.wireOp",EDGE,"E126"),sQuery(id+"F27.wireOp",EDGE,"E127"),sQuery(id+"F27.wireOp",EDGE,"E128"),sQuery(id+"F27.wireOp",EDGE,"E129"),sQuery(id+"F27.wireOp",EDGE,"E130"),sQuery(id+"F27.wireOp",EDGE,"E131"),sQuery(id+"F27.wireOp",EDGE,"E132"),sQuery(id+"F27.wireOp",EDGE,"E133"),sQuery(id+"F27.wireOp",EDGE,"E134"),sQuery(id+"F27.wireOp",EDGE,"E135"),sQuery(id+"F27.wireOp",EDGE,"E136"),sQuery(id+"F27.wireOp",EDGE,"E137"),sQuery(id+"F27.wireOp",EDGE,"E138"),sQuery(id+"F27.wireOp",EDGE,"E139"),sQuery(id+"F27.wireOp",EDGE,"E140"),sQuery(id+"F27.wireOp",EDGE,"E141"),sQuery(id+"F27.wireOp",EDGE,"E142"),sQuery(id+"F27.wireOp",EDGE,"E143"),sQuery(id+"F27.wireOp",EDGE,"E144"),sQuery(id+"F27.wireOp",EDGE,"E145"),sQuery(id+"F27.wireOp",EDGE,"E146"),sQuery(id+"F27.wireOp",EDGE,"E147"),sQuery(id+"F27.wireOp",EDGE,"E148"),sQuery(id+"F27.wireOp",EDGE,"E149"),sQuery(id+"F27.wireOp",EDGE,"E150"),sQuery(id+"F27.wireOp",EDGE,"E151"),sQuery(id+"F27.wireOp",EDGE,"E152"),sQuery(id+"F27.wireOp",EDGE,"E153"),sQuery(id+"F27.wireOp",EDGE,"E154"),sQuery(id+"F27.wireOp",EDGE,"E155"),sQuery(id+"F27.wireOp",EDGE,"E156"),sQuery(id+"F27.wireOp",EDGE,"E157"),sQuery(id+"F27.wireOp",EDGE,"E158"),sQuery(id+"F27.wireOp",EDGE,"E159"),sQuery(id+"F27.wireOp",EDGE,"E160"),sQuery(id+"F27.wireOp",EDGE,"E161"),sQuery(id+"F27.wireOp",EDGE,"E162"),sQuery(id+"F27.wireOp",EDGE,"E163"),sQuery(id+"F27.wireOp",EDGE,"E164"),sQuery(id+"F27.wireOp",EDGE,"E165"),sQuery(id+"F27.wireOp",EDGE,"E166"),sQuery(id+"F27.wireOp",EDGE,"E167"),sQuery(id+"F27.wireOp",EDGE,"E168"),sQuery(id+"F27.wireOp",EDGE,"E169"),subQ297,subQ296,subQ295,subQ294,subQ293,subQ292,subQ291,subQ290,subQ289,subQ288,subQ287,subQ286,subQ285,sQuery(id+"F27.wireOp",EDGE,"E183"),sQuery(id+"F27.wireOp",EDGE,"E184"),sQuery(id+"F27.wireOp",EDGE,"E185"),sQuery(id+"F27.wireOp",EDGE,"E186"),sQuery(id+"F27.wireOp",EDGE,"E187"),sQuery(id+"F27.wireOp",EDGE,"E188"),sQuery(id+"F27.wireOp",EDGE,"E189"),sQuery(id+"F27.wireOp",EDGE,"E190"),sQuery(id+"F27.wireOp",EDGE,"E191"),sQuery(id+"F27.wireOp",EDGE,"E192"),sQuery(id+"F27.wireOp",EDGE,"E193"),sQuery(id+"F27.wireOp",EDGE,"E194"),sQuery(id+"F27.wireOp",EDGE,"E195"),sQuery(id+"F27.wireOp",EDGE,"E196"),sQuery(id+"F27.wireOp",EDGE,"E197"),sQuery(id+"F27.wireOp",EDGE,"E198"),sQuery(id+"F27.wireOp",EDGE,"E199"),sQuery(id+"F27.wireOp",EDGE,"E200"),sQuery(id+"F27.wireOp",EDGE,"E201"),sQuery(id+"F27.wireOp",EDGE,"E202"),sQuery(id+"F27.wireOp",EDGE,"E203"),sQuery(id+"F27.wireOp",EDGE,"E204"),sQuery(id+"F27.wireOp",EDGE,"E205"),sQuery(id+"F27.wireOp",EDGE,"E206"),sQuery(id+"F27.wireOp",EDGE,"E207"),sQuery(id+"F27.wireOp",EDGE,"E208"),sQuery(id+"F27.wireOp",EDGE,"E209"),sQuery(id+"F27.wireOp",EDGE,"E210"),sQuery(id+"F27.wireOp",EDGE,"E211"),sQuery(id+"F27.wireOp",EDGE,"E212"),sQuery(id+"F27.wireOp",EDGE,"E213"),sQuery(id+"F27.wireOp",EDGE,"E214"),sQuery(id+"F27.wireOp",EDGE,"E215"),sQuery(id+"F27.wireOp",EDGE,"E216"),sQuery(id+"F27.wireOp",EDGE,"E217"),sQuery(id+"F27.wireOp",EDGE,"E218"),sQuery(id+"F27.wireOp",EDGE,"E219"),sQuery(id+"F27.wireOp",EDGE,"E220"),sQuery(id+"F27.wireOp",EDGE,"E221"),sQuery(id+"F27.wireOp",EDGE,"E222"),sQuery(id+"F27.wireOp",EDGE,"E223"),sQuery(id+"F27.wireOp",EDGE,"E224"),sQuery(id+"F27.wireOp",EDGE,"E225"),sQuery(id+"F27.wireOp",EDGE,"E226"),sQuery(id+"F27.wireOp",EDGE,"E227"),sQuery(id+"F27.wireOp",EDGE,"E228"),sQuery(id+"F27.wireOp",EDGE,"E229"),sQuery(id+"F27.wireOp",EDGE,"E230"),sQuery(id+"F27.wireOp",EDGE,"E231"),sQuery(id+"F27.wireOp",EDGE,"E232"),sQuery(id+"F27.wireOp",EDGE,"E233"),sQuery(id+"F27.wireOp",EDGE,"E234"),sQuery(id+"F27.wireOp",EDGE,"E235"),sQuery(id+"F27.wireOp",EDGE,"E236"),sQuery(id+"F27.wireOp",EDGE,"E237"),sQuery(id+"F27.wireOp",EDGE,"E238"),sQuery(id+"F27.wireOp",EDGE,"E239"),sQuery(id+"F27.wireOp",EDGE,"E240"),subQ284,subQ283,subQ282,subQ281,subQ280,subQ279,subQ278,subQ277,subQ276,subQ275,subQ274,subQ273,subQ272,subQ271,subQ270,subQ269,subQ268,subQ267,subQ266,subQ265,subQ264,subQ263,subQ262,subQ261,subQ260,subQ259,subQ258,subQ257,subQ256,subQ255,subQ254,subQ253,subQ252,subQ251,subQ250,subQ249,subQ248,subQ247,subQ246,subQ245,subQ244,subQ243,subQ242,subQ241,subQ240,subQ239,subQ238,subQ237,subQ236,subQ235,subQ234,subQ233,subQ232,subQ231,subQ230,subQ229,subQ228,subQ227,subQ226,subQ225,subQ224,subQ223,subQ222,subQ221,subQ220,subQ219,subQ218,subQ217,subQ216,subQ215,subQ214,subQ213,subQ212,subQ211,subQ210,subQ209,subQ208,subQ207,subQ206,subQ205,subQ204,sQuery(id+"F27.wireOp",EDGE,"E322"),subQ203,subQ202,subQ201,subQ200,sQuery(id+"F27.wireOp",EDGE,"E851"),sQuery(id+"F27.wireOp",EDGE,"E852"),subQ199,subQ198,sQuery(id+"F27.wireOp",EDGE,"E855"),subQ197,subQ196,subQ195])],"isStart":false}),makeQuery(id+"F29.opExtrude","CAP_FACE",FACE,{"disambiguationData":[OSD([subQ194,subQ193,subQ192,subQ191,subQ190,subQ189,subQ188,subQ187,subQ186,subQ185,subQ184,subQ183,subQ182,subQ181,subQ180,subQ179,subQ178,subQ177,subQ176,subQ175,subQ174,subQ173,subQ172,subQ171,subQ170,subQ169,subQ168,subQ167,subQ166,subQ165,subQ164,subQ163,subQ162,subQ161,subQ160,subQ159,subQ158,subQ157,subQ156,subQ155,subQ154,subQ153,subQ152,subQ151,subQ150,subQ149])],"isStart":false}),makeQuery(id+"F29.opExtrude","CAP_FACE",FACE,{"disambiguationData":[OSD([subQ148,subQ147,subQ146,subQ145,subQ144,subQ143,subQ142,subQ141,subQ140,subQ139,subQ138,subQ137,subQ136,subQ135,subQ134,subQ133,subQ132,subQ131,subQ130,subQ129,subQ128,subQ127,subQ126,subQ125,subQ124,subQ123,subQ122,subQ121,subQ120,subQ119,subQ118,subQ117,subQ116,subQ115,subQ114,subQ113,subQ112,subQ111,subQ110,subQ109,subQ108,subQ107,subQ106,subQ105,subQ104,subQ103,subQ102,subQ101,subQ100])],"isStart":false}),makeQuery(id+"F29.opExtrude","CAP_FACE",FACE,{"disambiguationData":[OSD([subQ99,subQ98,subQ97,subQ96,subQ95,subQ94,subQ93,subQ92,subQ91,subQ90,subQ89,subQ88,subQ87,subQ86,subQ85,subQ84,subQ83,subQ82,subQ81,subQ80,subQ79,subQ78,subQ77,subQ76,subQ75,subQ74,subQ73,subQ72,subQ71,subQ70,subQ69,subQ68,subQ67,subQ66,subQ65,subQ64,subQ63,subQ62,subQ61,subQ60,subQ59,subQ58,subQ57,subQ56,subQ55,subQ54,subQ53,subQ52,subQ51,subQ50,subQ49,subQ48,subQ47,subQ46,subQ45,subQ44])],"isStart":false}),makeQuery(id+"F29.opExtrude","CAP_FACE",FACE,{"disambiguationData":[OSD([subQ43,subQ42,subQ41,subQ40,subQ39,subQ38,subQ37,subQ36,subQ35,subQ34,subQ33,subQ32,subQ31,subQ30,subQ29,subQ28,subQ27,subQ26,subQ25,subQ24,subQ23,subQ22,subQ21,subQ20,subQ19,subQ18,subQ17,subQ16,subQ15,subQ14,subQ13,subQ12,subQ11,subQ10,subQ9,subQ8,subQ7,subQ6,subQ5,subQ4,subQ3,subQ2,subQ1,subQ0])],"isStart":false})]});}
            extrude(context, id + "F43", {"entities" : qUnion([Q0]), "operationType" : NewBodyOperationType.ADD, "endBound" : BoundingType.UP_TO_SURFACE, "endBoundEntityFace" : qUnion([Q1]), "depth" : 25 * mm});
        }
        {
            var Q0;
            {var subQ0=sQuery(id+"F0.wireOp",EDGE,"E7.rect.right");var subQ2=sQuery(id+"F0.wireOp",EDGE,"E7.rect.bottom");var subQ3=makeQuery(id+"F1.opExtrude","SWEPT_FACE",FACE,{"disambiguationData":[OSD([subQ2])]});var subQ8=sQuery(id+"F0.wireOp",EDGE,"E7.rect.left");var subQ17=sQuery(id+"F0.wireOp",EDGE,"E7.rect.top");var subQ19=sQuery(id+"F0.wireOp",EDGE,"E5.MirrorC");var subQ20=sQuery(id+"F0.wireOp",EDGE,"E3");var subQ21=sQuery(id+"F0.wireOp",EDGE,"E2");var subQ22=sQuery(id+"F0.wireOp",EDGE,"E1");var subQ23=makeQuery(id+"F1.opExtrude","CAP_FACE",FACE,{"disambiguationData":[OSD([subQ22,subQ21,subQ20,subQ19,subQ2,subQ17,subQ8,subQ0])],"isStart":true});Q0=makeQuery(id+"F26.boolean.opBoolean","MERGE",FACE,{"derivedFrom":[makeQuery(id+"F6.opShell","OFFSET_FACE",FACE,{"disambiguationData":[OSD([subQ22,subQ21,subQ20,subQ19,subQ2,subQ17,subQ8,subQ0]),TDD([subQ23]),OD(2.0)]}),makeQuery(id+"F14.boolean.opBoolean","SPLIT",FACE,{"disambiguationData":[TD([makeQuery(id+"F1.opExtrude","SWEPT_FACE",FACE,{"disambiguationData":[OSD([subQ22])]})])],"derivedFrom":makeQuery(id+"F6.opShell","OFFSET_FACE",FACE,{"disambiguationData":[OSD([subQ22,subQ21,subQ20,subQ19,subQ2,subQ17,subQ8,subQ0]),TDD([subQ23]),OD(0.0)]})}),makeQuery(id+"F14.boolean.opBoolean","SPLIT",FACE,{"disambiguationData":[TD([subQ3])],"derivedFrom":makeQuery(id+"F10.boolean.opBoolean","SPLIT",FACE,{"disambiguationData":[TD([subQ3])],"derivedFrom":makeQuery(id+"F6.opShell","OFFSET_FACE",FACE,{"disambiguationData":[OSD([subQ22,subQ21,subQ20,subQ19,subQ2,subQ17,subQ8,subQ0]),TDD([subQ23]),OD(3.0)]})})}),makeQuery(id+"F26.opExtrude","CAP_FACE",FACE,{"disambiguationData":[OSD([sQuery(id+"F25.wireOp",EDGE,"E102.top"),sQuery(id+"F25.wireOp",EDGE,"E102.left"),sQuery(id+"F25.wireOp",EDGE,"E102.right"),sQuery(id+"F25.wireOp",EDGE,"E103.bottom"),sQuery(id+"F25.wireOp",EDGE,"E103.top"),sQuery(id+"F25.wireOp",EDGE,"E103.right"),sQuery(id+"F25.wireOp",EDGE,"E102.bottom"),sQuery(id+"F25.wireOp",EDGE,"E107.top"),sQuery(id+"F25.wireOp",EDGE,"E107.left"),sQuery(id+"F25.wireOp",EDGE,"E107.right")])],"isStart":true}),makeQuery(id+"F26.opExtrude","CAP_FACE",FACE,{"disambiguationData":[OSD([sQuery(id+"F25.wireOp",EDGE,"E105.bottom"),sQuery(id+"F25.wireOp",EDGE,"E105.top"),sQuery(id+"F25.wireOp",EDGE,"E105.left"),sQuery(id+"F25.wireOp",EDGE,"E105.right"),sQuery(id+"F25.wireOp",EDGE,"E106.bottom"),sQuery(id+"F25.wireOp",EDGE,"E106.top"),sQuery(id+"F25.wireOp",EDGE,"E106.right")])],"isStart":true})]});}
            cPlane(context, id + "F44", {"entities" : qUnion([Q0]), "cplaneType" : CPlaneType.OFFSET, "offset" : 0.6 * mm, "oppositeDirection" : true, "width" : 150 * mm, "height" : 150 * mm});
        }
        {
            var Q0;
            Q0=qCreatedBy(id+"F44.planeOp",FACE);
            var sketch = newSketch(context, id + "F45", { "sketchPlane" : qUnion([Q0])});
            skLineSegment(sketch, "E891.bottom", {"start": v(-24.07, 22.32) * mm, "end": v(-9.14, 22.32) * mm});
            skLineSegment(sketch, "E891.top", {"start": v(-24.07, -4.65) * mm, "end": v(-9.14, -4.65) * mm});
            skLineSegment(sketch, "E891.left", {"start": v(-24.07, 22.32) * mm, "end": v(-24.07, -4.65) * mm});
            skLineSegment(sketch, "E891.right", {"start": v(-9.14, 22.32) * mm, "end": v(-9.14, -4.65) * mm});
            skSolve(sketch);
        }
        {
            var Q0;
            Q0=qSketchRegion(id+"F45",true);
            extrude(context, id + "F46", {"entities" : qUnion([Q0]), "operationType" : NewBodyOperationType.ADD, "depth" : 0.6 * mm});
        }
        {
            var Q0;
            Q0=qCreatedBy(makeId("Top.planeOp"),FACE);
            var sketch = newSketch(context, id + "F47", { "sketchPlane" : qUnion([Q0])});
            skLineSegment(sketch, "E892.bottom", {"start": v(-32.16, -19.74) * mm, "end": v(-31.86, -19.74) * mm});
            skLineSegment(sketch, "E892.top", {"start": v(-32.16, -29.43) * mm, "end": v(-31.86, -29.43) * mm});
            skLineSegment(sketch, "E892.left", {"start": v(-32.16, -19.74) * mm, "end": v(-32.16, -29.43) * mm});
            skLineSegment(sketch, "E892.right", {"start": v(-31.86, -19.74) * mm, "end": v(-31.86, -29.43) * mm});
            skLineSegment(sketch, "E893.bottom", {"start": v(-34.1, 3.13) * mm, "end": v(-31.72, 3.13) * mm});
            skLineSegment(sketch, "E893.top", {"start": v(-34.1, 0.35) * mm, "end": v(-31.72, 0.35) * mm});
            skLineSegment(sketch, "E893.left", {"start": v(-34.1, 3.13) * mm, "end": v(-34.1, 0.35) * mm});
            skLineSegment(sketch, "E893.right", {"start": v(-31.72, 3.13) * mm, "end": v(-31.72, 0.35) * mm});
            skLineSegment(sketch, "E894.bottom", {"start": v(-34.13, -7.9) * mm, "end": v(-31.72, -7.9) * mm});
            skLineSegment(sketch, "E894.top", {"start": v(-34.13, -10.8) * mm, "end": v(-31.72, -10.8) * mm});
            skLineSegment(sketch, "E894.left", {"start": v(-34.13, -7.9) * mm, "end": v(-34.13, -10.8) * mm});
            skLineSegment(sketch, "E894.right", {"start": v(-31.72, -7.9) * mm, "end": v(-31.72, -10.8) * mm});
            skSolve(sketch);
        }
        {
            var Q0;
            Q0=qSketchRegion(id+"F47",true);
            var Q1;
            Q1=makeQuery(id+"F35.boolean.opBoolean","MERGE",FACE,{"derivedFrom":[makeQuery(id+"F3.boolean.opBoolean","COPY",FACE,{"derivedFrom":makeQuery(id+"F3.opExtrude","SWEPT_FACE",FACE,{"disambiguationData":[OSD([sQuery(id+"F2.wireOp",EDGE,"E14")])]})}),makeQuery(id+"F35.opExtrude","CAP_FACE",FACE,{"disambiguationData":[OSD([sQuery(id+"F34.wireOp",EDGE,"E864")])],"isStart":false}),makeQuery(id+"F35.opExtrude","CAP_FACE",FACE,{"disambiguationData":[OSD([sQuery(id+"F34.wireOp",EDGE,"E865")])],"isStart":false})]});
            extrude(context, id + "F48", {"entities" : qUnion([Q0]), "operationType" : NewBodyOperationType.ADD, "endBound" : BoundingType.UP_TO_SURFACE, "endBoundEntityFace" : qUnion([Q1]), "depth" : 25 * mm});
        }
        {
            var Q0;
            Q0=makeQuery(id+"F35.boolean.opBoolean","MERGE",FACE,{"derivedFrom":[makeQuery(id+"F3.boolean.opBoolean","COPY",FACE,{"derivedFrom":makeQuery(id+"F3.opExtrude","SWEPT_FACE",FACE,{"disambiguationData":[OSD([sQuery(id+"F2.wireOp",EDGE,"E14")])]})}),makeQuery(id+"F35.opExtrude","CAP_FACE",FACE,{"disambiguationData":[OSD([sQuery(id+"F34.wireOp",EDGE,"E864")])],"isStart":false}),makeQuery(id+"F35.opExtrude","CAP_FACE",FACE,{"disambiguationData":[OSD([sQuery(id+"F34.wireOp",EDGE,"E865")])],"isStart":false})]});
            var sketch = newSketch(context, id + "F49", { "sketchPlane" : qUnion([Q0])});
            skText(sketch, "E895", { "text": "12v", "fontName": "OpenSans-Bold.ttf"});
            skText(sketch, "E896", { "text": "L3 L2 L1", "fontName": "OpenSans-Bold.ttf"});
            const initialGuessF49  = {"E895": [0.019, 0, 1, 0, 0.0042], "E896": [-0.00949, -0.00516, 1, 0, 0.00516]};
            skSetInitialGuess(sketch, initialGuessF49);
            skSolve(sketch);
        }
        {
            var Q0;
            Q0=qSketchRegion(id+"F49",true);
            extrude(context, id + "F50", {"entities" : qUnion([Q0]), "operationType" : NewBodyOperationType.ADD, "depth" : 0.9 * mm});
        }
        {
            var Q0;
            {var subQ1=sQuery(id+"F0.wireOp",EDGE,"E7.rect.top");var subQ2=sQuery(id+"F0.wireOp",EDGE,"E7.rect.right");var subQ9=makeQuery(id+"F1.opExtrude","SWEPT_FACE",FACE,{"disambiguationData":[OSD([subQ1])]});Q0=makeQuery(id+"F19.boolean.opBoolean","SPLIT",FACE,{"disambiguationData":[TD([makeQuery(id+"F1.opExtrude","SWEPT_FACE",FACE,{"disambiguationData":[OSD([subQ2])]})])],"derivedFrom":subQ9});}
            var sketch = newSketch(context, id + "F51", { "sketchPlane" : qUnion([Q0])});
            skText(sketch, "E897", { "text": "S2", "fontName": "OpenSans-Bold.ttf"});
            skText(sketch, "E898", { "text": "S3", "fontName": "OpenSans-Bold.ttf"});
            skText(sketch, "E899", { "text": "S1", "fontName": "OpenSans-Bold.ttf"});
            const initialGuessF51  = {"E897": [0.0049, 0.00582, 1, 0, 0.00474], "E898": [-0.01363, 0, 1, 0, 0.0043], "E899": [0.02768, 0.00016, 1, 0, 0.0043]};
            skSetInitialGuess(sketch, initialGuessF51);
            skSolve(sketch);
        }
        {
            var Q0;
            Q0=qSketchRegion(id+"F51",true);
            extrude(context, id + "F52", {"entities" : qUnion([Q0]), "operationType" : NewBodyOperationType.ADD, "depth" : 1 * mm, "hasSecondDirection" : true, "secondDirectionOppositeDirection" : true, "secondDirectionDepth" : 1 * mm});
        }
        {
            var Q0;
            {var subQ0=sQuery(id+"F2.wireOp",EDGE,"E22");var subQ1=sQuery(id+"F2.wireOp",EDGE,"E20");Q0=makeQuery(id+"F38.boolean.opBoolean","MERGE",FACE,{"derivedFrom":[makeQuery(id+"F24.boolean.opBoolean","SPLIT",FACE,{"disambiguationData":[TD([makeQuery(id+"F1.opExtrude","SWEPT_FACE",FACE,{"disambiguationData":[OSD([sQuery(id+"F0.wireOp",EDGE,"E3")])]})])],"derivedFrom":makeQuery(id+"F3.boolean.opBoolean","COPY",FACE,{"derivedFrom":makeQuery(id+"F3.opExtrude","SWEPT_FACE",FACE,{"disambiguationData":[OSD([subQ1,subQ0])]})})}),makeQuery(id+"F38.opExtrude","CAP_FACE",FACE,{"disambiguationData":[OSD([sQuery(id+"F37.wireOp",EDGE,"E866")])],"isStart":false}),makeQuery(id+"F38.opExtrude","CAP_FACE",FACE,{"disambiguationData":[OSD([sQuery(id+"F37.wireOp",EDGE,"E867")])],"isStart":false})]});}
            var sketch = newSketch(context, id + "F53", { "sketchPlane" : qUnion([Q0])});
            skText(sketch, "E900", { "text": "S6", "fontName": "OpenSans-Bold.ttf"});
            const initialGuessF53  = {"E900": [0.00608, -0.02103, 1, 0, 0.00418]};
            skSetInitialGuess(sketch, initialGuessF53);
            skSolve(sketch);
        }
        {
            var Q0;
            Q0=qSketchRegion(id+"F53",true);
            var Q1;
            Q1=makeQuery(id+"F4.opFillet","BLEND_FACE",FACE,{"disambiguationData":[OSD([sQuery(id+"F0.wireOp",EDGE,"E7.rect.left"),sQuery(id+"F2.wireOp",EDGE,"E20"),sQuery(id+"F2.wireOp",EDGE,"E22")])]});
            extrude(context, id + "F54", {"entities" : qUnion([Q0]), "operationType" : NewBodyOperationType.ADD, "depth" : 1 * mm, "hasSecondDirection" : true, "secondDirectionOppositeDirection" : true, "secondDirectionBoundEntityFace" : qUnion([Q1]), "secondDirectionDepth" : 1.6 * mm});
        }
        {
            var Q0;
            {var subQ1=sQuery(id+"F0.wireOp",EDGE,"E7.rect.left");var subQ3=sQuery(id+"F0.wireOp",EDGE,"E7.rect.bottom");Q0=makeQuery(id+"F9.boolean.opBoolean","SPLIT",FACE,{"disambiguationData":[TD([makeQuery(id+"F1.opExtrude","SWEPT_FACE",FACE,{"disambiguationData":[OSD([subQ3])]})])],"derivedFrom":makeQuery(id+"F1.opExtrude","SWEPT_FACE",FACE,{"disambiguationData":[OSD([subQ1])]})});}
            var sketch = newSketch(context, id + "F55", { "sketchPlane" : qUnion([Q0])});
            skText(sketch, "E901", { "text": "S5", "fontName": "OpenSans-Bold.ttf"});
            skText(sketch, "E902", { "text": "S4", "fontName": "OpenSans-Bold.ttf"});
            const initialGuessF55  = {"E901": [-0.02893, 0, 1, 0, 0.00488], "E902": [0.00624, 0, 1, 0, 0.0048]};
            skSetInitialGuess(sketch, initialGuessF55);
            skSolve(sketch);
        }
        {
            var Q0;
            Q0=qSketchRegion(id+"F55",true);
            extrude(context, id + "F56", {"entities" : qUnion([Q0]), "operationType" : NewBodyOperationType.ADD, "depth" : 1.2 * mm});
        }
        {
            var Q0;
            {var subQ0=sQuery(id+"F12.wireOp",EDGE,"E51");Q0=makeQuery(id+"F12.imprint","IMPRINT",FACE,{"disambiguationData":[TD([[makeQuery(id+"F12.imprint","IMPRINT",EDGE,{"derivedFrom":subQ0}),-1.0]])]});}
            extrude(context, id + "F57", {"entities" : qUnion([Q0]), "operationType" : NewBodyOperationType.REMOVE, "oppositeDirection" : true, "depth" : 8 * mm});
        }
        {
            var Q0;
            Q0=makeQuery(id+"F0.imprint","IMPRINT",FACE,{"disambiguationData":[TD([[makeQuery(id+"F0.imprint","IMPRINT",EDGE,{"derivedFrom":sQuery(id+"F0.wireOp",EDGE,"E1")}),-1.0]])]});
            var sketch = newSketch(context, id + "F58", { "sketchPlane" : qUnion([Q0])});
            skPoint(sketch, "E903.first.point", {"position": v(6.62, 7.4) * mm});
            skPoint(sketch, "E903.second.point", {"position": v(6.67, 13.38) * mm});
            skPoint(sketch, "E903.third.point", {"position": v(3.73, 10.32) * mm});
            skPoint(sketch, "E904.first.point", {"position": v(17.45, 10.32) * mm});
            skPoint(sketch, "E904.second.point", {"position": v(14.7, 13.34) * mm});
            skPoint(sketch, "E904.third.point", {"position": v(14.7, 7.45) * mm});
            skPoint(sketch, "E905.MirrorP", {"position": v(17.5, 10.32) * mm});
            skPoint(sketch, "E906.MirrorP", {"position": v(14.62, 7.4) * mm});
            skPoint(sketch, "E907.MirrorP", {"position": v(14.57, 13.38) * mm});
            skLineSegment(sketch, "E908", {"start": v(14.46, 6.75) * mm, "end": v(6.63, 6.75) * mm});
            skLineSegment(sketch, "E909", {"start": v(14.66, 13.88) * mm, "end": v(6.96, 13.88) * mm});
            skArc(sketch, "E910.trimOffspring", {"start": v(6.96, 13.88) * mm, "mid": v(3.17, 10.38) * mm, "end": v(6.84, 6.75) * mm});
            skArc(sketch, "E911.trimOffspring", {"start": v(14.27, 13.88) * mm, "mid": v(18.08, 10.42) * mm, "end": v(14.46, 6.75) * mm});
            skPoint(sketch, "E912.orphan", {"position": v(14.5, 10.4) * mm});
            skPoint(sketch, "E913.start.orphan", {"position": v(10.62, 10.36) * mm});
            skCircle(sketch, "E914", {"center": v(6.74, 10.32) * mm, "radius": 2.01 * mm});
            skCircle(sketch, "E915", {"center": v(14.51, 10.32) * mm, "radius": 2.16 * mm});
            skLineSegment(sketch, "E916.trimOffspring", {"start": v(6.52, 13.88) * mm, "end": v(6.5, 13.88) * mm});
            skSolve(sketch);
        }
        {
            var Q0;
            Q0=qSketchRegion(id+"F58",true);
            extrude(context, id + "F59", {"entities" : qUnion([Q0]), "operationType" : NewBodyOperationType.REMOVE, "depth" : 8.2 * mm});
        }
    });
